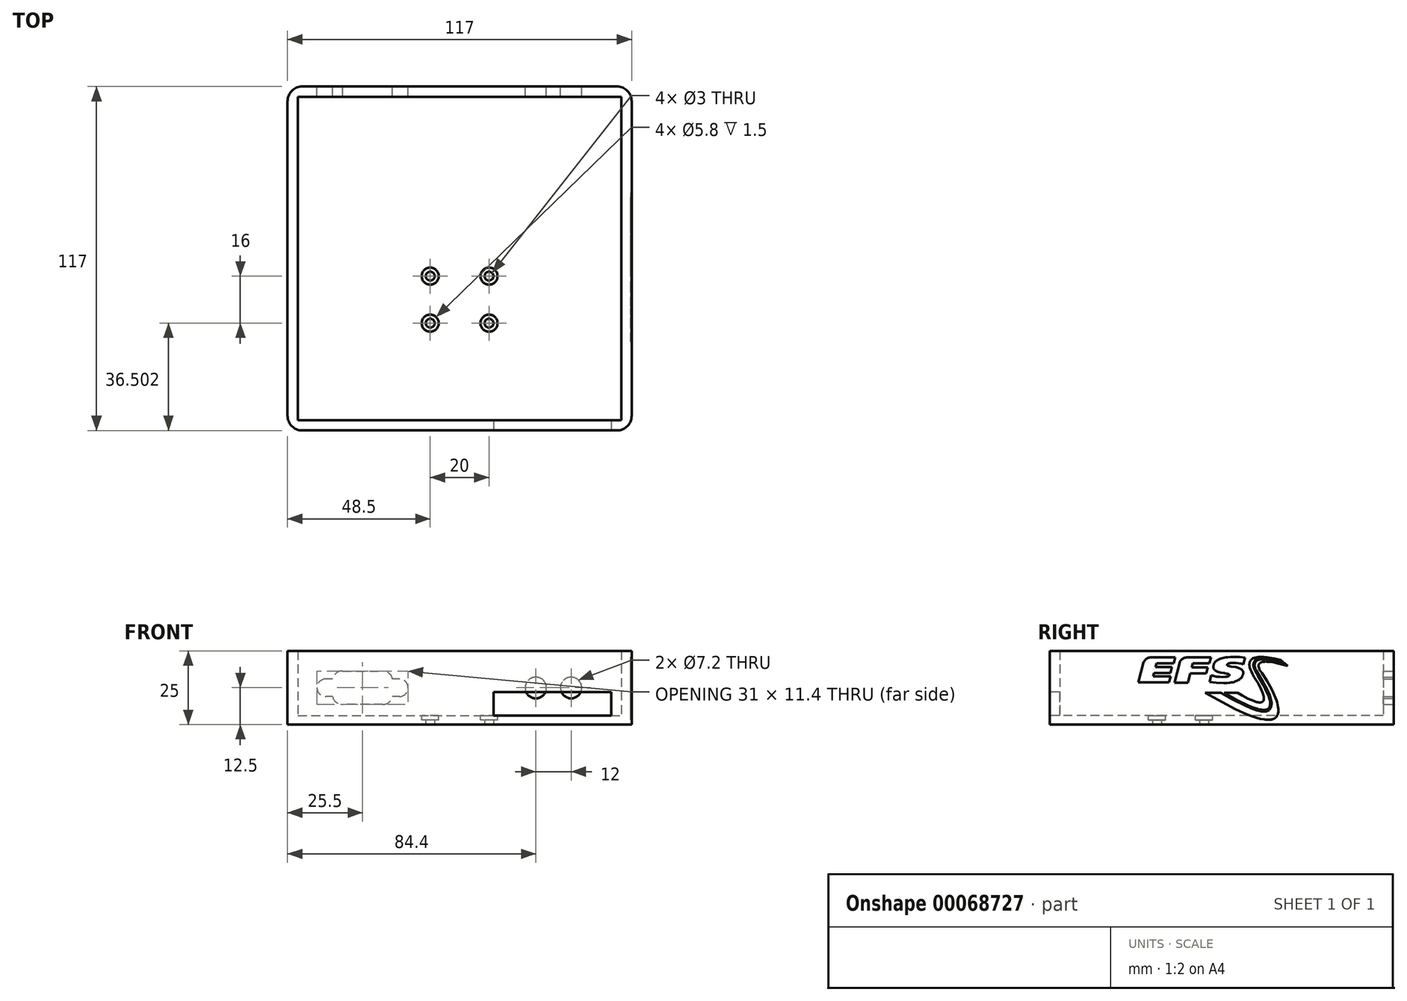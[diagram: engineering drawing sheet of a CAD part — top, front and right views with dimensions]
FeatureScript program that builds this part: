
annotation { "Feature Type Name" : "Feature", "Feature Type Description" : "" }
export const myFeature = defineFeature(function(context is Context, id is Id, definition is map)
    precondition{}
    {
        {
            var Q0;
            Q0=qCreatedBy(makeId("Top.planeOp"),FACE);
            var sketch = newSketch(context, id + "F0", { "sketchPlane" : qUnion([Q0])});
            skLineSegment(sketch, "E0.bottom", {"start": v(-55, 78.83) * mm, "end": v(55, 78.83) * mm});
            skLineSegment(sketch, "E0.top", {"start": v(-55, -31.17) * mm, "end": v(55, -31.17) * mm});
            skLineSegment(sketch, "E0.left", {"start": v(-55, 78.83) * mm, "end": v(-55, -31.17) * mm});
            skLineSegment(sketch, "E0.right", {"start": v(55, 78.83) * mm, "end": v(55, -31.17) * mm});
            skLineSegment(sketch, "E1.0", {"start": v(-58.5, 82.33) * mm, "end": v(-58.5, -34.67) * mm});
            skLineSegment(sketch, "E1.1", {"start": v(-58.5, 82.33) * mm, "end": v(58.5, 82.33) * mm});
            skLineSegment(sketch, "E1.2", {"start": v(58.5, 82.33) * mm, "end": v(58.5, -34.67) * mm});
            skLineSegment(sketch, "E1.3", {"start": v(-58.5, -34.67) * mm, "end": v(58.5, -34.67) * mm});
            skSolve(sketch);
        }
        {
            var Q0;
            Q0=makeQuery(id+"F0.imprint","IMPRINT",FACE,{"disambiguationData":[TD([[makeQuery(id+"F0.imprint","IMPRINT",EDGE,{"derivedFrom":sQuery(id+"F0.wireOp",EDGE,"E0.bottom")}),1.0]])]});
            extrude(context, id + "F1", {"entities" : qUnion([Q0]), "depth" : 25 * mm});
        }
        {
            var Q0;
            Q0=makeQuery(id+"F0.imprint","IMPRINT",FACE,{"disambiguationData":[TD([[makeQuery(id+"F0.imprint","IMPRINT",EDGE,{"derivedFrom":sQuery(id+"F0.wireOp",EDGE,"E0.bottom")}),-1.0]])]});
            var Q1;
            Q1=makeQuery(id+"F0.imprint","IMPRINT",FACE,{"disambiguationData":[TD([[makeQuery(id+"F0.imprint","IMPRINT",EDGE,{"derivedFrom":sQuery(id+"F0.wireOp",EDGE,"998007f4-a65a-47df-ae81-ff0484897dbd.bottom")}),1.0]])]});
            var Q2;
            Q2=makeQuery(id+"F0.imprint","IMPRINT",FACE,{"disambiguationData":[TD([[makeQuery(id+"F0.imprint","IMPRINT",EDGE,{"derivedFrom":sQuery(id+"F0.wireOp",EDGE,"998007f4-a65a-47df-ae81-ff0484897dbd.bottom")}),-1.0]])]});
            extrude(context, id + "F2", {"entities" : qUnion([Q0, Q1, Q2]), "operationType" : NewBodyOperationType.ADD, "depth" : 3 * mm});
        }
        {
            var Q0;
            Q0=makeQuery(id+"F1.opExtrude","SWEPT_EDGE",EDGE,{"disambiguationData":[OSD([sQuery(id+"F0.wireOp",EDGE,"E1.2"),sQuery(id+"F0.wireOp",EDGE,"E1.3")])]});
            fillet(context, id + "F3", {"entities" : qUnion([Q0]), "radius" : 5 * mm, "tangentPropagation" : true, "allowEdgeOverflow" : false});
        }
        {
            var Q0;
            Q0=makeQuery(id+"F1.opExtrude","SWEPT_EDGE",EDGE,{"disambiguationData":[OSD([sQuery(id+"F0.wireOp",EDGE,"E1.0"),sQuery(id+"F0.wireOp",EDGE,"E1.3")])]});
            fillet(context, id + "F4", {"entities" : qUnion([Q0]), "radius" : 5 * mm, "tangentPropagation" : true, "allowEdgeOverflow" : false});
        }
        {
            var Q0;
            Q0=makeQuery(id+"F1.opExtrude","SWEPT_EDGE",EDGE,{"disambiguationData":[OSD([sQuery(id+"F0.wireOp",EDGE,"E1.0"),sQuery(id+"F0.wireOp",EDGE,"E1.3")])]});
            var Q1;
            Q1=makeQuery(id+"F1.opExtrude","SWEPT_EDGE",EDGE,{"disambiguationData":[OSD([sQuery(id+"F0.wireOp",EDGE,"E1.1"),sQuery(id+"F0.wireOp",EDGE,"E1.2")])]});
            fillet(context, id + "F5", {"entities" : qUnion([Q0, Q1]), "radius" : 5 * mm, "tangentPropagation" : true, "allowEdgeOverflow" : false});
        }
        {
            var Q0;
            Q0=makeQuery(id+"F1.opExtrude","SWEPT_EDGE",EDGE,{"disambiguationData":[OSD([sQuery(id+"F0.wireOp",EDGE,"E1.0"),sQuery(id+"F0.wireOp",EDGE,"E1.1")])]});
            fillet(context, id + "F6", {"entities" : qUnion([Q0]), "radius" : 5 * mm, "tangentPropagation" : true, "allowEdgeOverflow" : false});
        }
        {
            var Q0;
            Q0=makeQuery(id+"F1.opExtrude","SWEPT_FACE",FACE,{"disambiguationData":[OSD([sQuery(id+"F0.wireOp",EDGE,"E1.1")])]});
            var sketch = newSketch(context, id + "F7", { "sketchPlane" : qUnion([Q0])});
            skArc(sketch, "E2", {"start": v(42.5, 12.68) * mm, "mid": v(42.5, 12.59) * mm, "end": v(42.5, 12.5) * mm});
            skArc(sketch, "E3", {"start": v(23.5, 12.32) * mm, "mid": v(23.5, 12.41) * mm, "end": v(23.5, 12.5) * mm});
            skArc(sketch, "E4", {"start": v(37.35, 12.5) * mm, "mid": v(37.35, 12.5) * mm, "end": v(37.35, 12.5) * mm});
            skArc(sketch, "E5", {"start": v(26.15, 18.2) * mm, "mid": v(24, 17.44) * mm, "end": v(22.82, 15.5) * mm});
            skArc(sketch, "E6", {"start": v(28.65, 12.5) * mm, "mid": v(26.03, 13.6) * mm, "end": v(23.5, 12.32) * mm});
            skLineSegment(sketch, "E7", {"start": v(20.5, 12.5) * mm, "end": v(45.5, 12.5) * mm, "construction": true});
            skPoint(sketch, "E8", {"position": v(33, 12.5) * mm});
            skLineSegment(sketch, "E9", {"start": v(33, 6.8) * mm, "end": v(33, 18.2) * mm, "construction": true});
            skLineSegment(sketch, "E10", {"start": v(20.5, 15.5) * mm, "end": v(22.82, 15.5) * mm});
            skLineSegment(sketch, "E11", {"start": v(20.5, 9.5) * mm, "end": v(22.82, 9.5) * mm});
            skLineSegment(sketch, "E12", {"start": v(43.18, 9.5) * mm, "end": v(45.5, 9.5) * mm});
            skLineSegment(sketch, "E13", {"start": v(43.18, 15.5) * mm, "end": v(45.5, 15.5) * mm});
            skLineSegment(sketch, "E14", {"start": v(26.15, 6.8) * mm, "end": v(39.85, 6.8) * mm});
            skLineSegment(sketch, "E15", {"start": v(39.85, 18.2) * mm, "end": v(26.15, 18.2) * mm});
            skArc(sketch, "E16.trimOffspring", {"start": v(42.35, 12.5) * mm, "mid": v(42.35, 12.5) * mm, "end": v(42.35, 12.5) * mm});
            skArc(sketch, "E17.trimOffspring", {"start": v(43.23, 14.47) * mm, "mid": v(42.37, 17.08) * mm, "end": v(39.85, 18.2) * mm});
            skArc(sketch, "E18.trimOffspring", {"start": v(45.5, 9.5) * mm, "mid": v(48.23, 13.75) * mm, "end": v(43.23, 14.47) * mm});
            skArc(sketch, "E19.trimOffspring", {"start": v(42.5, 12.32) * mm, "mid": v(42.43, 12.41) * mm, "end": v(42.35, 12.5) * mm});
            skArc(sketch, "E20.trimOffspring", {"start": v(39.72, 6.8) * mm, "mid": v(41.94, 7.52) * mm, "end": v(43.18, 9.5) * mm});
            skArc(sketch, "E21.trimOffspring", {"start": v(22.82, 9.5) * mm, "mid": v(24, 7.56) * mm, "end": v(26.15, 6.8) * mm});
            skArc(sketch, "E22.trimOffspring", {"start": v(20.5, 15.5) * mm, "mid": v(17.5, 12.5) * mm, "end": v(20.5, 9.5) * mm});
            skArc(sketch, "E23.trimOffspring", {"start": v(23.5, 12.68) * mm, "mid": v(23.57, 12.59) * mm, "end": v(23.65, 12.5) * mm});
            skCircle(sketch, "E24", {"center": v(-37.9, 12.5) * mm, "radius": 3.6 * mm});
            skCircle(sketch, "E25", {"center": v(-25.9, 12.5) * mm, "radius": 3.6 * mm});
            skLineSegment(sketch, "E26", {"start": v(-52.56, 12.5) * mm, "end": v(59.26, 12.5) * mm, "construction": true});
            skSolve(sketch);
        }
        {
            var Q0;
            Q0 = qSketchRegion(id + "F7", true);
            extrude(context, id + "F8", {"entities" : qUnion([Q0]), "operationType" : NewBodyOperationType.REMOVE, "oppositeDirection" : true, "depth" : 8.6 * mm});
        }
        {
            var Q0;
            Q0=makeQuery(id+"F1.opExtrude","SWEPT_FACE",FACE,{"disambiguationData":[OSD([sQuery(id+"F0.wireOp",EDGE,"E1.3")])]});
            var sketch = newSketch(context, id + "F9", { "sketchPlane" : qUnion([Q0])});
            skLineSegment(sketch, "E27.bottom", {"start": v(11.5, 11) * mm, "end": v(51.5, 11) * mm});
            skLineSegment(sketch, "E27.top", {"start": v(11.5, 3) * mm, "end": v(51.5, 3) * mm});
            skLineSegment(sketch, "E27.left", {"start": v(11.5, 11) * mm, "end": v(11.5, 3) * mm});
            skLineSegment(sketch, "E27.right", {"start": v(51.5, 11) * mm, "end": v(51.5, 3) * mm});
            skSolve(sketch);
        }
        {
            var Q0;
            Q0=makeQuery(id+"F9.imprint","IMPRINT",FACE,{"disambiguationData":[TD([[makeQuery(id+"F9.imprint","IMPRINT",EDGE,{"derivedFrom":sQuery(id+"F9.wireOp",EDGE,"E27.bottom")}),-1.0]])]});
            extrude(context, id + "F10", {"entities" : qUnion([Q0]), "operationType" : NewBodyOperationType.REMOVE, "oppositeDirection" : true, "depth" : 25 * mm});
        }
        {
            var Q0;
            {var subQ0=sQuery(id+"F0.wireOp",EDGE,"E0.right");var subQ1=sQuery(id+"F0.wireOp",EDGE,"E0.left");var subQ2=sQuery(id+"F0.wireOp",EDGE,"E0.top");var subQ3=sQuery(id+"F0.wireOp",EDGE,"E0.bottom");Q0=makeQuery(id+"F2.boolean.opBoolean","MERGE",FACE,{"derivedFrom":[makeQuery(id+"F1.opExtrude","CAP_FACE",FACE,{"disambiguationData":[OSD([subQ3,subQ2,subQ1,subQ0,sQuery(id+"F0.wireOp",EDGE,"E1.0"),sQuery(id+"F0.wireOp",EDGE,"E1.1"),sQuery(id+"F0.wireOp",EDGE,"E1.2"),sQuery(id+"F0.wireOp",EDGE,"E1.3")])],"isStart":true}),makeQuery(id+"F2.opExtrude","CAP_FACE",FACE,{"disambiguationData":[OSD([subQ3,subQ2,subQ1,subQ0])],"isStart":true})]});}
            var sketch = newSketch(context, id + "F11", { "sketchPlane" : qUnion([Q0])});
            skLineSegment(sketch, "E28.bottom", {"start": v(-27, 4.67) * mm, "end": v(27, 4.67) * mm, "construction": true});
            skLineSegment(sketch, "E28.top", {"start": v(-27, -24.33) * mm, "end": v(27, -24.33) * mm, "construction": true});
            skLineSegment(sketch, "E28.left", {"start": v(-27, 4.67) * mm, "end": v(-27, -24.33) * mm, "construction": true});
            skLineSegment(sketch, "E28.right", {"start": v(27, 4.67) * mm, "end": v(27, -24.33) * mm, "construction": true});
            skLineSegment(sketch, "E29", {"start": v(-32.07, -9.83) * mm, "end": v(32.08, -9.83) * mm, "construction": true});
            skPoint(sketch, "E29.endSnap0", {"position": v(27, -9.83) * mm});
            skLineSegment(sketch, "E30.bottom", {"start": v(-10, -1.83) * mm, "end": v(10, -1.83) * mm, "construction": true});
            skLineSegment(sketch, "E30.top", {"start": v(-10, -17.83) * mm, "end": v(10, -17.83) * mm, "construction": true});
            skLineSegment(sketch, "E30.left", {"start": v(-10, -1.83) * mm, "end": v(-10, -17.83) * mm, "construction": true});
            skLineSegment(sketch, "E30.right", {"start": v(10, -1.83) * mm, "end": v(10, -17.83) * mm, "construction": true});
            skCircle(sketch, "E31", {"center": v(-10, -1.83) * mm, "radius": 1.5 * mm});
            skCircle(sketch, "E32", {"center": v(10, -1.83) * mm, "radius": 1.5 * mm});
            skCircle(sketch, "E33", {"center": v(10, -17.83) * mm, "radius": 1.5 * mm});
            skCircle(sketch, "E34", {"center": v(-10, -17.83) * mm, "radius": 1.5 * mm});
            skSolve(sketch);
        }
        {
            var Q0;
            Q0 = qSketchRegion(id + "F11", true);
            var Q1;
            Q1 = qConstructionFilter(qBodyType(qCreatedBy(id + "F11" ,EDGE), BodyType.WIRE), ConstructionObject.NO);
            extrude(context, id + "F12", {"entities" : qUnion([Q0]), "operationType" : NewBodyOperationType.REMOVE, "surfaceEntities" : qUnion([Q1]), "endBound" : BoundingType.UP_TO_NEXT, "oppositeDirection" : true, "depth" : 25 * mm});
        }
        {
            var Q0;
            Q0=makeQuery(id+"F2.opExtrude","CAP_FACE",FACE,{"disambiguationData":[OSD([sQuery(id+"F0.wireOp",EDGE,"E0.bottom"),sQuery(id+"F0.wireOp",EDGE,"E0.top"),sQuery(id+"F0.wireOp",EDGE,"E0.left"),sQuery(id+"F0.wireOp",EDGE,"E0.right")])],"isStart":false});
            var sketch = newSketch(context, id + "F13", { "sketchPlane" : qUnion([Q0])});
            skCircle(sketch, "E35", {"center": v(-10, 17.83) * mm, "radius": 2.9 * mm});
            skCircle(sketch, "E36", {"center": v(10, 17.83) * mm, "radius": 2.9 * mm});
            skCircle(sketch, "E37", {"center": v(10, 1.83) * mm, "radius": 2.9 * mm});
            skCircle(sketch, "E38", {"center": v(-10, 1.83) * mm, "radius": 2.9 * mm});
            skSolve(sketch);
        }
        {
            var Q0;
            Q0 = qSketchRegion(id + "F13", true);
            extrude(context, id + "F14", {"entities" : qUnion([Q0]), "operationType" : NewBodyOperationType.REMOVE, "oppositeDirection" : true, "depth" : 1.5 * mm});
        }
        {
            var Q0;
            Q0=makeQuery(id+"F1.opExtrude","SWEPT_FACE",FACE,{"disambiguationData":[OSD([sQuery(id+"F0.wireOp",EDGE,"E1.2")])]});
            var sketch = newSketch(context, id + "F15", { "sketchPlane" : qUnion([Q0])});
            skLineSegment(sketch, "E39", {"start": v(101.82, 44.05) * mm, "end": v(111.92, 42) * mm});
            skLineSegment(sketch, "E40", {"start": v(24.91, 38.9) * mm, "end": v(25.1, 38.78) * mm});
            skLineSegment(sketch, "E41", {"start": v(45.69, 15.78) * mm, "end": v(44.77, 15.13) * mm});
            skLineSegment(sketch, "E42", {"start": v(22.06, 52.82) * mm, "end": v(24.8, 53.15) * mm});
            skLineSegment(sketch, "E43", {"start": v(96.55, -28.88) * mm, "end": v(96.67, -27.95) * mm});
            skLineSegment(sketch, "E44", {"start": v(5.07, 46.2) * mm, "end": v(5.92, 46.92) * mm});
            skLineSegment(sketch, "E45", {"start": v(24.5, 39.25) * mm, "end": v(19, 26.05) * mm});
            skLineSegment(sketch, "E46", {"start": v(72.1, 44.64) * mm, "end": v(71.84, 44.2) * mm});
            skLineSegment(sketch, "E47", {"start": v(109.68, -45.48) * mm, "end": v(109.95, -44.8) * mm});
            skLineSegment(sketch, "E48", {"start": v(93.48, -38.32) * mm, "end": v(93.03, -38.54) * mm});
            skLineSegment(sketch, "E49", {"start": v(24.93, 41.6) * mm, "end": v(24.83, 41.5) * mm});
            skLineSegment(sketch, "E50", {"start": v(8.12, 28.45) * mm, "end": v(5.92, 46.92) * mm});
            skLineSegment(sketch, "E51", {"start": v(79.46, 50.54) * mm, "end": v(77, 53.04) * mm});
            skLineSegment(sketch, "E52", {"start": v(83.6, -23.16) * mm, "end": v(83.29, -23.34) * mm});
            skLineSegment(sketch, "E53", {"start": v(84.03, -36.8) * mm, "end": v(85.54, -36.9) * mm});
            skLineSegment(sketch, "E54", {"start": v(63.64, 47.22) * mm, "end": v(63.33, 46.79) * mm});
            skLineSegment(sketch, "E55", {"start": v(80.93, 28.42) * mm, "end": v(79.45, 31.04) * mm});
            skLineSegment(sketch, "E56", {"start": v(71.38, 34.93) * mm, "end": v(71.84, 33.68) * mm});
            skLineSegment(sketch, "E57", {"start": v(70.75, 37.35) * mm, "end": v(77.35, 38.22) * mm});
            skLineSegment(sketch, "E58", {"start": v(38.75, 36.13) * mm, "end": v(27.74, 23.67) * mm});
            skLineSegment(sketch, "E59", {"start": v(51.4, 28.1) * mm, "end": v(51.47, 27.71) * mm});
            skLineSegment(sketch, "E60", {"start": v(90.59, -39.36) * mm, "end": v(92.14, -53.65) * mm});
            skLineSegment(sketch, "E61", {"start": v(69.43, 34.3) * mm, "end": v(69.06, 35.45) * mm});
            skLineSegment(sketch, "E62", {"start": v(78.07, 41.05) * mm, "end": v(78.24, 41.34) * mm});
            skLineSegment(sketch, "E63", {"start": v(-44.73, 52.76) * mm, "end": v(-46.39, 52.47) * mm});
            skLineSegment(sketch, "E64", {"start": v(28.02, 22.87) * mm, "end": v(28.02, 22.94) * mm});
            skLineSegment(sketch, "E65", {"start": v(72.75, 48.37) * mm, "end": v(71.76, 52.14) * mm});
            skLineSegment(sketch, "E66", {"start": v(41.62, -7.7) * mm, "end": v(42.43, -21.02) * mm});
            skLineSegment(sketch, "E67", {"start": v(33.75, 10.69) * mm, "end": v(27.55, 21.73) * mm});
            skLineSegment(sketch, "E68", {"start": v(-72.4, 26.11) * mm, "end": v(-69.69, 36.47) * mm});
            skLineSegment(sketch, "E69", {"start": v(93.9, -38.06) * mm, "end": v(100.52, -52.88) * mm});
            skLineSegment(sketch, "E70", {"start": v(10.75, 27.66) * mm, "end": v(8.12, 28.45) * mm});
            skLineSegment(sketch, "E71", {"start": v(70.54, 46.37) * mm, "end": v(71.03, 46.94) * mm});
            skLineSegment(sketch, "E72", {"start": v(70.66, 37.91) * mm, "end": v(70.75, 37.35) * mm});
            skLineSegment(sketch, "E73", {"start": v(27.85, 22.18) * mm, "end": v(27.9, 22.28) * mm});
            skLineSegment(sketch, "E74", {"start": v(100.4, 47.55) * mm, "end": v(95.22, 48.42) * mm});
            skLineSegment(sketch, "E75", {"start": v(-42.68, 9.9) * mm, "end": v(-38.65, 25.25) * mm});
            skLineSegment(sketch, "E76", {"start": v(-108.6, 52.25) * mm, "end": v(-110.07, 51.8) * mm});
            skLineSegment(sketch, "E77", {"start": v(74.9, 47.28) * mm, "end": v(78.87, 42.15) * mm});
            skLineSegment(sketch, "E78", {"start": v(13, -7.71) * mm, "end": v(-13.74, -7.7) * mm});
            skLineSegment(sketch, "E79", {"start": v(94.5, -53.67) * mm, "end": v(96.68, -53.54) * mm});
            skLineSegment(sketch, "E80", {"start": v(84.47, 50.78) * mm, "end": v(87.7, 50.66) * mm});
            skLineSegment(sketch, "E81", {"start": v(73.89, 25.15) * mm, "end": v(69.8, 19.07) * mm});
            skLineSegment(sketch, "E82", {"start": v(98.9, -30.58) * mm, "end": v(109.94, -28.46) * mm});
            skLineSegment(sketch, "E83", {"start": v(48.53, 32.43) * mm, "end": v(49.1, 31.93) * mm});
            skLineSegment(sketch, "E84", {"start": v(6.64, 20.22) * mm, "end": v(11.8, 19.7) * mm});
            skLineSegment(sketch, "E85", {"start": v(82.6, -23.65) * mm, "end": v(82.24, -23.78) * mm});
            skLineSegment(sketch, "E86", {"start": v(73.94, 29.26) * mm, "end": v(80.93, 28.42) * mm});
            skLineSegment(sketch, "E87", {"start": v(94.98, -33.24) * mm, "end": v(95.34, -32.65) * mm});
            skLineSegment(sketch, "E88", {"start": v(27.85, 23.51) * mm, "end": v(27.82, 23.57) * mm});
            skLineSegment(sketch, "E89", {"start": v(99.33, -27.45) * mm, "end": v(99.19, -29.03) * mm});
            skLineSegment(sketch, "E90", {"start": v(51.9, 41.15) * mm, "end": v(48.12, 42.04) * mm});
            skLineSegment(sketch, "E91", {"start": v(96.76, 44.76) * mm, "end": v(101.82, 44.05) * mm});
            skLineSegment(sketch, "E92", {"start": v(24.61, 39.12) * mm, "end": v(24.68, 39.06) * mm});
            skLineSegment(sketch, "E93", {"start": v(86.21, -16.87) * mm, "end": v(86.2, -17.95) * mm});
            skLineSegment(sketch, "E94", {"start": v(46.56, 16.46) * mm, "end": v(45.69, 15.78) * mm});
            skLineSegment(sketch, "E95", {"start": v(44.16, 34.74) * mm, "end": v(47.38, 17.19) * mm});
            skLineSegment(sketch, "E96", {"start": v(68.48, 38.65) * mm, "end": v(68.47, 39.76) * mm});
            skLineSegment(sketch, "E97", {"start": v(98.56, -19.54) * mm, "end": v(104.13, -11.65) * mm});
            skLineSegment(sketch, "E98", {"start": v(0.98, 34.99) * mm, "end": v(0.91, 35.28) * mm});
            skLineSegment(sketch, "E99", {"start": v(93.03, -38.54) * mm, "end": v(92.57, -38.74) * mm});
            skLineSegment(sketch, "E100", {"start": v(10.75, 27.66) * mm, "end": v(6.84, 47.59) * mm});
            skLineSegment(sketch, "E101", {"start": v(-103.12, 52.93) * mm, "end": v(-96.07, 42.57) * mm});
            skLineSegment(sketch, "E102", {"start": v(82.47, -36.62) * mm, "end": v(84.03, -36.8) * mm});
            skLineSegment(sketch, "E103", {"start": v(95.46, -36.78) * mm, "end": v(108.24, -47.97) * mm});
            skLineSegment(sketch, "E104", {"start": v(81.13, 50.7) * mm, "end": v(79.85, 53.23) * mm});
            skLineSegment(sketch, "E105", {"start": v(76.84, 7.3) * mm, "end": v(81.77, -2.3) * mm});
            skLineSegment(sketch, "E106", {"start": v(69.42, 51.38) * mm, "end": v(68.34, 50.9) * mm});
            skLineSegment(sketch, "E107", {"start": v(38.75, 36.13) * mm, "end": v(27.78, 23.62) * mm});
            skLineSegment(sketch, "E108", {"start": v(79.45, 31.04) * mm, "end": v(78.86, 32.26) * mm});
            skLineSegment(sketch, "E109", {"start": v(79.3, -36.1) * mm, "end": v(81.07, -24.05) * mm});
            skLineSegment(sketch, "E110", {"start": v(51.32, 28.5) * mm, "end": v(51.4, 28.1) * mm});
            skLineSegment(sketch, "E111", {"start": v(71, 36.17) * mm, "end": v(77.36, 37.8) * mm});
            skLineSegment(sketch, "E112", {"start": v(96.56, -22.22) * mm, "end": v(96.18, -19.96) * mm});
            skLineSegment(sketch, "E113", {"start": v(73.02, 45.8) * mm, "end": v(72.7, 45.43) * mm});
            skLineSegment(sketch, "E114", {"start": v(107.8, -48.53) * mm, "end": v(108.24, -47.97) * mm});
            skLineSegment(sketch, "E115", {"start": v(25.29, 38.68) * mm, "end": v(19, 26.05) * mm});
            skLineSegment(sketch, "E116", {"start": v(24.18, 40.05) * mm, "end": v(24.19, 39.97) * mm});
            skLineSegment(sketch, "E117", {"start": v(-54.62, 47.7) * mm, "end": v(-55.13, 47) * mm});
            skLineSegment(sketch, "E118", {"start": v(96.76, -24.55) * mm, "end": v(85.15, -21.66) * mm});
            skLineSegment(sketch, "E119", {"start": v(62.33, 44.85) * mm, "end": v(62.14, 44.32) * mm});
            skLineSegment(sketch, "E120", {"start": v(96.56, -22.22) * mm, "end": v(85.53, -21) * mm});
            skLineSegment(sketch, "E121", {"start": v(-113.6, 49.98) * mm, "end": v(-97.67, 36.47) * mm});
            skLineSegment(sketch, "E122", {"start": v(78.36, -24.16) * mm, "end": v(77.37, -24.08) * mm});
            skLineSegment(sketch, "E123", {"start": v(33.3, -19.22) * mm, "end": v(37.7, -35.67) * mm});
            skLineSegment(sketch, "E124", {"start": v(9.82, 49.35) * mm, "end": v(12.02, 50.32) * mm});
            skLineSegment(sketch, "E125", {"start": v(-69.69, 36.47) * mm, "end": v(-97.67, 36.47) * mm});
            skLineSegment(sketch, "E126", {"start": v(92.7, -35.45) * mm, "end": v(93.22, -35.1) * mm});
            skLineSegment(sketch, "E127", {"start": v(33.75, 10.69) * mm, "end": v(27.63, 21.82) * mm});
            skLineSegment(sketch, "E128", {"start": v(27.74, 23.67) * mm, "end": v(27.65, 23.77) * mm});
            skLineSegment(sketch, "E129", {"start": v(71.03, 46.94) * mm, "end": v(71.57, 47.47) * mm});
            skLineSegment(sketch, "E130", {"start": v(-5.95, 42.57) * mm, "end": v(-34.1, 42.57) * mm});
            skLineSegment(sketch, "E131", {"start": v(98.71, -31.34) * mm, "end": v(98.48, -32.1) * mm});
            skLineSegment(sketch, "E132", {"start": v(59.24, -29.13) * mm, "end": v(69.44, -22.1) * mm});
            skLineSegment(sketch, "E133", {"start": v(25.04, 41.68) * mm, "end": v(24.93, 41.6) * mm});
            skLineSegment(sketch, "E134", {"start": v(84.55, 44.78) * mm, "end": v(85.49, 44.93) * mm});
            skLineSegment(sketch, "E135", {"start": v(27.7, 21.9) * mm, "end": v(27.75, 22) * mm});
            skLineSegment(sketch, "E136", {"start": v(-66.8, 42.57) * mm, "end": v(-64.09, 52.93) * mm});
            skLineSegment(sketch, "E137", {"start": v(75.3, 47.52) * mm, "end": v(79.11, 42.4) * mm});
            skLineSegment(sketch, "E138", {"start": v(42.84, 13.96) * mm, "end": v(28.02, 22.87) * mm});
            skLineSegment(sketch, "E139", {"start": v(24.2, 40.3) * mm, "end": v(12.02, 50.32) * mm});
            skLineSegment(sketch, "E140", {"start": v(73.94, 29.26) * mm, "end": v(79.45, 31.04) * mm});
            skLineSegment(sketch, "E141", {"start": v(63.75, -33.69) * mm, "end": v(54.65, -29.66) * mm});
            skLineSegment(sketch, "E142", {"start": v(101, 48.88) * mm, "end": v(114.25, 45.83) * mm});
            skLineSegment(sketch, "E143", {"start": v(95.65, -17.76) * mm, "end": v(86.04, -19.4) * mm});
            skLineSegment(sketch, "E144", {"start": v(76.03, 21.47) * mm, "end": v(76.84, 7.3) * mm});
            skLineSegment(sketch, "E145", {"start": v(6.87, 28.92) * mm, "end": v(5.73, 29.47) * mm});
            skLineSegment(sketch, "E146", {"start": v(98.71, -31.34) * mm, "end": v(110.68, -32.35) * mm});
            skLineSegment(sketch, "E147", {"start": v(70.68, 40.46) * mm, "end": v(77.55, 39.74) * mm});
            skLineSegment(sketch, "E148", {"start": v(46.53, 33.73) * mm, "end": v(47.25, 33.33) * mm});
            skLineSegment(sketch, "E149", {"start": v(24.25, 20.2) * mm, "end": v(24.97, 20.39) * mm});
            skLineSegment(sketch, "E150", {"start": v(96.18, -19.96) * mm, "end": v(85.82, -20.24) * mm});
            skLineSegment(sketch, "E151", {"start": v(26.3, 42.34) * mm, "end": v(24.8, 53.15) * mm});
            skLineSegment(sketch, "E152", {"start": v(24.5, 41.08) * mm, "end": v(16.85, 51.82) * mm});
            skLineSegment(sketch, "E153", {"start": v(89.1, -36.72) * mm, "end": v(83.6, -23.16) * mm});
            skLineSegment(sketch, "E154", {"start": v(-127, 9.9) * mm, "end": v(-101.93, 20.25) * mm});
            skLineSegment(sketch, "E155", {"start": v(24.44, 39.32) * mm, "end": v(19, 26.05) * mm});
            skLineSegment(sketch, "E156", {"start": v(97, -35.12) * mm, "end": v(111.05, -39.48) * mm});
            skLineSegment(sketch, "E157", {"start": v(47.38, 17.19) * mm, "end": v(46.56, 16.46) * mm});
            skLineSegment(sketch, "E158", {"start": v(100.52, -52.88) * mm, "end": v(101.38, -52.64) * mm});
            skLineSegment(sketch, "E159", {"start": v(0.91, 35.28) * mm, "end": v(0.86, 35.58) * mm});
            skLineSegment(sketch, "E160", {"start": v(110.2, -44.1) * mm, "end": v(110.6, -42.64) * mm});
            skLineSegment(sketch, "E161", {"start": v(93.9, -38.06) * mm, "end": v(93.68, -38.2) * mm});
            skLineSegment(sketch, "E162", {"start": v(70.56, 51.78) * mm, "end": v(69.42, 51.38) * mm});
            skLineSegment(sketch, "E163", {"start": v(38.75, 36.13) * mm, "end": v(27.82, 23.57) * mm});
            skLineSegment(sketch, "E164", {"start": v(51.9, 41.15) * mm, "end": v(54.79, 52.2) * mm});
            skLineSegment(sketch, "E165", {"start": v(1.15, 34.43) * mm, "end": v(1.06, 34.7) * mm});
            skLineSegment(sketch, "E166", {"start": v(24.2, 39.9) * mm, "end": v(24.2, 39.82) * mm});
            skLineSegment(sketch, "E167", {"start": v(86.12, -18.94) * mm, "end": v(86.04, -19.4) * mm});
            skLineSegment(sketch, "E168", {"start": v(72.89, 31.28) * mm, "end": v(73.94, 29.26) * mm});
            skLineSegment(sketch, "E169", {"start": v(79.77, -38.98) * mm, "end": v(73.97, -50.27) * mm});
            skLineSegment(sketch, "E170", {"start": v(51.2, 28.86) * mm, "end": v(51.32, 28.5) * mm});
            skLineSegment(sketch, "E171", {"start": v(69.44, -22.1) * mm, "end": v(64.42, -20.1) * mm});
            skLineSegment(sketch, "E172", {"start": v(59.24, -29.13) * mm, "end": v(64.42, -20.1) * mm});
            skLineSegment(sketch, "E173", {"start": v(84.8, 6.3) * mm, "end": v(81.77, -2.3) * mm});
            skLineSegment(sketch, "E174", {"start": v(24.19, 40.13) * mm, "end": v(24.18, 40.05) * mm});
            skLineSegment(sketch, "E175", {"start": v(80.57, 43.46) * mm, "end": v(81.26, 43.8) * mm});
            skLineSegment(sketch, "E176", {"start": v(-55.13, 47) * mm, "end": v(-55.56, 46.34) * mm});
            skLineSegment(sketch, "E177", {"start": v(70.62, 39.82) * mm, "end": v(77.47, 39.38) * mm});
            skLineSegment(sketch, "E178", {"start": v(28, 22.61) * mm, "end": v(28.01, 22.74) * mm});
            skLineSegment(sketch, "E179", {"start": v(62.14, 44.32) * mm, "end": v(61.98, 43.76) * mm});
            skLineSegment(sketch, "E180", {"start": v(71.37, 43.27) * mm, "end": v(77.9, 40.74) * mm});
            skLineSegment(sketch, "E181", {"start": v(74.3, 52.69) * mm, "end": v(71.76, 52.14) * mm});
            skLineSegment(sketch, "E182", {"start": v(77.5, 36.47) * mm, "end": v(77.38, 37.38) * mm});
            skLineSegment(sketch, "E183", {"start": v(38.54, 12.05) * mm, "end": v(27.9, 22.28) * mm});
            skLineSegment(sketch, "E184", {"start": v(25.29, 38.68) * mm, "end": v(25.5, 38.58) * mm});
            skLineSegment(sketch, "E185", {"start": v(93.9, -38.06) * mm, "end": v(102.2, -52.36) * mm});
            skLineSegment(sketch, "E186", {"start": v(80.68, 49.04) * mm, "end": v(79.78, 48.94) * mm});
            skLineSegment(sketch, "E187", {"start": v(79.31, -24.19) * mm, "end": v(78.36, -24.16) * mm});
            skLineSegment(sketch, "E188", {"start": v(48.53, 32.43) * mm, "end": v(51.35, 24.6) * mm});
            skLineSegment(sketch, "E189", {"start": v(71.46, 29.62) * mm, "end": v(70.35, 31.97) * mm});
            skLineSegment(sketch, "E190", {"start": v(69.05, 43.54) * mm, "end": v(62.54, 45.36) * mm});
            skLineSegment(sketch, "E191", {"start": v(69.7, 45.07) * mm, "end": v(70.1, 45.75) * mm});
            skLineSegment(sketch, "E192", {"start": v(-51.51, 50.44) * mm, "end": v(-35.93, 35.6) * mm});
            skLineSegment(sketch, "E193", {"start": v(96.79, -25.74) * mm, "end": v(84.94, -21.96) * mm});
            skLineSegment(sketch, "E194", {"start": v(33.75, 10.69) * mm, "end": v(27.7, 21.9) * mm});
            skLineSegment(sketch, "E195", {"start": v(27.78, 23.62) * mm, "end": v(27.74, 23.67) * mm});
            skLineSegment(sketch, "E196", {"start": v(25.15, 41.77) * mm, "end": v(25.04, 41.68) * mm});
            skLineSegment(sketch, "E197", {"start": v(70.6, 39.15) * mm, "end": v(70.62, 38.45) * mm});
            skLineSegment(sketch, "E198", {"start": v(40.76, 12.93) * mm, "end": v(28.01, 22.74) * mm});
            skLineSegment(sketch, "E199", {"start": v(27.93, 22.37) * mm, "end": v(27.96, 22.47) * mm});
            skLineSegment(sketch, "E200", {"start": v(50.4, 21.52) * mm, "end": v(49.95, 20.56) * mm});
            skLineSegment(sketch, "E201", {"start": v(95.66, -32.01) * mm, "end": v(83.9, -22.96) * mm});
            skLineSegment(sketch, "E202", {"start": v(-116.5, 47.1) * mm, "end": v(-116.97, 46.4) * mm});
            skLineSegment(sketch, "E203", {"start": v(24.18, 40.05) * mm, "end": v(9.82, 49.35) * mm});
            skLineSegment(sketch, "E204", {"start": v(89.6, -53.49) * mm, "end": v(92.14, -53.65) * mm});
            skLineSegment(sketch, "E205", {"start": v(42.84, 13.96) * mm, "end": v(28.02, 22.94) * mm});
            skLineSegment(sketch, "E206", {"start": v(8.12, 28.45) * mm, "end": v(6.87, 28.92) * mm});
            skLineSegment(sketch, "E207", {"start": v(111.06, -36.03) * mm, "end": v(110.92, -34.22) * mm});
            skLineSegment(sketch, "E208", {"start": v(73.94, 29.26) * mm, "end": v(78.86, 32.26) * mm});
            skLineSegment(sketch, "E209", {"start": v(-0.6, 21.69) * mm, "end": v(1.69, 21.1) * mm});
            skLineSegment(sketch, "E210", {"start": v(97.13, -34.93) * mm, "end": v(111.1, -37.79) * mm});
            skLineSegment(sketch, "E211", {"start": v(25.68, 42.08) * mm, "end": v(22.06, 52.82) * mm});
            skLineSegment(sketch, "E212", {"start": v(99.28, -24.25) * mm, "end": v(99.36, -25.85) * mm});
            skLineSegment(sketch, "E213", {"start": v(24.4, 39.38) * mm, "end": v(13.5, 27) * mm});
            skLineSegment(sketch, "E214", {"start": v(85.94, -14.4) * mm, "end": v(86.12, -15.69) * mm});
            skLineSegment(sketch, "E215", {"start": v(59.24, -29.13) * mm, "end": v(68.88, -33.05) * mm});
            skLineSegment(sketch, "E216", {"start": v(-118, 44.15) * mm, "end": v(-100.4, 26.11) * mm});
            skLineSegment(sketch, "E217", {"start": v(95.65, -17.76) * mm, "end": v(86.12, -18.94) * mm});
            skLineSegment(sketch, "E218", {"start": v(89.52, -39.56) * mm, "end": v(89.6, -53.49) * mm});
            skLineSegment(sketch, "E219", {"start": v(4.28, 45.44) * mm, "end": v(5.07, 46.2) * mm});
            skLineSegment(sketch, "E220", {"start": v(71.84, 44.2) * mm, "end": v(71.6, 43.75) * mm});
            skLineSegment(sketch, "E221", {"start": v(109.95, -44.8) * mm, "end": v(110.2, -44.1) * mm});
            skLineSegment(sketch, "E222", {"start": v(24.83, 41.5) * mm, "end": v(24.74, 41.4) * mm});
            skLineSegment(sketch, "E223", {"start": v(-116.97, 46.4) * mm, "end": v(-117.34, 45.73) * mm});
            skLineSegment(sketch, "E224", {"start": v(38.75, 36.13) * mm, "end": v(27.85, 23.51) * mm});
            skLineSegment(sketch, "E225", {"start": v(89.75, -36.6) * mm, "end": v(90.4, -36.44) * mm});
            skLineSegment(sketch, "E226", {"start": v(67.32, 50.39) * mm, "end": v(66.37, 49.8) * mm});
            skLineSegment(sketch, "E227", {"start": v(48.12, 42.04) * mm, "end": v(45.3, 53.27) * mm});
            skLineSegment(sketch, "E228", {"start": v(69.05, 43.54) * mm, "end": v(62.78, 45.86) * mm});
            skLineSegment(sketch, "E229", {"start": v(24.2, 39.82) * mm, "end": v(24.23, 39.74) * mm});
            skLineSegment(sketch, "E230", {"start": v(71.84, 33.68) * mm, "end": v(72.89, 31.28) * mm});
            skLineSegment(sketch, "E231", {"start": v(95.46, -36.78) * mm, "end": v(109.03, -46.77) * mm});
            skLineSegment(sketch, "E232", {"start": v(76.16, 47.94) * mm, "end": v(75.3, 47.52) * mm});
            skLineSegment(sketch, "E233", {"start": v(96.39, -29.75) * mm, "end": v(96.55, -28.88) * mm});
            skLineSegment(sketch, "E234", {"start": v(80.68, 49.04) * mm, "end": v(82, 44.1) * mm});
            skLineSegment(sketch, "E235", {"start": v(73.73, 46.45) * mm, "end": v(73.37, 46.13) * mm});
            skLineSegment(sketch, "E236", {"start": v(76.16, 47.94) * mm, "end": v(79.37, 42.63) * mm});
            skLineSegment(sketch, "E237", {"start": v(92.57, -38.74) * mm, "end": v(94.5, -53.67) * mm});
            skLineSegment(sketch, "E238", {"start": v(25.1, 38.78) * mm, "end": v(19, 26.05) * mm});
            skLineSegment(sketch, "E239", {"start": v(36.19, 11.31) * mm, "end": v(27.85, 22.18) * mm});
            skLineSegment(sketch, "E240", {"start": v(73.73, 46.45) * mm, "end": v(78.43, 41.63) * mm});
            skLineSegment(sketch, "E241", {"start": v(-42.92, 52.93) * mm, "end": v(-44.73, 52.76) * mm});
            skLineSegment(sketch, "E242", {"start": v(61.98, 43.76) * mm, "end": v(61.84, 43.2) * mm});
            skLineSegment(sketch, "E243", {"start": v(40.76, 12.93) * mm, "end": v(28, 22.61) * mm});
            skLineSegment(sketch, "E244", {"start": v(57.68, -44.54) * mm, "end": v(66.26, -47.78) * mm});
            skLineSegment(sketch, "E245", {"start": v(46.53, 33.73) * mm, "end": v(51.12, 23.58) * mm});
            skLineSegment(sketch, "E246", {"start": v(77, 53.04) * mm, "end": v(74.3, 52.69) * mm});
            skLineSegment(sketch, "E247", {"start": v(25.5, 38.58) * mm, "end": v(25.74, 38.5) * mm});
            skLineSegment(sketch, "E248", {"start": v(48.53, 32.43) * mm, "end": v(51.49, 25.55) * mm});
            skLineSegment(sketch, "E249", {"start": v(85.15, -21.66) * mm, "end": v(84.94, -21.96) * mm});
            skLineSegment(sketch, "E250", {"start": v(54.65, -29.66) * mm, "end": v(37.7, -35.67) * mm});
            skLineSegment(sketch, "E251", {"start": v(50.12, 30.82) * mm, "end": v(50.55, 30.21) * mm});
            skLineSegment(sketch, "E252", {"start": v(38.54, 12.05) * mm, "end": v(27.93, 22.37) * mm});
            skLineSegment(sketch, "E253", {"start": v(18.48, -7.73) * mm, "end": v(24.63, -11.2) * mm});
            skLineSegment(sketch, "E254", {"start": v(5.92, 46.92) * mm, "end": v(6.84, 47.59) * mm});
            skLineSegment(sketch, "E255", {"start": v(70.35, 31.97) * mm, "end": v(69.43, 34.3) * mm});
            skLineSegment(sketch, "E256", {"start": v(2.9, 31.58) * mm, "end": v(0.79, 37.52) * mm});
            skLineSegment(sketch, "E257", {"start": v(27.82, 23.57) * mm, "end": v(27.78, 23.62) * mm});
            skLineSegment(sketch, "E258", {"start": v(79.77, -38.98) * mm, "end": v(74.4, -37.6) * mm});
            skLineSegment(sketch, "E259", {"start": v(27.55, 21.73) * mm, "end": v(27.63, 21.82) * mm});
            skLineSegment(sketch, "E260", {"start": v(78.64, 41.9) * mm, "end": v(78.87, 42.15) * mm});
            skLineSegment(sketch, "E261", {"start": v(24.2, 40.22) * mm, "end": v(12.02, 50.32) * mm});
            skLineSegment(sketch, "E262", {"start": v(-44.73, 52.76) * mm, "end": v(-34.1, 42.57) * mm});
            skLineSegment(sketch, "E263", {"start": v(-115.95, 47.82) * mm, "end": v(-116.5, 47.1) * mm});
            skLineSegment(sketch, "E264", {"start": v(24.19, 39.97) * mm, "end": v(6.84, 47.59) * mm});
            skLineSegment(sketch, "E265", {"start": v(5.2, 29.77) * mm, "end": v(4.68, 30.1) * mm});
            skLineSegment(sketch, "E266", {"start": v(77.41, 39) * mm, "end": v(77.47, 39.38) * mm});
            skLineSegment(sketch, "E267", {"start": v(96.39, -29.75) * mm, "end": v(84.19, -22.74) * mm});
            skLineSegment(sketch, "E268", {"start": v(98.48, -32.1) * mm, "end": v(110.68, -32.35) * mm});
            skLineSegment(sketch, "E269", {"start": v(1.69, 21.1) * mm, "end": v(6.64, 20.22) * mm});
            skLineSegment(sketch, "E270", {"start": v(82.24, -23.78) * mm, "end": v(81.86, -23.89) * mm});
            skLineSegment(sketch, "E271", {"start": v(24.57, 41.2) * mm, "end": v(16.85, 51.82) * mm});
            skLineSegment(sketch, "E272", {"start": v(79.46, 50.54) * mm, "end": v(81.13, 50.7) * mm});
            skLineSegment(sketch, "E273", {"start": v(96.45, -35.79) * mm, "end": v(95.46, -36.78) * mm});
            skLineSegment(sketch, "E274", {"start": v(48.12, 42.04) * mm, "end": v(43.98, 42.73) * mm});
            skLineSegment(sketch, "E275", {"start": v(87.5, 45.13) * mm, "end": v(89.65, 45.2) * mm});
            skLineSegment(sketch, "E276", {"start": v(69.7, 45.07) * mm, "end": v(65.49, 49.15) * mm});
            skLineSegment(sketch, "E277", {"start": v(38.54, 12.05) * mm, "end": v(36.19, 11.31) * mm});
            skLineSegment(sketch, "E278", {"start": v(95.65, -17.76) * mm, "end": v(86.17, -18.46) * mm});
            skLineSegment(sketch, "E279", {"start": v(-38.65, 25.25) * mm, "end": v(-11.35, 25.25) * mm});
            skLineSegment(sketch, "E280", {"start": v(71.03, 46.94) * mm, "end": v(67.32, 50.39) * mm});
            skLineSegment(sketch, "E281", {"start": v(45.3, 53.27) * mm, "end": v(54.79, 52.2) * mm});
            skLineSegment(sketch, "E282", {"start": v(102.2, -52.36) * mm, "end": v(102.97, -52.05) * mm});
            skLineSegment(sketch, "E283", {"start": v(0.78, 36.2) * mm, "end": v(0.76, 36.84) * mm});
            skLineSegment(sketch, "E284", {"start": v(107.53, -20.23) * mm, "end": v(104.13, -11.65) * mm});
            skLineSegment(sketch, "E285", {"start": v(44.16, 34.74) * mm, "end": v(49.41, 19.65) * mm});
            skLineSegment(sketch, "E286", {"start": v(38.75, 36.13) * mm, "end": v(27.88, 23.46) * mm});
            skLineSegment(sketch, "E287", {"start": v(89.1, -36.72) * mm, "end": v(89.75, -36.6) * mm});
            skLineSegment(sketch, "E288", {"start": v(69.8, 19.07) * mm, "end": v(76.84, 7.3) * mm});
            skLineSegment(sketch, "E289", {"start": v(-56.18, 45.13) * mm, "end": v(-56.54, 44.2) * mm});
            skLineSegment(sketch, "E290", {"start": v(1.61, 33.4) * mm, "end": v(1.37, 33.9) * mm});
            skLineSegment(sketch, "E291", {"start": v(24.23, 39.74) * mm, "end": v(24.25, 39.66) * mm});
            skLineSegment(sketch, "E292", {"start": v(82.47, -36.62) * mm, "end": v(82.24, -23.78) * mm});
            skLineSegment(sketch, "E293", {"start": v(51.55, 26.45) * mm, "end": v(51.49, 25.55) * mm});
            skLineSegment(sketch, "E294", {"start": v(96.18, -30.56) * mm, "end": v(96.39, -29.75) * mm});
            skLineSegment(sketch, "E295", {"start": v(73.37, 46.13) * mm, "end": v(73.02, 45.8) * mm});
            skLineSegment(sketch, "E296", {"start": v(24.2, 40.3) * mm, "end": v(24.2, 40.22) * mm});
            skLineSegment(sketch, "E297", {"start": v(108.24, -47.97) * mm, "end": v(108.65, -47.38) * mm});
            skLineSegment(sketch, "E298", {"start": v(77.04, 48.28) * mm, "end": v(79.65, 42.86) * mm});
            skLineSegment(sketch, "E299", {"start": v(24.35, 39.45) * mm, "end": v(13.5, 27) * mm});
            skLineSegment(sketch, "E300", {"start": v(-55.9, 45.7) * mm, "end": v(-56.18, 45.13) * mm});
            skLineSegment(sketch, "E301", {"start": v(38.54, 12.05) * mm, "end": v(27.96, 22.47) * mm});
            skLineSegment(sketch, "E302", {"start": v(62.54, 45.36) * mm, "end": v(62.33, 44.85) * mm});
            skLineSegment(sketch, "E303", {"start": v(79.85, 53.23) * mm, "end": v(77, 53.04) * mm});
            skLineSegment(sketch, "E304", {"start": v(25.74, 38.5) * mm, "end": v(26, 38.41) * mm});
            skLineSegment(sketch, "E305", {"start": v(85.35, -21.34) * mm, "end": v(85.15, -21.66) * mm});
            skLineSegment(sketch, "E306", {"start": v(77.99, 34.49) * mm, "end": v(77.7, 35.51) * mm});
            skLineSegment(sketch, "E307", {"start": v(63.75, -33.69) * mm, "end": v(57.68, -44.54) * mm});
            skLineSegment(sketch, "E308", {"start": v(75.3, 47.52) * mm, "end": v(74.9, 47.28) * mm});
            skLineSegment(sketch, "E309", {"start": v(-106.95, 52.6) * mm, "end": v(-96.07, 42.57) * mm});
            skLineSegment(sketch, "E310", {"start": v(76.03, 21.47) * mm, "end": v(73.89, 25.15) * mm});
            skLineSegment(sketch, "E311", {"start": v(69.06, 35.45) * mm, "end": v(63.22, 32) * mm});
            skLineSegment(sketch, "E312", {"start": v(6.84, 47.59) * mm, "end": v(7.8, 48.21) * mm});
            skLineSegment(sketch, "E313", {"start": v(-5.95, 42.57) * mm, "end": v(-3.23, 52.93) * mm});
            skLineSegment(sketch, "E314", {"start": v(27.65, 23.77) * mm, "end": v(27.56, 23.86) * mm});
            skLineSegment(sketch, "E315", {"start": v(98.48, -32.1) * mm, "end": v(98.2, -32.83) * mm});
            skLineSegment(sketch, "E316", {"start": v(28.44, 37.8) * mm, "end": v(25.63, 24.77) * mm});
            skLineSegment(sketch, "E317", {"start": v(25.4, 41.93) * mm, "end": v(25.28, 41.85) * mm});
            skLineSegment(sketch, "E318", {"start": v(74.4, -37.6) * mm, "end": v(66.26, -47.78) * mm});
            skLineSegment(sketch, "E319", {"start": v(27.63, 21.82) * mm, "end": v(27.7, 21.9) * mm});
            skLineSegment(sketch, "E320", {"start": v(78.87, 42.15) * mm, "end": v(79.11, 42.4) * mm});
            skLineSegment(sketch, "E321", {"start": v(92.17, -35.76) * mm, "end": v(95.34, -32.65) * mm});
            skLineSegment(sketch, "E322", {"start": v(24.19, 40.13) * mm, "end": v(9.82, 49.35) * mm});
            skLineSegment(sketch, "E323", {"start": v(49.41, 19.65) * mm, "end": v(48.8, 18.78) * mm});
            skLineSegment(sketch, "E324", {"start": v(-64.09, 52.93) * mm, "end": v(-103.12, 52.93) * mm});
            skLineSegment(sketch, "E325", {"start": v(22.65, 19.88) * mm, "end": v(24.25, 20.2) * mm});
            skLineSegment(sketch, "E326", {"start": v(24.63, -11.2) * mm, "end": v(42.43, -21.02) * mm});
            skLineSegment(sketch, "E327", {"start": v(97.54, -34.25) * mm, "end": v(111.1, -37.79) * mm});
            skLineSegment(sketch, "E328", {"start": v(77.84, 50.29) * mm, "end": v(79.46, 50.54) * mm});
            skLineSegment(sketch, "E329", {"start": v(90.59, -39.36) * mm, "end": v(89.52, -39.56) * mm});
            skLineSegment(sketch, "E330", {"start": v(96.16, -11.73) * mm, "end": v(97.81, -16.61) * mm});
            skLineSegment(sketch, "E331", {"start": v(85.49, 44.93) * mm, "end": v(87.5, 45.13) * mm});
            skLineSegment(sketch, "E332", {"start": v(25.4, 41.93) * mm, "end": v(22.06, 52.82) * mm});
            skLineSegment(sketch, "E333", {"start": v(95.65, -17.76) * mm, "end": v(86.2, -17.95) * mm});
            skLineSegment(sketch, "E334", {"start": v(24.4, 39.38) * mm, "end": v(24.44, 39.32) * mm});
            skLineSegment(sketch, "E335", {"start": v(85.54, -36.9) * mm, "end": v(83.29, -23.34) * mm});
            skLineSegment(sketch, "E336", {"start": v(101.38, -52.64) * mm, "end": v(102.2, -52.36) * mm});
            skLineSegment(sketch, "E337", {"start": v(95.46, -36.78) * mm, "end": v(106.27, -50.06) * mm});
            skLineSegment(sketch, "E338", {"start": v(2.95, 43.75) * mm, "end": v(3.58, 44.62) * mm});
            skLineSegment(sketch, "E339", {"start": v(24.65, 41.3) * mm, "end": v(24.57, 41.2) * mm});
            skLineSegment(sketch, "E340", {"start": v(76.27, 49.92) * mm, "end": v(74.3, 52.69) * mm});
            skLineSegment(sketch, "E341", {"start": v(38.75, 36.13) * mm, "end": v(27.9, 23.4) * mm});
            skLineSegment(sketch, "E342", {"start": v(81.07, -24.05) * mm, "end": v(80.21, -24.15) * mm});
            skLineSegment(sketch, "E343", {"start": v(88.42, -36.81) * mm, "end": v(89.1, -36.72) * mm});
            skLineSegment(sketch, "E344", {"start": v(44.77, 15.13) * mm, "end": v(28, 23.06) * mm});
            skLineSegment(sketch, "E345", {"start": v(68.52, 40.8) * mm, "end": v(61.55, 40.02) * mm});
            skLineSegment(sketch, "E346", {"start": v(1.37, 33.9) * mm, "end": v(1.15, 34.43) * mm});
            skLineSegment(sketch, "E347", {"start": v(82.47, -36.62) * mm, "end": v(81.86, -23.89) * mm});
            skLineSegment(sketch, "E348", {"start": v(86.04, -19.4) * mm, "end": v(85.94, -19.83) * mm});
            skLineSegment(sketch, "E349", {"start": v(96.67, -27.95) * mm, "end": v(96.75, -26.95) * mm});
            skLineSegment(sketch, "E350", {"start": v(36.19, 11.31) * mm, "end": v(27.75, 22) * mm});
            skLineSegment(sketch, "E351", {"start": v(42.45, 35.3) * mm, "end": v(45.69, 15.78) * mm});
            skLineSegment(sketch, "E352", {"start": v(27.33, 24.04) * mm, "end": v(27.2, 24.12) * mm});
            skLineSegment(sketch, "E353", {"start": v(-56.18, 45.13) * mm, "end": v(-56.39, 44.63) * mm});
            skLineSegment(sketch, "E354", {"start": v(28.01, 22.74) * mm, "end": v(28.02, 22.87) * mm});
            skLineSegment(sketch, "E355", {"start": v(-115.29, 48.55) * mm, "end": v(-97.67, 36.47) * mm});
            skLineSegment(sketch, "E356", {"start": v(61.73, 42.6) * mm, "end": v(61.64, 41.98) * mm});
            skLineSegment(sketch, "E357", {"start": v(77.7, 35.51) * mm, "end": v(77.5, 36.47) * mm});
            skLineSegment(sketch, "E358", {"start": v(74.9, 47.28) * mm, "end": v(74.5, 47.03) * mm});
            skLineSegment(sketch, "E359", {"start": v(50.75, 29.9) * mm, "end": v(50.92, 29.56) * mm});
            skLineSegment(sketch, "E360", {"start": v(28.6, 9.8) * mm, "end": v(26.22, 20.85) * mm});
            skLineSegment(sketch, "E361", {"start": v(-3.23, 52.93) * mm, "end": v(-42.92, 52.93) * mm});
            skLineSegment(sketch, "E362", {"start": v(69.06, 35.45) * mm, "end": v(68.78, 36.56) * mm});
            skLineSegment(sketch, "E363", {"start": v(68.88, -33.05) * mm, "end": v(74.16, -23.5) * mm});
            skLineSegment(sketch, "E364", {"start": v(70.62, 38.45) * mm, "end": v(70.66, 37.91) * mm});
            skLineSegment(sketch, "E365", {"start": v(98.2, -32.83) * mm, "end": v(97.9, -33.55) * mm});
            skLineSegment(sketch, "E366", {"start": v(105.68, -50.51) * mm, "end": v(106.27, -50.06) * mm});
            skLineSegment(sketch, "E367", {"start": v(76.65, -35.51) * mm, "end": v(79.31, -24.19) * mm});
            skLineSegment(sketch, "E368", {"start": v(78.24, 41.34) * mm, "end": v(78.43, 41.63) * mm});
            skLineSegment(sketch, "E369", {"start": v(27.9, 22.28) * mm, "end": v(27.93, 22.37) * mm});
            skLineSegment(sketch, "E370", {"start": v(-42.92, 52.93) * mm, "end": v(-34.1, 42.57) * mm});
            skLineSegment(sketch, "E371", {"start": v(49.95, 20.56) * mm, "end": v(49.41, 19.65) * mm});
            skLineSegment(sketch, "E372", {"start": v(70.87, 41.67) * mm, "end": v(77.55, 39.74) * mm});
            skLineSegment(sketch, "E373", {"start": v(99.12, -22.65) * mm, "end": v(107.53, -20.23) * mm});
            skLineSegment(sketch, "E374", {"start": v(-114.5, 49.28) * mm, "end": v(-115.29, 48.55) * mm});
            skLineSegment(sketch, "E375", {"start": v(92.14, -53.65) * mm, "end": v(94.5, -53.67) * mm});
            skLineSegment(sketch, "E376", {"start": v(111.6, 48.67) * mm, "end": v(103.17, 50.7) * mm});
            skLineSegment(sketch, "E377", {"start": v(92.7, -35.45) * mm, "end": v(94.98, -33.24) * mm});
            skLineSegment(sketch, "E378", {"start": v(44.77, 15.13) * mm, "end": v(28.01, 23) * mm});
            skLineSegment(sketch, "E379", {"start": v(40.65, 35.76) * mm, "end": v(42.45, 35.3) * mm});
            skLineSegment(sketch, "E380", {"start": v(97.9, -33.55) * mm, "end": v(111.06, -36.03) * mm});
            skLineSegment(sketch, "E381", {"start": v(76.27, 49.92) * mm, "end": v(77.84, 50.29) * mm});
            skLineSegment(sketch, "E382", {"start": v(89.1, -36.72) * mm, "end": v(83.9, -22.96) * mm});
            skLineSegment(sketch, "E383", {"start": v(24.91, 38.9) * mm, "end": v(19, 26.05) * mm});
            skLineSegment(sketch, "E384", {"start": v(99.36, -25.85) * mm, "end": v(99.33, -27.45) * mm});
            skLineSegment(sketch, "E385", {"start": v(89.52, -39.56) * mm, "end": v(88.42, -39.69) * mm});
            skLineSegment(sketch, "E386", {"start": v(-38.65, 25.25) * mm, "end": v(-35.93, 35.6) * mm});
            skLineSegment(sketch, "E387", {"start": v(39.52, 43.17) * mm, "end": v(34.8, 43.31) * mm});
            skLineSegment(sketch, "E388", {"start": v(95.65, -17.76) * mm, "end": v(86.21, -16.87) * mm});
            skLineSegment(sketch, "E389", {"start": v(91.92, 45.16) * mm, "end": v(96.76, 44.76) * mm});
            skLineSegment(sketch, "E390", {"start": v(24.68, 39.06) * mm, "end": v(24.75, 39) * mm});
            skLineSegment(sketch, "E391", {"start": v(70.54, 46.37) * mm, "end": v(67.32, 50.39) * mm});
            skLineSegment(sketch, "E392", {"start": v(85.54, -36.9) * mm, "end": v(82.95, -23.5) * mm});
            skLineSegment(sketch, "E393", {"start": v(87.01, -36.9) * mm, "end": v(83.6, -23.16) * mm});
            skLineSegment(sketch, "E394", {"start": v(96.16, -11.73) * mm, "end": v(100.05, -3.04) * mm});
            skLineSegment(sketch, "E395", {"start": v(30.24, 53.54) * mm, "end": v(35.47, 53.67) * mm});
            skLineSegment(sketch, "E396", {"start": v(3.58, 44.62) * mm, "end": v(4.28, 45.44) * mm});
            skLineSegment(sketch, "E397", {"start": v(38.75, 36.13) * mm, "end": v(27.93, 23.35) * mm});
            skLineSegment(sketch, "E398", {"start": v(24.74, 41.4) * mm, "end": v(24.65, 41.3) * mm});
            skLineSegment(sketch, "E399", {"start": v(77.84, 50.29) * mm, "end": v(77, 53.04) * mm});
            skLineSegment(sketch, "E400", {"start": v(81.47, -23.98) * mm, "end": v(81.07, -24.05) * mm});
            skLineSegment(sketch, "E401", {"start": v(69.7, 45.07) * mm, "end": v(64.69, 48.43) * mm});
            skLineSegment(sketch, "E402", {"start": v(-117.34, 45.73) * mm, "end": v(-117.63, 45.13) * mm});
            skLineSegment(sketch, "E403", {"start": v(90.4, -36.44) * mm, "end": v(91, -36.25) * mm});
            skLineSegment(sketch, "E404", {"start": v(28.01, 23) * mm, "end": v(28, 23.06) * mm});
            skLineSegment(sketch, "E405", {"start": v(64.82, 28.1) * mm, "end": v(67, 23.8) * mm});
            skLineSegment(sketch, "E406", {"start": v(31.7, 43.25) * mm, "end": v(35.47, 53.67) * mm});
            skLineSegment(sketch, "E407", {"start": v(-117.34, 45.73) * mm, "end": v(-118, 44.15) * mm});
            skLineSegment(sketch, "E408", {"start": v(68.47, 39.76) * mm, "end": v(61.64, 38.6) * mm});
            skLineSegment(sketch, "E409", {"start": v(93.84, -6.09) * mm, "end": v(96.16, -11.73) * mm});
            skLineSegment(sketch, "E410", {"start": v(82.47, -36.62) * mm, "end": v(81.47, -23.98) * mm});
            skLineSegment(sketch, "E411", {"start": v(95.66, -32.01) * mm, "end": v(95.94, -31.31) * mm});
            skLineSegment(sketch, "E412", {"start": v(96.75, -26.95) * mm, "end": v(96.79, -25.74) * mm});
            skLineSegment(sketch, "E413", {"start": v(91.6, -39.09) * mm, "end": v(92.14, -53.65) * mm});
            skLineSegment(sketch, "E414", {"start": v(70.87, 41.67) * mm, "end": v(70.76, 41.08) * mm});
            skLineSegment(sketch, "E415", {"start": v(111.1, -37.79) * mm, "end": v(111.06, -36.03) * mm});
            skLineSegment(sketch, "E416", {"start": v(24.31, 39.52) * mm, "end": v(13.5, 27) * mm});
            skLineSegment(sketch, "E417", {"start": v(73.73, 46.45) * mm, "end": v(78.64, 41.9) * mm});
            skLineSegment(sketch, "E418", {"start": v(23.37, 9.32) * mm, "end": v(18.32, 9.16) * mm});
            skLineSegment(sketch, "E419", {"start": v(-56.39, 44.63) * mm, "end": v(-56.54, 44.2) * mm});
            skLineSegment(sketch, "E420", {"start": v(36.19, 11.31) * mm, "end": v(27.8, 22.09) * mm});
            skLineSegment(sketch, "E421", {"start": v(63.04, 46.33) * mm, "end": v(62.78, 45.86) * mm});
            skLineSegment(sketch, "E422", {"start": v(47.25, 33.33) * mm, "end": v(51.35, 24.6) * mm});
            skLineSegment(sketch, "E423", {"start": v(85.68, -20.63) * mm, "end": v(85.53, -21) * mm});
            skLineSegment(sketch, "E424", {"start": v(78.86, 32.26) * mm, "end": v(78.37, 33.4) * mm});
            skLineSegment(sketch, "E425", {"start": v(50.55, 30.21) * mm, "end": v(50.75, 29.9) * mm});
            skLineSegment(sketch, "E426", {"start": v(69.43, 34.3) * mm, "end": v(63.22, 32) * mm});
            skLineSegment(sketch, "E427", {"start": v(77.04, 48.28) * mm, "end": v(76.16, 47.94) * mm});
            skLineSegment(sketch, "E428", {"start": v(-97.67, 36.47) * mm, "end": v(-96.07, 42.57) * mm});
            skLineSegment(sketch, "E429", {"start": v(68.78, 36.56) * mm, "end": v(68.58, 37.63) * mm});
            skLineSegment(sketch, "E430", {"start": v(19, 26.05) * mm, "end": v(13.5, 27) * mm});
            skLineSegment(sketch, "E431", {"start": v(72.75, 48.37) * mm, "end": v(73.4, 48.76) * mm});
            skLineSegment(sketch, "E432", {"start": v(76.65, -35.51) * mm, "end": v(78.36, -24.16) * mm});
            skLineSegment(sketch, "E433", {"start": v(74.02, -34.8) * mm, "end": v(76.34, -23.94) * mm});
            skLineSegment(sketch, "E434", {"start": v(82.37, -39.44) * mm, "end": v(79.77, -38.98) * mm});
            skLineSegment(sketch, "E435", {"start": v(79.3, -36.1) * mm, "end": v(80.21, -24.15) * mm});
            skLineSegment(sketch, "E436", {"start": v(68.52, 40.8) * mm, "end": v(61.64, 41.98) * mm});
            skLineSegment(sketch, "E437", {"start": v(28.6, 9.8) * mm, "end": v(25.63, 20.6) * mm});
            skLineSegment(sketch, "E438", {"start": v(26.75, 21.12) * mm, "end": v(26.99, 21.26) * mm});
            skLineSegment(sketch, "E439", {"start": v(68.88, -33.05) * mm, "end": v(71.85, -22.88) * mm});
            skLineSegment(sketch, "E440", {"start": v(-53.29, 49.1) * mm, "end": v(-35.93, 35.6) * mm});
            skLineSegment(sketch, "E441", {"start": v(48.13, 17.96) * mm, "end": v(47.38, 17.19) * mm});
            skLineSegment(sketch, "E442", {"start": v(93.22, -35.1) * mm, "end": v(94.59, -33.78) * mm});
            skLineSegment(sketch, "E443", {"start": v(24.65, 41.3) * mm, "end": v(19.4, 52.38) * mm});
            skLineSegment(sketch, "E444", {"start": v(-105.13, 52.83) * mm, "end": v(-106.95, 52.6) * mm});
            skLineSegment(sketch, "E445", {"start": v(5.73, 29.47) * mm, "end": v(5.2, 29.77) * mm});
            skLineSegment(sketch, "E446", {"start": v(70.87, 41.67) * mm, "end": v(77.65, 40.09) * mm});
            skLineSegment(sketch, "E447", {"start": v(94.05, 50.02) * mm, "end": v(101, 48.88) * mm});
            skLineSegment(sketch, "E448", {"start": v(96.39, -29.75) * mm, "end": v(84.46, -22.5) * mm});
            skLineSegment(sketch, "E449", {"start": v(47.25, 33.33) * mm, "end": v(47.91, 32.9) * mm});
            skLineSegment(sketch, "E450", {"start": v(41.62, -7.7) * mm, "end": v(18.48, -7.73) * mm});
            skLineSegment(sketch, "E451", {"start": v(111.06, 45.15) * mm, "end": v(101.82, 44.05) * mm});
            skLineSegment(sketch, "E452", {"start": v(42.45, 35.3) * mm, "end": v(47.38, 17.19) * mm});
            skLineSegment(sketch, "E453", {"start": v(27.9, 23.4) * mm, "end": v(27.88, 23.46) * mm});
            skLineSegment(sketch, "E454", {"start": v(24.24, 40.48) * mm, "end": v(14.37, 51.14) * mm});
            skLineSegment(sketch, "E455", {"start": v(96.85, -35.33) * mm, "end": v(96.45, -35.79) * mm});
            skLineSegment(sketch, "E456", {"start": v(44.16, 34.74) * mm, "end": v(48.8, 18.78) * mm});
            skLineSegment(sketch, "E457", {"start": v(43.98, 42.73) * mm, "end": v(39.52, 43.17) * mm});
            skLineSegment(sketch, "E458", {"start": v(25.28, 41.85) * mm, "end": v(22.06, 52.82) * mm});
            skLineSegment(sketch, "E459", {"start": v(83.65, 44.6) * mm, "end": v(84.55, 44.78) * mm});
            skLineSegment(sketch, "E460", {"start": v(70.1, 45.75) * mm, "end": v(66.37, 49.8) * mm});
            skLineSegment(sketch, "E461", {"start": v(-11.35, 25.25) * mm, "end": v(-8.63, 35.6) * mm});
            skLineSegment(sketch, "E462", {"start": v(97.81, -16.61) * mm, "end": v(104.13, -11.65) * mm});
            skLineSegment(sketch, "E463", {"start": v(38.75, 36.13) * mm, "end": v(27.95, 23.3) * mm});
            skLineSegment(sketch, "E464", {"start": v(66.26, -47.78) * mm, "end": v(73.97, -50.27) * mm});
            skLineSegment(sketch, "E465", {"start": v(0.86, 35.58) * mm, "end": v(0.78, 36.2) * mm});
            skLineSegment(sketch, "E466", {"start": v(95.46, -36.78) * mm, "end": v(107.33, -49.06) * mm});
            skLineSegment(sketch, "E467", {"start": v(75.52, 49.68) * mm, "end": v(74.3, 52.69) * mm});
            skLineSegment(sketch, "E468", {"start": v(18.32, 9.16) * mm, "end": v(6.08, 9.65) * mm});
            skLineSegment(sketch, "E469", {"start": v(81.86, -23.89) * mm, "end": v(81.47, -23.98) * mm});
            skLineSegment(sketch, "E470", {"start": v(85.54, -36.9) * mm, "end": v(87.01, -36.9) * mm});
            skLineSegment(sketch, "E471", {"start": v(71.57, 47.47) * mm, "end": v(68.34, 50.9) * mm});
            skLineSegment(sketch, "E472", {"start": v(67, 23.8) * mm, "end": v(69.8, 19.07) * mm});
            skLineSegment(sketch, "E473", {"start": v(68.48, 38.65) * mm, "end": v(61.84, 37.09) * mm});
            skLineSegment(sketch, "E474", {"start": v(91.3, -0.72) * mm, "end": v(93.84, -6.09) * mm});
            skLineSegment(sketch, "E475", {"start": v(81.77, -2.3) * mm, "end": v(83.5, -6.34) * mm});
            skLineSegment(sketch, "E476", {"start": v(24.31, 39.52) * mm, "end": v(24.35, 39.45) * mm});
            skLineSegment(sketch, "E477", {"start": v(96.79, -25.74) * mm, "end": v(96.76, -24.55) * mm});
            skLineSegment(sketch, "E478", {"start": v(111.05, -39.48) * mm, "end": v(111.1, -37.79) * mm});
            skLineSegment(sketch, "E479", {"start": v(24.2, 40.22) * mm, "end": v(24.19, 40.13) * mm});
            skLineSegment(sketch, "E480", {"start": v(24.2, 39.9) * mm, "end": v(10.75, 27.66) * mm});
            skLineSegment(sketch, "E481", {"start": v(26.99, 21.26) * mm, "end": v(27.2, 21.4) * mm});
            skLineSegment(sketch, "E482", {"start": v(-55.56, 46.34) * mm, "end": v(-55.9, 45.7) * mm});
            skLineSegment(sketch, "E483", {"start": v(27.96, 22.47) * mm, "end": v(28, 22.61) * mm});
            skLineSegment(sketch, "E484", {"start": v(62.78, 45.86) * mm, "end": v(62.54, 45.36) * mm});
            skLineSegment(sketch, "E485", {"start": v(3.3, 31.18) * mm, "end": v(2.9, 31.58) * mm});
            skLineSegment(sketch, "E486", {"start": v(91.84, 52.6) * mm, "end": v(85.79, 53.15) * mm});
            skLineSegment(sketch, "E487", {"start": v(85.82, -20.24) * mm, "end": v(85.68, -20.63) * mm});
            skLineSegment(sketch, "E488", {"start": v(68.78, 36.56) * mm, "end": v(62.63, 33.79) * mm});
            skLineSegment(sketch, "E489", {"start": v(31.5, 37.27) * mm, "end": v(38.75, 36.13) * mm});
            skLineSegment(sketch, "E490", {"start": v(74.1, 46.75) * mm, "end": v(73.73, 46.45) * mm});
            skLineSegment(sketch, "E491", {"start": v(-47.89, 52.08) * mm, "end": v(-34.1, 42.57) * mm});
            skLineSegment(sketch, "E492", {"start": v(51.08, 29.22) * mm, "end": v(51.2, 28.86) * mm});
            skLineSegment(sketch, "E493", {"start": v(7.8, 48.21) * mm, "end": v(8.79, 48.8) * mm});
            skLineSegment(sketch, "E494", {"start": v(68.58, 37.63) * mm, "end": v(68.52, 38.14) * mm});
            skLineSegment(sketch, "E495", {"start": v(73.02, 45.8) * mm, "end": v(78.43, 41.63) * mm});
            skLineSegment(sketch, "E496", {"start": v(23.78, 25.25) * mm, "end": v(19, 26.05) * mm});
            skLineSegment(sketch, "E497", {"start": v(70.1, 45.75) * mm, "end": v(70.54, 46.37) * mm});
            skLineSegment(sketch, "E498", {"start": v(25.28, 41.85) * mm, "end": v(25.15, 41.77) * mm});
            skLineSegment(sketch, "E499", {"start": v(71.01, 42.23) * mm, "end": v(70.87, 41.67) * mm});
            skLineSegment(sketch, "E500", {"start": v(68.81, 42.7) * mm, "end": v(62.33, 44.85) * mm});
            skLineSegment(sketch, "E501", {"start": v(24.19, 39.97) * mm, "end": v(8.79, 48.8) * mm});
            skLineSegment(sketch, "E502", {"start": v(68.99, -35.76) * mm, "end": v(57.68, -44.54) * mm});
            skLineSegment(sketch, "E503", {"start": v(-103.12, 52.93) * mm, "end": v(-105.13, 52.83) * mm});
            skLineSegment(sketch, "E504", {"start": v(1, 38.97) * mm, "end": v(1.18, 39.74) * mm});
            skLineSegment(sketch, "E505", {"start": v(82.97, 49.18) * mm, "end": v(83.65, 44.6) * mm});
            skLineSegment(sketch, "E506", {"start": v(121.82, 42.22) * mm, "end": v(111.06, 45.15) * mm});
            skLineSegment(sketch, "E507", {"start": v(27.93, 23.35) * mm, "end": v(27.9, 23.4) * mm});
            skLineSegment(sketch, "E508", {"start": v(24.22, 40.39) * mm, "end": v(12.02, 50.32) * mm});
            skLineSegment(sketch, "E509", {"start": v(87.27, -39.75) * mm, "end": v(86.1, -39.76) * mm});
            skLineSegment(sketch, "E510", {"start": v(24.75, 39) * mm, "end": v(19, 26.05) * mm});
            skLineSegment(sketch, "E511", {"start": v(82.8, 44.37) * mm, "end": v(83.65, 44.6) * mm});
            skLineSegment(sketch, "E512", {"start": v(90.18, 49) * mm, "end": v(89.65, 45.2) * mm});
            skLineSegment(sketch, "E513", {"start": v(50.8, 22.53) * mm, "end": v(50.4, 21.52) * mm});
            skLineSegment(sketch, "E514", {"start": v(-65.54, 9.9) * mm, "end": v(-42.68, 9.9) * mm});
            skLineSegment(sketch, "E515", {"start": v(77.38, 37.38) * mm, "end": v(77.36, 37.8) * mm});
            skLineSegment(sketch, "E516", {"start": v(6.08, 9.65) * mm, "end": v(-5.71, 11.2) * mm});
            skLineSegment(sketch, "E517", {"start": v(80.21, -24.15) * mm, "end": v(79.31, -24.19) * mm});
            skLineSegment(sketch, "E518", {"start": v(96.45, -35.79) * mm, "end": v(110.6, -42.64) * mm});
            skLineSegment(sketch, "E519", {"start": v(-54, 48.4) * mm, "end": v(-54.62, 47.7) * mm});
            skLineSegment(sketch, "E520", {"start": v(91.6, -36.02) * mm, "end": v(92.17, -35.76) * mm});
            skLineSegment(sketch, "E521", {"start": v(34.8, 43.31) * mm, "end": v(35.47, 53.67) * mm});
            skLineSegment(sketch, "E522", {"start": v(68.34, 50.9) * mm, "end": v(67.32, 50.39) * mm});
            skLineSegment(sketch, "E523", {"start": v(69.34, 44.34) * mm, "end": v(63.64, 47.22) * mm});
            skLineSegment(sketch, "E524", {"start": v(97.54, -34.25) * mm, "end": v(97.13, -34.93) * mm});
            skLineSegment(sketch, "E525", {"start": v(97.81, -16.61) * mm, "end": v(98.56, -19.54) * mm});
            skLineSegment(sketch, "E526", {"start": v(24.35, 39.45) * mm, "end": v(24.4, 39.38) * mm});
            skLineSegment(sketch, "E527", {"start": v(83.5, -6.34) * mm, "end": v(84.8, -9.9) * mm});
            skLineSegment(sketch, "E528", {"start": v(99.36, -25.85) * mm, "end": v(108.88, -24.4) * mm});
            skLineSegment(sketch, "E529", {"start": v(-55.56, 46.34) * mm, "end": v(-56.54, 44.2) * mm});
            skLineSegment(sketch, "E530", {"start": v(68.63, 41.78) * mm, "end": v(68.81, 42.7) * mm});
            skLineSegment(sketch, "E531", {"start": v(26, 38.41) * mm, "end": v(23.78, 25.25) * mm});
            skLineSegment(sketch, "E532", {"start": v(27.2, 24.12) * mm, "end": v(27.05, 24.2) * mm});
            skLineSegment(sketch, "E533", {"start": v(105.06, -50.94) * mm, "end": v(105.68, -50.51) * mm});
            skLineSegment(sketch, "E534", {"start": v(24.28, 39.6) * mm, "end": v(13.5, 27) * mm});
            skLineSegment(sketch, "E535", {"start": v(80.68, 49.04) * mm, "end": v(81.26, 43.8) * mm});
            skLineSegment(sketch, "E536", {"start": v(110.92, -34.22) * mm, "end": v(110.68, -32.35) * mm});
            skLineSegment(sketch, "E537", {"start": v(50.55, 30.21) * mm, "end": v(51.08, 29.22) * mm});
            skLineSegment(sketch, "E538", {"start": v(24.32, 40.73) * mm, "end": v(24.28, 40.6) * mm});
            skLineSegment(sketch, "E539", {"start": v(73.02, 45.8) * mm, "end": v(78.24, 41.34) * mm});
            skLineSegment(sketch, "E540", {"start": v(27.2, 21.4) * mm, "end": v(27.39, 21.57) * mm});
            skLineSegment(sketch, "E541", {"start": v(-100.4, 26.11) * mm, "end": v(-72.4, 26.11) * mm});
            skLineSegment(sketch, "E542", {"start": v(94.4, -37.7) * mm, "end": v(105.06, -50.94) * mm});
            skLineSegment(sketch, "E543", {"start": v(61.84, 43.2) * mm, "end": v(61.73, 42.6) * mm});
            skLineSegment(sketch, "E544", {"start": v(2.9, 31.58) * mm, "end": v(2.54, 32) * mm});
            skLineSegment(sketch, "E545", {"start": v(103.17, 50.7) * mm, "end": v(91.84, 52.6) * mm});
            skLineSegment(sketch, "E546", {"start": v(-110.07, 51.8) * mm, "end": v(-96.07, 42.57) * mm});
            skLineSegment(sketch, "E547", {"start": v(38.75, 36.13) * mm, "end": v(27.97, 23.24) * mm});
            skLineSegment(sketch, "E548", {"start": v(38.75, 36.13) * mm, "end": v(40.65, 35.76) * mm});
            skLineSegment(sketch, "E549", {"start": v(85.94, -19.83) * mm, "end": v(85.82, -20.24) * mm});
            skLineSegment(sketch, "E550", {"start": v(77.37, -24.08) * mm, "end": v(76.34, -23.94) * mm});
            skLineSegment(sketch, "E551", {"start": v(78.86, 48.78) * mm, "end": v(77.95, 48.56) * mm});
            skLineSegment(sketch, "E552", {"start": v(94.26, -13.54) * mm, "end": v(92.64, -9.52) * mm});
            skLineSegment(sketch, "E553", {"start": v(93.03, -38.54) * mm, "end": v(96.68, -53.54) * mm});
            skLineSegment(sketch, "E554", {"start": v(31.5, 37.27) * mm, "end": v(27.05, 24.2) * mm});
            skLineSegment(sketch, "E555", {"start": v(71.18, 42.76) * mm, "end": v(71.01, 42.23) * mm});
            skLineSegment(sketch, "E556", {"start": v(106.27, -50.06) * mm, "end": v(106.82, -49.57) * mm});
            skLineSegment(sketch, "E557", {"start": v(27.66, 42.76) * mm, "end": v(26.95, 42.57) * mm});
            skLineSegment(sketch, "E558", {"start": v(24.74, 41.4) * mm, "end": v(19.4, 52.38) * mm});
            skLineSegment(sketch, "E559", {"start": v(87.27, -39.75) * mm, "end": v(86.87, -53.17) * mm});
            skLineSegment(sketch, "E560", {"start": v(-115.29, 48.55) * mm, "end": v(-115.95, 47.82) * mm});
            skLineSegment(sketch, "E561", {"start": v(45.77, 34.1) * mm, "end": v(50.8, 22.53) * mm});
            skLineSegment(sketch, "E562", {"start": v(82.97, 49.18) * mm, "end": v(82.8, 44.37) * mm});
            skLineSegment(sketch, "E563", {"start": v(84.47, 50.78) * mm, "end": v(85.79, 53.15) * mm});
            skLineSegment(sketch, "E564", {"start": v(85.32, 49.22) * mm, "end": v(84.55, 44.78) * mm});
            skLineSegment(sketch, "E565", {"start": v(90.18, 49) * mm, "end": v(87.5, 45.13) * mm});
            skLineSegment(sketch, "E566", {"start": v(49.64, 31.4) * mm, "end": v(50.12, 30.82) * mm});
            skLineSegment(sketch, "E567", {"start": v(59.28, -17.71) * mm, "end": v(49.48, -12.44) * mm});
            skLineSegment(sketch, "E568", {"start": v(74.08, 49.1) * mm, "end": v(74.78, 49.41) * mm});
            skLineSegment(sketch, "E569", {"start": v(86.1, -39.76) * mm, "end": v(84.88, -39.7) * mm});
            skLineSegment(sketch, "E570", {"start": v(82, 44.1) * mm, "end": v(82.8, 44.37) * mm});
            skLineSegment(sketch, "E571", {"start": v(90.4, -36.44) * mm, "end": v(83.9, -22.96) * mm});
            skLineSegment(sketch, "E572", {"start": v(95.22, 48.42) * mm, "end": v(91.92, 45.16) * mm});
            skLineSegment(sketch, "E573", {"start": v(51.12, 23.58) * mm, "end": v(50.8, 22.53) * mm});
            skLineSegment(sketch, "E574", {"start": v(-35.93, 35.6) * mm, "end": v(-34.1, 42.57) * mm});
            skLineSegment(sketch, "E575", {"start": v(35.47, 53.67) * mm, "end": v(45.3, 53.27) * mm});
            skLineSegment(sketch, "E576", {"start": v(25.15, 41.77) * mm, "end": v(22.06, 52.82) * mm});
            skLineSegment(sketch, "E577", {"start": v(77.36, 37.8) * mm, "end": v(77.35, 38.22) * mm});
            skLineSegment(sketch, "E578", {"start": v(3.3, 31.18) * mm, "end": v(0.87, 38.23) * mm});
            skLineSegment(sketch, "E579", {"start": v(24.37, 40.85) * mm, "end": v(24.32, 40.73) * mm});
            skLineSegment(sketch, "E580", {"start": v(50.12, 30.82) * mm, "end": v(51.55, 26.45) * mm});
            skLineSegment(sketch, "E581", {"start": v(74.78, 49.41) * mm, "end": v(74.3, 52.69) * mm});
            skLineSegment(sketch, "E582", {"start": v(-117.63, 45.13) * mm, "end": v(-117.85, 44.6) * mm});
            skLineSegment(sketch, "E583", {"start": v(91, -36.25) * mm, "end": v(91.6, -36.02) * mm});
            skLineSegment(sketch, "E584", {"start": v(96.45, -35.79) * mm, "end": v(110.2, -44.1) * mm});
            skLineSegment(sketch, "E585", {"start": v(28, 23.06) * mm, "end": v(28, 23.12) * mm});
            skLineSegment(sketch, "E586", {"start": v(64.69, 48.43) * mm, "end": v(64.31, 48.05) * mm});
            skLineSegment(sketch, "E587", {"start": v(69.05, 43.54) * mm, "end": v(63.33, 46.79) * mm});
            skLineSegment(sketch, "E588", {"start": v(97.13, -34.93) * mm, "end": v(97, -35.12) * mm});
            skLineSegment(sketch, "E589", {"start": v(73.94, 29.26) * mm, "end": v(85.72, 9.45) * mm});
            skLineSegment(sketch, "E590", {"start": v(68.52, 38.14) * mm, "end": v(61.84, 37.09) * mm});
            skLineSegment(sketch, "E591", {"start": v(24.25, 39.66) * mm, "end": v(24.28, 39.6) * mm});
            skLineSegment(sketch, "E592", {"start": v(74.02, -34.8) * mm, "end": v(77.37, -24.08) * mm});
            skLineSegment(sketch, "E593", {"start": v(95.94, -31.31) * mm, "end": v(96.18, -30.56) * mm});
            skLineSegment(sketch, "E594", {"start": v(104.4, -51.34) * mm, "end": v(105.06, -50.94) * mm});
            skLineSegment(sketch, "E595", {"start": v(98.2, -32.83) * mm, "end": v(110.92, -34.22) * mm});
            skLineSegment(sketch, "E596", {"start": v(1.18, 39.74) * mm, "end": v(1.5, 40.82) * mm});
            skLineSegment(sketch, "E597", {"start": v(24.2, 39.82) * mm, "end": v(10.75, 27.66) * mm});
            skLineSegment(sketch, "E598", {"start": v(110.6, -42.64) * mm, "end": v(110.88, -41.1) * mm});
            skLineSegment(sketch, "E599", {"start": v(110.68, -32.35) * mm, "end": v(109.94, -28.46) * mm});
            skLineSegment(sketch, "E600", {"start": v(-116.5, 47.1) * mm, "end": v(-97.67, 36.47) * mm});
            skLineSegment(sketch, "E601", {"start": v(28.6, 9.8) * mm, "end": v(23.37, 9.32) * mm});
            skLineSegment(sketch, "E602", {"start": v(84.94, -21.96) * mm, "end": v(84.7, -22.24) * mm});
            skLineSegment(sketch, "E603", {"start": v(-111.4, 51.26) * mm, "end": v(-97.67, 36.47) * mm});
            skLineSegment(sketch, "E604", {"start": v(84.03, -36.8) * mm, "end": v(82.6, -23.65) * mm});
            skLineSegment(sketch, "E605", {"start": v(-46.39, 52.47) * mm, "end": v(-47.89, 52.08) * mm});
            skLineSegment(sketch, "E606", {"start": v(-112, 50.96) * mm, "end": v(-112.57, 50.65) * mm});
            skLineSegment(sketch, "E607", {"start": v(61.64, 38.6) * mm, "end": v(61.84, 37.09) * mm});
            skLineSegment(sketch, "E608", {"start": v(82.79, 53.26) * mm, "end": v(79.85, 53.23) * mm});
            skLineSegment(sketch, "E609", {"start": v(2.54, 32) * mm, "end": v(2.2, 32.45) * mm});
            skLineSegment(sketch, "E610", {"start": v(26, 38.41) * mm, "end": v(28.44, 37.8) * mm});
            skLineSegment(sketch, "E611", {"start": v(85.53, -21) * mm, "end": v(85.35, -21.34) * mm});
            skLineSegment(sketch, "E612", {"start": v(77.95, 48.56) * mm, "end": v(77.04, 48.28) * mm});
            skLineSegment(sketch, "E613", {"start": v(31.22, 10.19) * mm, "end": v(26.99, 21.26) * mm});
            skLineSegment(sketch, "E614", {"start": v(93.48, -38.32) * mm, "end": v(98.69, -53.28) * mm});
            skLineSegment(sketch, "E615", {"start": v(73.89, 25.15) * mm, "end": v(71.46, 29.62) * mm});
            skLineSegment(sketch, "E616", {"start": v(70.76, 41.08) * mm, "end": v(70.68, 40.46) * mm});
            skLineSegment(sketch, "E617", {"start": v(31.5, 37.27) * mm, "end": v(27.2, 24.12) * mm});
            skLineSegment(sketch, "E618", {"start": v(79.65, 42.86) * mm, "end": v(79.94, 43.07) * mm});
            skLineSegment(sketch, "E619", {"start": v(70.62, 38.45) * mm, "end": v(77.37, 38.62) * mm});
            skLineSegment(sketch, "E620", {"start": v(26.22, 20.85) * mm, "end": v(26.75, 21.12) * mm});
            skLineSegment(sketch, "E621", {"start": v(77.65, 40.09) * mm, "end": v(77.77, 40.42) * mm});
            skLineSegment(sketch, "E622", {"start": v(71.01, 42.23) * mm, "end": v(77.77, 40.42) * mm});
            skLineSegment(sketch, "E623", {"start": v(44.16, 34.74) * mm, "end": v(50.4, 21.52) * mm});
            skLineSegment(sketch, "E624", {"start": v(72.4, 45.05) * mm, "end": v(78.07, 41.05) * mm});
            skLineSegment(sketch, "E625", {"start": v(87.7, 50.66) * mm, "end": v(91.84, 52.6) * mm});
            skLineSegment(sketch, "E626", {"start": v(84.47, 50.78) * mm, "end": v(82.79, 53.26) * mm});
            skLineSegment(sketch, "E627", {"start": v(24.68, 39.06) * mm, "end": v(19, 26.05) * mm});
            skLineSegment(sketch, "E628", {"start": v(49.1, 31.93) * mm, "end": v(49.64, 31.4) * mm});
            skLineSegment(sketch, "E629", {"start": v(49.48, -12.44) * mm, "end": v(41.62, -7.7) * mm});
            skLineSegment(sketch, "E630", {"start": v(100.4, 47.55) * mm, "end": v(96.76, 44.76) * mm});
            skLineSegment(sketch, "E631", {"start": v(25.63, 24.77) * mm, "end": v(24.76, 25.02) * mm});
            skLineSegment(sketch, "E632", {"start": v(73.4, 48.76) * mm, "end": v(74.08, 49.1) * mm});
            skLineSegment(sketch, "E633", {"start": v(28.42, 42.91) * mm, "end": v(27.66, 42.76) * mm});
            skLineSegment(sketch, "E634", {"start": v(84.88, -39.7) * mm, "end": v(82.37, -39.44) * mm});
            skLineSegment(sketch, "E635", {"start": v(96.67, -27.95) * mm, "end": v(84.46, -22.5) * mm});
            skLineSegment(sketch, "E636", {"start": v(24.44, 39.32) * mm, "end": v(24.5, 39.25) * mm});
            skLineSegment(sketch, "E637", {"start": v(51.35, 24.6) * mm, "end": v(51.12, 23.58) * mm});
            skLineSegment(sketch, "E638", {"start": v(-8.63, 35.6) * mm, "end": v(-35.93, 35.6) * mm});
            skLineSegment(sketch, "E639", {"start": v(73.97, -50.27) * mm, "end": v(80.82, -52.06) * mm});
            skLineSegment(sketch, "E640", {"start": v(77.35, 38.22) * mm, "end": v(77.37, 38.62) * mm});
            skLineSegment(sketch, "E641", {"start": v(24.43, 40.97) * mm, "end": v(24.37, 40.85) * mm});
            skLineSegment(sketch, "E642", {"start": v(-2.79, 22.35) * mm, "end": v(-0.6, 21.69) * mm});
            skLineSegment(sketch, "E643", {"start": v(82.95, -23.5) * mm, "end": v(82.6, -23.65) * mm});
            skLineSegment(sketch, "E644", {"start": v(-117.85, 44.6) * mm, "end": v(-118, 44.15) * mm});
            skLineSegment(sketch, "E645", {"start": v(87.01, -36.9) * mm, "end": v(88.42, -36.81) * mm});
            skLineSegment(sketch, "E646", {"start": v(27.97, 23.24) * mm, "end": v(27.95, 23.3) * mm});
            skLineSegment(sketch, "E647", {"start": v(61.84, 37.09) * mm, "end": v(62.17, 35.48) * mm});
            skLineSegment(sketch, "E648", {"start": v(97, -35.12) * mm, "end": v(96.85, -35.33) * mm});
            skLineSegment(sketch, "E649", {"start": v(71.57, 47.47) * mm, "end": v(69.42, 51.38) * mm});
            skLineSegment(sketch, "E650", {"start": v(8.12, 28.45) * mm, "end": v(1.91, 41.85) * mm});
            skLineSegment(sketch, "E651", {"start": v(99.12, -22.65) * mm, "end": v(99.28, -24.25) * mm});
            skLineSegment(sketch, "E652", {"start": v(85.66, -13.01) * mm, "end": v(85.94, -14.4) * mm});
            skLineSegment(sketch, "E653", {"start": v(68.47, 39.76) * mm, "end": v(68.52, 40.8) * mm});
            skLineSegment(sketch, "E654", {"start": v(24.25, 39.66) * mm, "end": v(13.5, 27) * mm});
            skLineSegment(sketch, "E655", {"start": v(1.5, 40.82) * mm, "end": v(1.91, 41.85) * mm});
            skLineSegment(sketch, "E656", {"start": v(109.94, -28.46) * mm, "end": v(108.88, -24.4) * mm});
            skLineSegment(sketch, "E657", {"start": v(69.34, 44.34) * mm, "end": v(64.31, 48.05) * mm});
            skLineSegment(sketch, "E658", {"start": v(95.46, -36.78) * mm, "end": v(105.06, -50.94) * mm});
            skLineSegment(sketch, "E659", {"start": v(27.47, 21.65) * mm, "end": v(27.55, 21.73) * mm});
            skLineSegment(sketch, "E660", {"start": v(-47.89, 52.08) * mm, "end": v(-49.23, 51.6) * mm});
            skLineSegment(sketch, "E661", {"start": v(92.64, -9.52) * mm, "end": v(85.94, -14.4) * mm});
            skLineSegment(sketch, "E662", {"start": v(50.55, 30.21) * mm, "end": v(51.32, 28.5) * mm});
            skLineSegment(sketch, "E663", {"start": v(64.31, 48.05) * mm, "end": v(63.96, 47.64) * mm});
            skLineSegment(sketch, "E664", {"start": v(91.03, 13.04) * mm, "end": v(82.86, 25.51) * mm});
            skLineSegment(sketch, "E665", {"start": v(94.4, -37.7) * mm, "end": v(103.7, -51.7) * mm});
            skLineSegment(sketch, "E666", {"start": v(74.5, 47.03) * mm, "end": v(74.1, 46.75) * mm});
            skLineSegment(sketch, "E667", {"start": v(96.18, -19.96) * mm, "end": v(95.65, -17.76) * mm});
            skLineSegment(sketch, "E668", {"start": v(31.22, 10.19) * mm, "end": v(26.75, 21.12) * mm});
            skLineSegment(sketch, "E669", {"start": v(71.84, 33.68) * mm, "end": v(77.7, 35.51) * mm});
            skLineSegment(sketch, "E670", {"start": v(88.42, -39.69) * mm, "end": v(86.87, -53.17) * mm});
            skLineSegment(sketch, "E671", {"start": v(71.6, 43.75) * mm, "end": v(71.37, 43.27) * mm});
            skLineSegment(sketch, "E672", {"start": v(107.33, -49.06) * mm, "end": v(107.8, -48.53) * mm});
            skLineSegment(sketch, "E673", {"start": v(78.43, 41.63) * mm, "end": v(78.64, 41.9) * mm});
            skLineSegment(sketch, "E674", {"start": v(68.58, 37.63) * mm, "end": v(62.17, 35.48) * mm});
            skLineSegment(sketch, "E675", {"start": v(72.89, 31.28) * mm, "end": v(77.99, 34.49) * mm});
            skLineSegment(sketch, "E676", {"start": v(-54.62, 47.7) * mm, "end": v(-35.93, 35.6) * mm});
            skLineSegment(sketch, "E677", {"start": v(24.83, 41.5) * mm, "end": v(19.4, 52.38) * mm});
            skLineSegment(sketch, "E678", {"start": v(114.9, 47.73) * mm, "end": v(111.6, 48.67) * mm});
            skLineSegment(sketch, "E679", {"start": v(68.63, 41.78) * mm, "end": v(61.84, 43.2) * mm});
            skLineSegment(sketch, "E680", {"start": v(42.45, 35.3) * mm, "end": v(44.16, 34.74) * mm});
            skLineSegment(sketch, "E681", {"start": v(94.05, 50.02) * mm, "end": v(103.17, 50.7) * mm});
            skLineSegment(sketch, "E682", {"start": v(127, 38.07) * mm, "end": v(121.82, 42.22) * mm});
            skLineSegment(sketch, "E683", {"start": v(24.32, 40.73) * mm, "end": v(14.37, 51.14) * mm});
            skLineSegment(sketch, "E684", {"start": v(16.85, 51.82) * mm, "end": v(19.4, 52.38) * mm});
            skLineSegment(sketch, "E685", {"start": v(75.52, 49.68) * mm, "end": v(76.27, 49.92) * mm});
            skLineSegment(sketch, "E686", {"start": v(26.4, 24.5) * mm, "end": v(25.63, 24.77) * mm});
            skLineSegment(sketch, "E687", {"start": v(88.42, -39.69) * mm, "end": v(87.27, -39.75) * mm});
            skLineSegment(sketch, "E688", {"start": v(30.02, 43.14) * mm, "end": v(28.42, 42.91) * mm});
            skLineSegment(sketch, "E689", {"start": v(89.65, 45.2) * mm, "end": v(91.92, 45.16) * mm});
            skLineSegment(sketch, "E690", {"start": v(24.5, 39.25) * mm, "end": v(24.55, 39.19) * mm});
            skLineSegment(sketch, "E691", {"start": v(44.77, 15.13) * mm, "end": v(42.84, 13.96) * mm});
            skLineSegment(sketch, "E692", {"start": v(-56.54, 44.2) * mm, "end": v(-65.54, 9.9) * mm});
            skLineSegment(sketch, "E693", {"start": v(-111.4, 51.26) * mm, "end": v(-112, 50.96) * mm});
            skLineSegment(sketch, "E694", {"start": v(37.7, -35.67) * mm, "end": v(57.68, -44.54) * mm});
            skLineSegment(sketch, "E695", {"start": v(3.74, 30.8) * mm, "end": v(3.3, 31.18) * mm});
            skLineSegment(sketch, "E696", {"start": v(96.56, -22.22) * mm, "end": v(85.68, -20.63) * mm});
            skLineSegment(sketch, "E697", {"start": v(96.45, -35.79) * mm, "end": v(109.68, -45.48) * mm});
            skLineSegment(sketch, "E698", {"start": v(30.02, 43.14) * mm, "end": v(30.24, 53.54) * mm});
            skLineSegment(sketch, "E699", {"start": v(83.29, -23.34) * mm, "end": v(82.95, -23.5) * mm});
            skLineSegment(sketch, "E700", {"start": v(99.28, -24.25) * mm, "end": v(107.53, -20.23) * mm});
            skLineSegment(sketch, "E701", {"start": v(-53.29, 49.1) * mm, "end": v(-54, 48.4) * mm});
            skLineSegment(sketch, "E702", {"start": v(94.16, -34.26) * mm, "end": v(94.59, -33.78) * mm});
            skLineSegment(sketch, "E703", {"start": v(62.17, 35.48) * mm, "end": v(62.63, 33.79) * mm});
            skLineSegment(sketch, "E704", {"start": v(27.98, 23.18) * mm, "end": v(27.97, 23.24) * mm});
            skLineSegment(sketch, "E705", {"start": v(74.08, 49.1) * mm, "end": v(74.3, 52.69) * mm});
            skLineSegment(sketch, "E706", {"start": v(97.9, -33.55) * mm, "end": v(97.54, -34.25) * mm});
            skLineSegment(sketch, "E707", {"start": v(6.87, 28.92) * mm, "end": v(1.5, 40.82) * mm});
            skLineSegment(sketch, "E708", {"start": v(72.14, 47.94) * mm, "end": v(70.56, 51.78) * mm});
            skLineSegment(sketch, "E709", {"start": v(121.82, 42.22) * mm, "end": v(111.92, 42) * mm});
            skLineSegment(sketch, "E710", {"start": v(98.56, -19.54) * mm, "end": v(99.12, -22.65) * mm});
            skLineSegment(sketch, "E711", {"start": v(91.3, -0.72) * mm, "end": v(91.03, 13.04) * mm});
            skLineSegment(sketch, "E712", {"start": v(51.47, 27.71) * mm, "end": v(51.52, 27.3) * mm});
            skLineSegment(sketch, "E713", {"start": v(68.52, 40.8) * mm, "end": v(68.63, 41.78) * mm});
            skLineSegment(sketch, "E714", {"start": v(28.44, 37.8) * mm, "end": v(24.76, 25.02) * mm});
            skLineSegment(sketch, "E715", {"start": v(50.12, 30.82) * mm, "end": v(51.52, 27.3) * mm});
            skLineSegment(sketch, "E716", {"start": v(102.97, -52.05) * mm, "end": v(103.7, -51.7) * mm});
            skLineSegment(sketch, "E717", {"start": v(0.87, 38.23) * mm, "end": v(1, 38.97) * mm});
            skLineSegment(sketch, "E718", {"start": v(91.6, -39.09) * mm, "end": v(90.59, -39.36) * mm});
            skLineSegment(sketch, "E719", {"start": v(24.28, 40.6) * mm, "end": v(24.24, 40.48) * mm});
            skLineSegment(sketch, "E720", {"start": v(33.75, 10.69) * mm, "end": v(31.22, 10.19) * mm});
            skLineSegment(sketch, "E721", {"start": v(-101.93, 20.25) * mm, "end": v(-100.4, 26.11) * mm});
            skLineSegment(sketch, "E722", {"start": v(76.65, -35.51) * mm, "end": v(79.3, -36.1) * mm});
            skLineSegment(sketch, "E723", {"start": v(63.96, 47.64) * mm, "end": v(63.64, 47.22) * mm});
            skLineSegment(sketch, "E724", {"start": v(1.9, 32.91) * mm, "end": v(1.61, 33.4) * mm});
            skLineSegment(sketch, "E725", {"start": v(78.37, 33.4) * mm, "end": v(77.99, 34.49) * mm});
            skLineSegment(sketch, "E726", {"start": v(93.68, -38.2) * mm, "end": v(98.69, -53.28) * mm});
            skLineSegment(sketch, "E727", {"start": v(92.64, -9.52) * mm, "end": v(85.66, -13.01) * mm});
            skLineSegment(sketch, "E728", {"start": v(86.17, -18.46) * mm, "end": v(86.12, -18.94) * mm});
            skLineSegment(sketch, "E729", {"start": v(76.34, -23.94) * mm, "end": v(74.16, -23.5) * mm});
            skLineSegment(sketch, "E730", {"start": v(95.65, -17.76) * mm, "end": v(94.26, -13.54) * mm});
            skLineSegment(sketch, "E731", {"start": v(71.84, 33.68) * mm, "end": v(77.5, 36.47) * mm});
            skLineSegment(sketch, "E732", {"start": v(72.14, 47.94) * mm, "end": v(72.75, 48.37) * mm});
            skLineSegment(sketch, "E733", {"start": v(28.6, 9.8) * mm, "end": v(24.97, 20.39) * mm});
            skLineSegment(sketch, "E734", {"start": v(26.95, 42.57) * mm, "end": v(26.3, 42.34) * mm});
            skLineSegment(sketch, "E735", {"start": v(70.62, 39.82) * mm, "end": v(70.6, 39.15) * mm});
            skLineSegment(sketch, "E736", {"start": v(106.82, -49.57) * mm, "end": v(107.33, -49.06) * mm});
            skLineSegment(sketch, "E737", {"start": v(80.25, 43.27) * mm, "end": v(80.57, 43.46) * mm});
            skLineSegment(sketch, "E738", {"start": v(23.37, 9.32) * mm, "end": v(22.65, 19.88) * mm});
            skLineSegment(sketch, "E739", {"start": v(24.97, 20.39) * mm, "end": v(25.63, 20.6) * mm});
            skLineSegment(sketch, "E740", {"start": v(31.5, 37.27) * mm, "end": v(26.4, 24.5) * mm});
            skLineSegment(sketch, "E741", {"start": v(48.8, 18.78) * mm, "end": v(48.13, 17.96) * mm});
            skLineSegment(sketch, "E742", {"start": v(6.08, 9.65) * mm, "end": v(6.64, 20.22) * mm});
            skLineSegment(sketch, "E743", {"start": v(1.61, 33.4) * mm, "end": v(0.79, 37.52) * mm});
            skLineSegment(sketch, "E744", {"start": v(118.87, 44.55) * mm, "end": v(114.9, 47.73) * mm});
            skLineSegment(sketch, "E745", {"start": v(44.16, 34.74) * mm, "end": v(45.77, 34.1) * mm});
            skLineSegment(sketch, "E746", {"start": v(90.18, 49) * mm, "end": v(85.32, 49.22) * mm});
            skLineSegment(sketch, "E747", {"start": v(18.32, 9.16) * mm, "end": v(16.95, 19.51) * mm});
            skLineSegment(sketch, "E748", {"start": v(14.37, 51.14) * mm, "end": v(16.85, 51.82) * mm});
            skLineSegment(sketch, "E749", {"start": v(93.7, -34.7) * mm, "end": v(94.16, -34.26) * mm});
            skLineSegment(sketch, "E750", {"start": v(24.61, 39.12) * mm, "end": v(19, 26.05) * mm});
            skLineSegment(sketch, "E751", {"start": v(77.95, 48.56) * mm, "end": v(80.57, 43.46) * mm});
            skLineSegment(sketch, "E752", {"start": v(27.05, 24.2) * mm, "end": v(26.4, 24.5) * mm});
            skLineSegment(sketch, "E753", {"start": v(71.46, 29.62) * mm, "end": v(67, 23.8) * mm});
            skLineSegment(sketch, "E754", {"start": v(24.55, 39.19) * mm, "end": v(24.61, 39.12) * mm});
            skLineSegment(sketch, "E755", {"start": v(-5.71, 11.2) * mm, "end": v(-0.6, 21.69) * mm});
            skLineSegment(sketch, "E756", {"start": v(-110.07, 51.8) * mm, "end": v(-111.4, 51.26) * mm});
            skLineSegment(sketch, "E757", {"start": v(86.87, -53.17) * mm, "end": v(89.6, -53.49) * mm});
            skLineSegment(sketch, "E758", {"start": v(4.2, 30.44) * mm, "end": v(1, 38.97) * mm});
            skLineSegment(sketch, "E759", {"start": v(24.57, 41.2) * mm, "end": v(24.5, 41.08) * mm});
            skLineSegment(sketch, "E760", {"start": v(74.5, 47.03) * mm, "end": v(78.64, 41.9) * mm});
            skLineSegment(sketch, "E761", {"start": v(85.32, 49.22) * mm, "end": v(85.49, 44.93) * mm});
            skLineSegment(sketch, "E762", {"start": v(49.64, 31.4) * mm, "end": v(51.49, 25.55) * mm});
            skLineSegment(sketch, "E763", {"start": v(28, 23.12) * mm, "end": v(27.98, 23.18) * mm});
            skLineSegment(sketch, "E764", {"start": v(65.08, 48.8) * mm, "end": v(64.69, 48.43) * mm});
            skLineSegment(sketch, "E765", {"start": v(85.72, 9.45) * mm, "end": v(91.3, -0.72) * mm});
            skLineSegment(sketch, "E766", {"start": v(50.55, 30.21) * mm, "end": v(51.47, 27.71) * mm});
            skLineSegment(sketch, "E767", {"start": v(8.12, 28.45) * mm, "end": v(2.95, 43.75) * mm});
            skLineSegment(sketch, "E768", {"start": v(68.52, 38.14) * mm, "end": v(68.48, 38.65) * mm});
            skLineSegment(sketch, "E769", {"start": v(93.84, -6.09) * mm, "end": v(100.05, -3.04) * mm});
            skLineSegment(sketch, "E770", {"start": v(2.4, 42.83) * mm, "end": v(2.95, 43.75) * mm});
            skLineSegment(sketch, "E771", {"start": v(110.88, -41.1) * mm, "end": v(111.05, -39.48) * mm});
            skLineSegment(sketch, "E772", {"start": v(59.24, -29.13) * mm, "end": v(42.43, -21.02) * mm});
            skLineSegment(sketch, "E773", {"start": v(31.22, 10.19) * mm, "end": v(28.6, 9.8) * mm});
            skLineSegment(sketch, "E774", {"start": v(84.7, -22.24) * mm, "end": v(84.46, -22.5) * mm});
            skLineSegment(sketch, "E775", {"start": v(-127, 9.9) * mm, "end": v(-74.79, 9.9) * mm});
            skLineSegment(sketch, "E776", {"start": v(61.55, 40.02) * mm, "end": v(61.64, 38.6) * mm});
            skLineSegment(sketch, "E777", {"start": v(92.64, -9.52) * mm, "end": v(84.8, -9.9) * mm});
            skLineSegment(sketch, "E778", {"start": v(86.2, -17.95) * mm, "end": v(86.17, -18.46) * mm});
            skLineSegment(sketch, "E779", {"start": v(84.88, -39.7) * mm, "end": v(86.87, -53.17) * mm});
            skLineSegment(sketch, "E780", {"start": v(28.42, 42.91) * mm, "end": v(24.8, 53.15) * mm});
            skLineSegment(sketch, "E781", {"start": v(50.92, 29.56) * mm, "end": v(51.08, 29.22) * mm});
            skLineSegment(sketch, "E782", {"start": v(70.6, 39.15) * mm, "end": v(77.41, 39) * mm});
            skLineSegment(sketch, "E783", {"start": v(94.4, -37.7) * mm, "end": v(102.2, -52.36) * mm});
            skLineSegment(sketch, "E784", {"start": v(96.76, -24.55) * mm, "end": v(96.56, -22.22) * mm});
            skLineSegment(sketch, "E785", {"start": v(71.57, 47.47) * mm, "end": v(72.14, 47.94) * mm});
            skLineSegment(sketch, "E786", {"start": v(25.5, 38.58) * mm, "end": v(23.78, 25.25) * mm});
            skLineSegment(sketch, "E787", {"start": v(70.68, 40.46) * mm, "end": v(70.62, 39.82) * mm});
            skLineSegment(sketch, "E788", {"start": v(79.94, 43.07) * mm, "end": v(80.25, 43.27) * mm});
            skLineSegment(sketch, "E789", {"start": v(25.63, 20.6) * mm, "end": v(26.22, 20.85) * mm});
            skLineSegment(sketch, "E790", {"start": v(70.62, 38.45) * mm, "end": v(77.35, 38.22) * mm});
            skLineSegment(sketch, "E791", {"start": v(-50.44, 51.05) * mm, "end": v(-51.51, 50.44) * mm});
            skLineSegment(sketch, "E792", {"start": v(59.28, -17.71) * mm, "end": v(42.43, -21.02) * mm});
            skLineSegment(sketch, "E793", {"start": v(72.4, 45.05) * mm, "end": v(78.24, 41.34) * mm});
            skLineSegment(sketch, "E794", {"start": v(68.63, 41.78) * mm, "end": v(61.64, 41.98) * mm});
            skLineSegment(sketch, "E795", {"start": v(28.6, 9.8) * mm, "end": v(24.25, 20.2) * mm});
            skLineSegment(sketch, "E796", {"start": v(24.93, 41.6) * mm, "end": v(19.4, 52.38) * mm});
            skLineSegment(sketch, "E797", {"start": v(92.64, -9.52) * mm, "end": v(88.9, -1.4) * mm});
            skLineSegment(sketch, "E798", {"start": v(114.25, 45.83) * mm, "end": v(118.87, 44.55) * mm});
            skLineSegment(sketch, "E799", {"start": v(24.23, 39.74) * mm, "end": v(13.5, 27) * mm});
            skLineSegment(sketch, "E800", {"start": v(18.32, 9.16) * mm, "end": v(11.8, 19.7) * mm});
            skLineSegment(sketch, "E801", {"start": v(45.77, 34.1) * mm, "end": v(46.53, 33.73) * mm});
            skLineSegment(sketch, "E802", {"start": v(85.32, 49.22) * mm, "end": v(82.97, 49.18) * mm});
            skLineSegment(sketch, "E803", {"start": v(5.73, 29.47) * mm, "end": v(1.18, 39.74) * mm});
            skLineSegment(sketch, "E804", {"start": v(93.22, -35.1) * mm, "end": v(93.7, -34.7) * mm});
            skLineSegment(sketch, "E805", {"start": v(24.28, 40.6) * mm, "end": v(14.37, 51.14) * mm});
            skLineSegment(sketch, "E806", {"start": v(78.86, 48.78) * mm, "end": v(81.26, 43.8) * mm});
            skLineSegment(sketch, "E807", {"start": v(12.02, 50.32) * mm, "end": v(14.37, 51.14) * mm});
            skLineSegment(sketch, "E808", {"start": v(24.76, 25.02) * mm, "end": v(23.78, 25.25) * mm});
            skLineSegment(sketch, "E809", {"start": v(96.75, -26.95) * mm, "end": v(84.7, -22.24) * mm});
            skLineSegment(sketch, "E810", {"start": v(74.4, -37.6) * mm, "end": v(68.99, -35.76) * mm});
            skLineSegment(sketch, "E811", {"start": v(-56.54, 44.2) * mm, "end": v(-38.65, 25.25) * mm});
            skLineSegment(sketch, "E812", {"start": v(34.8, 43.31) * mm, "end": v(31.7, 43.25) * mm});
            skLineSegment(sketch, "E813", {"start": v(6.08, 9.65) * mm, "end": v(1.69, 21.1) * mm});
            skLineSegment(sketch, "E814", {"start": v(-112.57, 50.65) * mm, "end": v(-113.1, 50.32) * mm});
            skLineSegment(sketch, "E815", {"start": v(91.6, -36.02) * mm, "end": v(83.9, -22.96) * mm});
            skLineSegment(sketch, "E816", {"start": v(31.5, 37.27) * mm, "end": v(27.56, 23.86) * mm});
            skLineSegment(sketch, "E817", {"start": v(4.68, 30.1) * mm, "end": v(4.2, 30.44) * mm});
            skLineSegment(sketch, "E818", {"start": v(80.82, -52.06) * mm, "end": v(86.87, -53.17) * mm});
            skLineSegment(sketch, "E819", {"start": v(77.95, 48.56) * mm, "end": v(80.25, 43.27) * mm});
            skLineSegment(sketch, "E820", {"start": v(95.46, -36.78) * mm, "end": v(109.68, -45.48) * mm});
            skLineSegment(sketch, "E821", {"start": v(77.47, 39.38) * mm, "end": v(77.55, 39.74) * mm});
            skLineSegment(sketch, "E822", {"start": v(-5.71, 11.2) * mm, "end": v(-2.79, 22.35) * mm});
            skLineSegment(sketch, "E823", {"start": v(27.95, 23.3) * mm, "end": v(27.93, 23.35) * mm});
            skLineSegment(sketch, "E824", {"start": v(63.22, 32) * mm, "end": v(64.82, 28.1) * mm});
            skLineSegment(sketch, "E825", {"start": v(95.46, -36.78) * mm, "end": v(94.4, -37.7) * mm});
            skLineSegment(sketch, "E826", {"start": v(84.8, -9.9) * mm, "end": v(85.66, -13.01) * mm});
            skLineSegment(sketch, "E827", {"start": v(127, 38.07) * mm, "end": v(111.92, 42) * mm});
            skLineSegment(sketch, "E828", {"start": v(96.85, -35.33) * mm, "end": v(110.88, -41.1) * mm});
            skLineSegment(sketch, "E829", {"start": v(74.02, -34.8) * mm, "end": v(76.65, -35.51) * mm});
            skLineSegment(sketch, "E830", {"start": v(4.2, 30.44) * mm, "end": v(0.87, 38.23) * mm});
            skLineSegment(sketch, "E831", {"start": v(40.76, 12.93) * mm, "end": v(38.54, 12.05) * mm});
            skLineSegment(sketch, "E832", {"start": v(19.4, 52.38) * mm, "end": v(22.06, 52.82) * mm});
            skLineSegment(sketch, "E833", {"start": v(0.76, 36.84) * mm, "end": v(0.79, 37.52) * mm});
            skLineSegment(sketch, "E834", {"start": v(104.13, -11.65) * mm, "end": v(100.05, -3.04) * mm});
            skLineSegment(sketch, "E835", {"start": v(24.22, 40.39) * mm, "end": v(24.2, 40.3) * mm});
            skLineSegment(sketch, "E836", {"start": v(109.37, -46.14) * mm, "end": v(109.68, -45.48) * mm});
            skLineSegment(sketch, "E837", {"start": v(-112.57, 50.65) * mm, "end": v(-97.67, 36.47) * mm});
            skLineSegment(sketch, "E838", {"start": v(27.39, 21.57) * mm, "end": v(27.47, 21.65) * mm});
            skLineSegment(sketch, "E839", {"start": v(83.9, -22.96) * mm, "end": v(83.6, -23.16) * mm});
            skLineSegment(sketch, "E840", {"start": v(-100.4, 26.11) * mm, "end": v(-97.67, 36.47) * mm});
            skLineSegment(sketch, "E841", {"start": v(-74.79, 9.9) * mm, "end": v(-72.07, 20.25) * mm});
            skLineSegment(sketch, "E842", {"start": v(1.15, 34.43) * mm, "end": v(0.98, 34.99) * mm});
            skLineSegment(sketch, "E843", {"start": v(-66.8, 42.57) * mm, "end": v(-96.07, 42.57) * mm});
            skLineSegment(sketch, "E844", {"start": v(63.33, 46.79) * mm, "end": v(63.04, 46.33) * mm});
            skLineSegment(sketch, "E845", {"start": v(24.19, 39.97) * mm, "end": v(24.2, 39.9) * mm});
            skLineSegment(sketch, "E846", {"start": v(71.85, -22.88) * mm, "end": v(69.44, -22.1) * mm});
            skLineSegment(sketch, "E847", {"start": v(51.54, 26.89) * mm, "end": v(51.55, 26.45) * mm});
            skLineSegment(sketch, "E848", {"start": v(43.98, 42.73) * mm, "end": v(45.3, 53.27) * mm});
            skLineSegment(sketch, "E849", {"start": v(68.81, 42.7) * mm, "end": v(69.05, 43.54) * mm});
            skLineSegment(sketch, "E850", {"start": v(1.15, 34.43) * mm, "end": v(0.78, 36.2) * mm});
            skLineSegment(sketch, "E851", {"start": v(71.37, 43.27) * mm, "end": v(71.18, 42.76) * mm});
            skLineSegment(sketch, "E852", {"start": v(25.68, 42.08) * mm, "end": v(25.4, 41.93) * mm});
            skLineSegment(sketch, "E853", {"start": v(81.26, 43.8) * mm, "end": v(82, 44.1) * mm});
            skLineSegment(sketch, "E854", {"start": v(-51.51, 50.44) * mm, "end": v(-52.46, 49.79) * mm});
            skLineSegment(sketch, "E855", {"start": v(33.75, 10.69) * mm, "end": v(27.2, 21.4) * mm});
            skLineSegment(sketch, "E856", {"start": v(72.89, 31.28) * mm, "end": v(78.37, 33.4) * mm});
            skLineSegment(sketch, "E857", {"start": v(88.9, -1.4) * mm, "end": v(84.8, 6.3) * mm});
            skLineSegment(sketch, "E858", {"start": v(71.76, 52.14) * mm, "end": v(70.56, 51.78) * mm});
            skLineSegment(sketch, "E859", {"start": v(71.37, 43.27) * mm, "end": v(77.77, 40.42) * mm});
            skLineSegment(sketch, "E860", {"start": v(25.1, 38.78) * mm, "end": v(25.29, 38.68) * mm});
            skLineSegment(sketch, "E861", {"start": v(82.97, 49.18) * mm, "end": v(80.68, 49.04) * mm});
            skLineSegment(sketch, "E862", {"start": v(114.25, 45.83) * mm, "end": v(111.6, 48.67) * mm});
            skLineSegment(sketch, "E863", {"start": v(68.81, 42.7) * mm, "end": v(61.98, 43.76) * mm});
            skLineSegment(sketch, "E864", {"start": v(13.5, 27) * mm, "end": v(10.75, 27.66) * mm});
            skLineSegment(sketch, "E865", {"start": v(68.99, -35.76) * mm, "end": v(63.75, -33.69) * mm});
            skLineSegment(sketch, "E866", {"start": v(95.22, 48.42) * mm, "end": v(90.18, 49) * mm});
            skLineSegment(sketch, "E867", {"start": v(-106.95, 52.6) * mm, "end": v(-108.6, 52.25) * mm});
            skLineSegment(sketch, "E868", {"start": v(-13.74, -7.7) * mm, "end": v(37.7, -35.67) * mm});
            skLineSegment(sketch, "E869", {"start": v(77.95, 48.56) * mm, "end": v(79.94, 43.07) * mm});
            skLineSegment(sketch, "E870", {"start": v(4.2, 30.44) * mm, "end": v(3.74, 30.8) * mm});
            skLineSegment(sketch, "E871", {"start": v(81.13, 50.7) * mm, "end": v(84.47, 50.78) * mm});
            skLineSegment(sketch, "E872", {"start": v(77.55, 39.74) * mm, "end": v(77.65, 40.09) * mm});
            skLineSegment(sketch, "E873", {"start": v(85.72, 9.45) * mm, "end": v(82.86, 25.51) * mm});
            skLineSegment(sketch, "E874", {"start": v(24.37, 40.85) * mm, "end": v(16.85, 51.82) * mm});
            skLineSegment(sketch, "E875", {"start": v(27.66, 42.76) * mm, "end": v(24.8, 53.15) * mm});
            skLineSegment(sketch, "E876", {"start": v(42.45, 35.3) * mm, "end": v(28, 23.12) * mm});
            skLineSegment(sketch, "E877", {"start": v(11.8, 19.7) * mm, "end": v(16.95, 19.51) * mm});
            skLineSegment(sketch, "E878", {"start": v(94.59, -33.78) * mm, "end": v(94.98, -33.24) * mm});
            skLineSegment(sketch, "E879", {"start": v(27.88, 23.46) * mm, "end": v(27.85, 23.51) * mm});
            skLineSegment(sketch, "E880", {"start": v(66.37, 49.8) * mm, "end": v(65.49, 49.15) * mm});
            skLineSegment(sketch, "E881", {"start": v(94.4, -37.7) * mm, "end": v(93.9, -38.06) * mm});
            skLineSegment(sketch, "E882", {"start": v(24.28, 39.6) * mm, "end": v(24.31, 39.52) * mm});
            skLineSegment(sketch, "E883", {"start": v(86.12, -15.69) * mm, "end": v(86.21, -16.87) * mm});
            skLineSegment(sketch, "E884", {"start": v(73.4, 48.76) * mm, "end": v(71.76, 52.14) * mm});
            skLineSegment(sketch, "E885", {"start": v(42.84, 13.96) * mm, "end": v(40.76, 12.93) * mm});
            skLineSegment(sketch, "E886", {"start": v(68.88, -33.05) * mm, "end": v(74.02, -34.8) * mm});
            skLineSegment(sketch, "E887", {"start": v(99.33, -27.45) * mm, "end": v(108.88, -24.4) * mm});
            skLineSegment(sketch, "E888", {"start": v(24.55, 39.19) * mm, "end": v(19, 26.05) * mm});
            skLineSegment(sketch, "E889", {"start": v(103.7, -51.7) * mm, "end": v(104.4, -51.34) * mm});
            skLineSegment(sketch, "E890", {"start": v(8.12, 28.45) * mm, "end": v(4.28, 45.44) * mm});
            skLineSegment(sketch, "E891", {"start": v(0.79, 37.52) * mm, "end": v(0.87, 38.23) * mm});
            skLineSegment(sketch, "E892", {"start": v(72.7, 45.43) * mm, "end": v(72.4, 45.05) * mm});
            skLineSegment(sketch, "E893", {"start": v(100.05, -3.04) * mm, "end": v(91.03, 13.04) * mm});
            skLineSegment(sketch, "E894", {"start": v(92.57, -38.74) * mm, "end": v(91.6, -39.09) * mm});
            skLineSegment(sketch, "E895", {"start": v(24.24, 40.48) * mm, "end": v(24.22, 40.39) * mm});
            skLineSegment(sketch, "E896", {"start": v(84.19, -22.74) * mm, "end": v(83.9, -22.96) * mm});
            skLineSegment(sketch, "E897", {"start": v(79.37, 42.63) * mm, "end": v(79.65, 42.86) * mm});
            skLineSegment(sketch, "E898", {"start": v(-72.07, 20.25) * mm, "end": v(-101.93, 20.25) * mm});
            skLineSegment(sketch, "E899", {"start": v(79.3, -36.1) * mm, "end": v(82.47, -36.62) * mm});
            skLineSegment(sketch, "E900", {"start": v(61.64, 41.98) * mm, "end": v(61.58, 41.35) * mm});
            skLineSegment(sketch, "E901", {"start": v(-117.34, 45.73) * mm, "end": v(-97.67, 36.47) * mm});
            skLineSegment(sketch, "E902", {"start": v(2.2, 32.45) * mm, "end": v(1.9, 32.91) * mm});
            skLineSegment(sketch, "E903", {"start": v(85.79, 53.15) * mm, "end": v(82.79, 53.26) * mm});
            skLineSegment(sketch, "E904", {"start": v(28.44, 37.8) * mm, "end": v(31.5, 37.27) * mm});
            skLineSegment(sketch, "E905", {"start": v(51.52, 27.3) * mm, "end": v(51.54, 26.89) * mm});
            skLineSegment(sketch, "E906", {"start": v(74.16, -23.5) * mm, "end": v(71.85, -22.88) * mm});
            skLineSegment(sketch, "E907", {"start": v(69.05, 43.54) * mm, "end": v(69.34, 44.34) * mm});
            skLineSegment(sketch, "E908", {"start": v(91.6, -36.02) * mm, "end": v(95.34, -32.65) * mm});
            skLineSegment(sketch, "E909", {"start": v(26.3, 42.34) * mm, "end": v(25.68, 42.08) * mm});
            skLineSegment(sketch, "E910", {"start": v(109.03, -46.77) * mm, "end": v(109.37, -46.14) * mm});
            skLineSegment(sketch, "E911", {"start": v(77.77, 40.42) * mm, "end": v(77.9, 40.74) * mm});
            skLineSegment(sketch, "E912", {"start": v(86.1, -39.76) * mm, "end": v(86.87, -53.17) * mm});
            skLineSegment(sketch, "E913", {"start": v(1.37, 33.9) * mm, "end": v(0.76, 36.84) * mm});
            skLineSegment(sketch, "E914", {"start": v(25.74, 38.5) * mm, "end": v(23.78, 25.25) * mm});
            skLineSegment(sketch, "E915", {"start": v(49.48, -12.44) * mm, "end": v(42.43, -21.02) * mm});
            skLineSegment(sketch, "E916", {"start": v(-52.46, 49.79) * mm, "end": v(-53.29, 49.1) * mm});
            skLineSegment(sketch, "E917", {"start": v(84.8, 6.3) * mm, "end": v(76.03, 21.47) * mm});
            skLineSegment(sketch, "E918", {"start": v(96.76, -24.55) * mm, "end": v(85.35, -21.34) * mm});
            skLineSegment(sketch, "E919", {"start": v(33.75, 10.69) * mm, "end": v(27.39, 21.57) * mm});
            skLineSegment(sketch, "E920", {"start": v(-49.23, 51.6) * mm, "end": v(-35.93, 35.6) * mm});
            skLineSegment(sketch, "E921", {"start": v(8.79, 48.8) * mm, "end": v(9.82, 49.35) * mm});
            skLineSegment(sketch, "E922", {"start": v(-55.56, 46.34) * mm, "end": v(-35.93, 35.6) * mm});
            skLineSegment(sketch, "E923", {"start": v(92.17, -35.76) * mm, "end": v(92.7, -35.45) * mm});
            skLineSegment(sketch, "E924", {"start": v(27.45, 23.95) * mm, "end": v(27.33, 24.04) * mm});
            skLineSegment(sketch, "E925", {"start": v(71, 36.17) * mm, "end": v(71.38, 34.93) * mm});
            skLineSegment(sketch, "E926", {"start": v(70.35, 31.97) * mm, "end": v(64.82, 28.1) * mm});
            skLineSegment(sketch, "E927", {"start": v(27.75, 22) * mm, "end": v(27.8, 22.09) * mm});
            skLineSegment(sketch, "E928", {"start": v(-113.6, 49.98) * mm, "end": v(-114.5, 49.28) * mm});
            skLineSegment(sketch, "E929", {"start": v(54.65, -29.66) * mm, "end": v(33.3, -19.22) * mm});
            skLineSegment(sketch, "E930", {"start": v(40.65, 35.76) * mm, "end": v(27.98, 23.18) * mm});
            skLineSegment(sketch, "E931", {"start": v(96.18, -19.96) * mm, "end": v(85.94, -19.83) * mm});
            skLineSegment(sketch, "E932", {"start": v(24.5, 41.08) * mm, "end": v(24.43, 40.97) * mm});
            skLineSegment(sketch, "E933", {"start": v(77.37, 38.62) * mm, "end": v(77.41, 39) * mm});
            skLineSegment(sketch, "E934", {"start": v(42.45, 35.3) * mm, "end": v(28, 23.06) * mm});
            skLineSegment(sketch, "E935", {"start": v(25.04, 41.68) * mm, "end": v(19.4, 52.38) * mm});
            skLineSegment(sketch, "E936", {"start": v(71.84, 44.2) * mm, "end": v(77.9, 40.74) * mm});
            skLineSegment(sketch, "E937", {"start": v(99.19, -29.03) * mm, "end": v(109.94, -28.46) * mm});
            skLineSegment(sketch, "E938", {"start": v(31.5, 37.27) * mm, "end": v(27.33, 24.04) * mm});
            skLineSegment(sketch, "E939", {"start": v(16.95, 19.51) * mm, "end": v(20.87, 19.67) * mm});
            skLineSegment(sketch, "E940", {"start": v(18.32, 9.16) * mm, "end": v(20.87, 19.67) * mm});
            skLineSegment(sketch, "E941", {"start": v(65.49, 49.15) * mm, "end": v(65.08, 48.8) * mm});
            skLineSegment(sketch, "E942", {"start": v(98.9, -30.58) * mm, "end": v(98.71, -31.34) * mm});
            skLineSegment(sketch, "E943", {"start": v(24.75, 39) * mm, "end": v(24.91, 38.9) * mm});
            skLineSegment(sketch, "E944", {"start": v(36.19, 11.31) * mm, "end": v(33.75, 10.69) * mm});
            skLineSegment(sketch, "E945", {"start": v(24.8, 53.15) * mm, "end": v(30.24, 53.54) * mm});
            skLineSegment(sketch, "E946", {"start": v(98.69, -53.28) * mm, "end": v(100.52, -52.88) * mm});
            skLineSegment(sketch, "E947", {"start": v(1.91, 41.85) * mm, "end": v(2.4, 42.83) * mm});
            skLineSegment(sketch, "E948", {"start": v(93.68, -38.2) * mm, "end": v(93.48, -38.32) * mm});
            skLineSegment(sketch, "E949", {"start": v(72.4, 45.05) * mm, "end": v(72.1, 44.64) * mm});
            skLineSegment(sketch, "E950", {"start": v(108.88, -24.4) * mm, "end": v(107.53, -20.23) * mm});
            skLineSegment(sketch, "E951", {"start": v(79.11, 42.4) * mm, "end": v(79.37, 42.63) * mm});
            skLineSegment(sketch, "E952", {"start": v(1.15, 34.43) * mm, "end": v(0.86, 35.58) * mm});
            skLineSegment(sketch, "E953", {"start": v(84.46, -22.5) * mm, "end": v(84.19, -22.74) * mm});
            skLineSegment(sketch, "E954", {"start": v(-118, 44.15) * mm, "end": v(-127, 9.9) * mm});
            skLineSegment(sketch, "E955", {"start": v(94.26, -13.54) * mm, "end": v(86.12, -15.69) * mm});
            skLineSegment(sketch, "E956", {"start": v(61.58, 41.35) * mm, "end": v(61.55, 40.02) * mm});
            skLineSegment(sketch, "E957", {"start": v(1.06, 34.7) * mm, "end": v(0.98, 34.99) * mm});
            skLineSegment(sketch, "E958", {"start": v(82.86, 25.51) * mm, "end": v(80.93, 28.42) * mm});
            skLineSegment(sketch, "E959", {"start": v(71, 36.17) * mm, "end": v(77.5, 36.47) * mm});
            skLineSegment(sketch, "E960", {"start": v(51.49, 25.55) * mm, "end": v(51.35, 24.6) * mm});
            skLineSegment(sketch, "E961", {"start": v(39.52, 43.17) * mm, "end": v(45.3, 53.27) * mm});
            skLineSegment(sketch, "E962", {"start": v(64.42, -20.1) * mm, "end": v(59.28, -17.71) * mm});
            skLineSegment(sketch, "E963", {"start": v(82.37, -39.44) * mm, "end": v(80.82, -52.06) * mm});
            skLineSegment(sketch, "E964", {"start": v(69.34, 44.34) * mm, "end": v(69.7, 45.07) * mm});
            skLineSegment(sketch, "E965", {"start": v(88.9, -1.4) * mm, "end": v(83.5, -6.34) * mm});
            skLineSegment(sketch, "E966", {"start": v(108.65, -47.38) * mm, "end": v(109.03, -46.77) * mm});
            skLineSegment(sketch, "E967", {"start": v(77.9, 40.74) * mm, "end": v(78.07, 41.05) * mm});
            skLineSegment(sketch, "E968", {"start": v(2.2, 32.45) * mm, "end": v(0.79, 37.52) * mm});
            skLineSegment(sketch, "E969", {"start": v(71, 36.17) * mm, "end": v(77.38, 37.38) * mm});
            skLineSegment(sketch, "E970", {"start": v(-49.23, 51.6) * mm, "end": v(-50.44, 51.05) * mm});
            skLineSegment(sketch, "E971", {"start": v(28.02, 22.94) * mm, "end": v(28.01, 23) * mm});
            skLineSegment(sketch, "E972", {"start": v(33.75, 10.69) * mm, "end": v(27.47, 21.65) * mm});
            skLineSegment(sketch, "E973", {"start": v(79.78, 48.94) * mm, "end": v(78.86, 48.78) * mm});
            skLineSegment(sketch, "E974", {"start": v(27.56, 23.86) * mm, "end": v(27.45, 23.95) * mm});
            skLineSegment(sketch, "E975", {"start": v(74.78, 49.41) * mm, "end": v(75.52, 49.68) * mm});
            skLineSegment(sketch, "E976", {"start": v(70.75, 37.35) * mm, "end": v(71, 36.17) * mm});
            skLineSegment(sketch, "E977", {"start": v(31.7, 43.25) * mm, "end": v(30.02, 43.14) * mm});
            skLineSegment(sketch, "E978", {"start": v(27.8, 22.09) * mm, "end": v(27.85, 22.18) * mm});
            skLineSegment(sketch, "E979", {"start": v(111.06, 45.15) * mm, "end": v(100.4, 47.55) * mm});
            skLineSegment(sketch, "E980", {"start": v(95.94, -31.31) * mm, "end": v(84.19, -22.74) * mm});
            skLineSegment(sketch, "E981", {"start": v(-113.1, 50.32) * mm, "end": v(-113.6, 49.98) * mm});
            skLineSegment(sketch, "E982", {"start": v(33.3, -19.22) * mm, "end": v(13, -7.71) * mm});
            skLineSegment(sketch, "E983", {"start": v(87.7, 50.66) * mm, "end": v(94.05, 50.02) * mm});
            skLineSegment(sketch, "E984", {"start": v(96.68, -53.54) * mm, "end": v(98.69, -53.28) * mm});
            skLineSegment(sketch, "E985", {"start": v(38.75, 36.13) * mm, "end": v(27.65, 23.77) * mm});
            skLineSegment(sketch, "E986", {"start": v(71.84, 44.2) * mm, "end": v(78.07, 41.05) * mm});
            skLineSegment(sketch, "E987", {"start": v(101, 48.88) * mm, "end": v(111.6, 48.67) * mm});
            skLineSegment(sketch, "E988", {"start": v(47.91, 32.9) * mm, "end": v(48.53, 32.43) * mm});
            skLineSegment(sketch, "E989", {"start": v(5.2, 29.77) * mm, "end": v(1, 38.97) * mm});
            skLineSegment(sketch, "E990", {"start": v(26.95, 42.57) * mm, "end": v(24.8, 53.15) * mm});
            skLineSegment(sketch, "E991", {"start": v(20.87, 19.67) * mm, "end": v(22.65, 19.88) * mm});
            skLineSegment(sketch, "E992", {"start": v(24.43, 40.97) * mm, "end": v(16.85, 51.82) * mm});
            skLineSegment(sketch, "E993", {"start": v(31.5, 37.27) * mm, "end": v(27.45, 23.95) * mm});
            skLineSegment(sketch, "E994", {"start": v(95.34, -32.65) * mm, "end": v(95.66, -32.01) * mm});
            skLineSegment(sketch, "E995", {"start": v(62.63, 33.79) * mm, "end": v(63.22, 32) * mm});
            skLineSegment(sketch, "E996", {"start": v(99.19, -29.03) * mm, "end": v(98.9, -30.58) * mm});
            skLineSegment(sketch, "E997", {"start": v(-74.74, 32.9) * mm, "end": v(-76.4, 32.61) * mm});
            skLineSegment(sketch, "E998", {"start": v(-72.68, -9.96) * mm, "end": v(-68.65, 5.4) * mm});
            skLineSegment(sketch, "E999", {"start": v(-84.62, 27.84) * mm, "end": v(-85.14, 27.15) * mm});
            skLineSegment(sketch, "E1000", {"start": v(-35.95, 22.72) * mm, "end": v(-64.1, 22.72) * mm});
            skLineSegment(sketch, "E1001", {"start": v(-85.14, 27.15) * mm, "end": v(-85.56, 26.48) * mm});
            skLineSegment(sketch, "E1002", {"start": v(-72.92, 33.08) * mm, "end": v(-74.74, 32.9) * mm});
            skLineSegment(sketch, "E1003", {"start": v(-68.65, 5.4) * mm, "end": v(-41.35, 5.4) * mm});
            skLineSegment(sketch, "E1004", {"start": v(-85.91, 25.86) * mm, "end": v(-86.19, 25.28) * mm});
            skLineSegment(sketch, "E1005", {"start": v(-35.95, 22.72) * mm, "end": v(-33.23, 33.08) * mm});
            skLineSegment(sketch, "E1006", {"start": v(-86.19, 25.28) * mm, "end": v(-86.4, 24.77) * mm});
            skLineSegment(sketch, "E1007", {"start": v(-33.23, 33.08) * mm, "end": v(-72.92, 33.08) * mm});
            skLineSegment(sketch, "E1008", {"start": v(-86.4, 24.77) * mm, "end": v(-86.54, 24.34) * mm});
            skLineSegment(sketch, "E1009", {"start": v(-41.35, 5.4) * mm, "end": v(-38.63, 15.75) * mm});
            skLineSegment(sketch, "E1010", {"start": v(-85.56, 26.48) * mm, "end": v(-85.91, 25.86) * mm});
            skLineSegment(sketch, "E1011", {"start": v(-95.55, -9.96) * mm, "end": v(-72.68, -9.96) * mm});
            skLineSegment(sketch, "E1012", {"start": v(-84, 28.55) * mm, "end": v(-84.62, 27.84) * mm});
            skLineSegment(sketch, "E1013", {"start": v(-65.93, 15.75) * mm, "end": v(-64.1, 22.72) * mm});
            skLineSegment(sketch, "E1014", {"start": v(-76.4, 32.61) * mm, "end": v(-77.9, 32.22) * mm});
            skLineSegment(sketch, "E1015", {"start": v(-38.63, 15.75) * mm, "end": v(-65.93, 15.75) * mm});
            skLineSegment(sketch, "E1016", {"start": v(-77.9, 32.22) * mm, "end": v(-79.24, 31.75) * mm});
            skLineSegment(sketch, "E1017", {"start": v(-86.54, 24.34) * mm, "end": v(-95.55, -9.96) * mm});
            skLineSegment(sketch, "E1018", {"start": v(-83.3, 29.25) * mm, "end": v(-84, 28.55) * mm});
            skLineSegment(sketch, "E1019", {"start": v(-80.45, 31.2) * mm, "end": v(-81.52, 30.59) * mm});
            skLineSegment(sketch, "E1020", {"start": v(-81.52, 30.59) * mm, "end": v(-82.46, 29.94) * mm});
            skLineSegment(sketch, "E1021", {"start": v(-82.46, 29.94) * mm, "end": v(-83.3, 29.25) * mm});
            skLineSegment(sketch, "E1022", {"start": v(-79.24, 31.75) * mm, "end": v(-80.45, 31.2) * mm});
            skSolve(sketch);
        }
        {
            var Q0;
            Q0=makeQuery(id+"F15.imprint","IMPRINT",FACE,{"disambiguationData":[TD([[makeQuery(id+"F15.imprint","IMPRINT",EDGE,{"derivedFrom":sQuery(id+"F15.wireOp",EDGE,"E64")}),1.0]])]});
            var sketch = newSketch(context, id + "F16", { "sketchPlane" : qUnion([Q0])});
            skLineSegment(sketch, "E1023.0", {"start": v(-64.09, 52.93) * mm, "end": v(-103.12, 52.93) * mm});
            skLineSegment(sketch, "E1024.0", {"start": v(-66.8, 42.57) * mm, "end": v(-64.09, 52.93) * mm});
            skLineSegment(sketch, "E1025.0", {"start": v(-97.67, 36.47) * mm, "end": v(-96.07, 42.57) * mm});
            skLineSegment(sketch, "E1026.0", {"start": v(-69.69, 36.47) * mm, "end": v(-97.67, 36.47) * mm});
            skLineSegment(sketch, "E1027.0", {"start": v(-72.4, 26.11) * mm, "end": v(-69.69, 36.47) * mm});
            skLineSegment(sketch, "E1028.0", {"start": v(-100.4, 26.11) * mm, "end": v(-72.4, 26.11) * mm});
            skLineSegment(sketch, "E1029.0", {"start": v(-72.07, 20.25) * mm, "end": v(-101.93, 20.25) * mm});
            skLineSegment(sketch, "E1030.0", {"start": v(-101.93, 20.25) * mm, "end": v(-100.4, 26.11) * mm});
            skLineSegment(sketch, "E1031.0", {"start": v(-74.79, 9.9) * mm, "end": v(-72.07, 20.25) * mm});
            skLineSegment(sketch, "E1032.0", {"start": v(-127, 9.9) * mm, "end": v(-74.79, 9.9) * mm});
            skLineSegment(sketch, "E1033.0", {"start": v(-118, 44.15) * mm, "end": v(-127, 9.9) * mm});
            skLineSegment(sketch, "E1034.0", {"start": v(-117.85, 44.6) * mm, "end": v(-118, 44.15) * mm});
            skLineSegment(sketch, "E1035.0", {"start": v(-117.63, 45.13) * mm, "end": v(-117.85, 44.6) * mm});
            skLineSegment(sketch, "E1036.0", {"start": v(-117.34, 45.73) * mm, "end": v(-117.63, 45.13) * mm});
            skLineSegment(sketch, "E1037.0", {"start": v(-116.97, 46.4) * mm, "end": v(-117.34, 45.73) * mm});
            skLineSegment(sketch, "E1038.0", {"start": v(-116.5, 47.1) * mm, "end": v(-116.97, 46.4) * mm});
            skLineSegment(sketch, "E1039.0", {"start": v(-115.95, 47.82) * mm, "end": v(-116.5, 47.1) * mm});
            skLineSegment(sketch, "E1040.0", {"start": v(-115.29, 48.55) * mm, "end": v(-115.95, 47.82) * mm});
            skLineSegment(sketch, "E1041.0", {"start": v(-114.5, 49.28) * mm, "end": v(-115.29, 48.55) * mm});
            skLineSegment(sketch, "E1042.0", {"start": v(-113.6, 49.98) * mm, "end": v(-114.5, 49.28) * mm});
            skLineSegment(sketch, "E1043.0", {"start": v(-113.1, 50.32) * mm, "end": v(-113.6, 49.98) * mm});
            skLineSegment(sketch, "E1044.0", {"start": v(-112.57, 50.65) * mm, "end": v(-113.1, 50.32) * mm});
            skLineSegment(sketch, "E1045.0", {"start": v(-112, 50.96) * mm, "end": v(-112.57, 50.65) * mm});
            skLineSegment(sketch, "E1046.0", {"start": v(-111.4, 51.26) * mm, "end": v(-112, 50.96) * mm});
            skLineSegment(sketch, "E1047.0", {"start": v(-110.07, 51.8) * mm, "end": v(-111.4, 51.26) * mm});
            skLineSegment(sketch, "E1048.0", {"start": v(-108.6, 52.25) * mm, "end": v(-110.07, 51.8) * mm});
            skLineSegment(sketch, "E1049.0", {"start": v(-106.95, 52.6) * mm, "end": v(-108.6, 52.25) * mm});
            skLineSegment(sketch, "E1050.0", {"start": v(-105.13, 52.83) * mm, "end": v(-106.95, 52.6) * mm});
            skLineSegment(sketch, "E1051.0", {"start": v(-103.12, 52.93) * mm, "end": v(-105.13, 52.83) * mm});
            skLineSegment(sketch, "E1052.0", {"start": v(-66.8, 42.57) * mm, "end": v(-96.07, 42.57) * mm});
            skLineSegment(sketch, "E1053", {"start": v(-44.91, 52.69) * mm, "end": v(-46.57, 52.4) * mm});
            skLineSegment(sketch, "E1054", {"start": v(-42.86, 9.83) * mm, "end": v(-38.83, 25.18) * mm});
            skLineSegment(sketch, "E1055", {"start": v(-54.8, 47.63) * mm, "end": v(-55.31, 46.93) * mm});
            skLineSegment(sketch, "E1056", {"start": v(-6.13, 42.5) * mm, "end": v(-34.28, 42.5) * mm});
            skLineSegment(sketch, "E1057", {"start": v(-55.31, 46.93) * mm, "end": v(-55.74, 46.27) * mm});
            skLineSegment(sketch, "E1058", {"start": v(-43.1, 52.86) * mm, "end": v(-44.91, 52.69) * mm});
            skLineSegment(sketch, "E1059", {"start": v(-38.83, 25.18) * mm, "end": v(-11.53, 25.18) * mm});
            skLineSegment(sketch, "E1060", {"start": v(-56.09, 45.64) * mm, "end": v(-56.36, 45.06) * mm});
            skLineSegment(sketch, "E1061", {"start": v(-6.13, 42.5) * mm, "end": v(-3.4, 52.86) * mm});
            skLineSegment(sketch, "E1062", {"start": v(-56.36, 45.06) * mm, "end": v(-56.57, 44.55) * mm});
            skLineSegment(sketch, "E1063", {"start": v(-3.4, 52.86) * mm, "end": v(-43.1, 52.86) * mm});
            skLineSegment(sketch, "E1064", {"start": v(-56.57, 44.55) * mm, "end": v(-56.72, 44.13) * mm});
            skLineSegment(sketch, "E1065", {"start": v(-11.53, 25.18) * mm, "end": v(-8.8, 35.53) * mm});
            skLineSegment(sketch, "E1066", {"start": v(-55.74, 46.27) * mm, "end": v(-56.09, 45.64) * mm});
            skLineSegment(sketch, "E1067", {"start": v(-65.72, 9.83) * mm, "end": v(-42.86, 9.83) * mm});
            skLineSegment(sketch, "E1068", {"start": v(-54.18, 48.33) * mm, "end": v(-54.8, 47.63) * mm});
            skLineSegment(sketch, "E1069", {"start": v(-36.1, 35.53) * mm, "end": v(-34.28, 42.5) * mm});
            skLineSegment(sketch, "E1070", {"start": v(-46.57, 52.4) * mm, "end": v(-48.07, 52) * mm});
            skLineSegment(sketch, "E1071", {"start": v(-8.8, 35.53) * mm, "end": v(-36.1, 35.53) * mm});
            skLineSegment(sketch, "E1072", {"start": v(-48.07, 52) * mm, "end": v(-49.41, 51.53) * mm});
            skLineSegment(sketch, "E1073", {"start": v(-56.72, 44.13) * mm, "end": v(-65.72, 9.83) * mm});
            skLineSegment(sketch, "E1074", {"start": v(-53.47, 49.03) * mm, "end": v(-54.18, 48.33) * mm});
            skLineSegment(sketch, "E1075", {"start": v(-50.62, 50.98) * mm, "end": v(-51.7, 50.37) * mm});
            skLineSegment(sketch, "E1076", {"start": v(-51.7, 50.37) * mm, "end": v(-52.64, 49.72) * mm});
            skLineSegment(sketch, "E1077", {"start": v(-52.64, 49.72) * mm, "end": v(-53.47, 49.03) * mm});
            skLineSegment(sketch, "E1078", {"start": v(-49.41, 51.53) * mm, "end": v(-50.62, 50.98) * mm});
            skLineSegment(sketch, "E1079", {"start": v(24.63, 38.67) * mm, "end": v(24.8, 38.57) * mm});
            skLineSegment(sketch, "E1080", {"start": v(45.4, 15.56) * mm, "end": v(44.5, 14.92) * mm});
            skLineSegment(sketch, "E1081", {"start": v(21.77, 52.6) * mm, "end": v(24.5, 52.93) * mm});
            skLineSegment(sketch, "E1082", {"start": v(4.78, 46) * mm, "end": v(5.64, 46.7) * mm});
            skLineSegment(sketch, "E1083", {"start": v(24.65, 41.38) * mm, "end": v(24.55, 41.28) * mm});
            skLineSegment(sketch, "E1084", {"start": v(51.12, 27.9) * mm, "end": v(51.19, 27.5) * mm});
            skLineSegment(sketch, "E1085", {"start": v(27.73, 22.66) * mm, "end": v(27.73, 22.72) * mm});
            skLineSegment(sketch, "E1086", {"start": v(10.47, 27.44) * mm, "end": v(7.83, 28.24) * mm});
            skLineSegment(sketch, "E1087", {"start": v(27.57, 21.97) * mm, "end": v(27.61, 22.06) * mm});
            skLineSegment(sketch, "E1088", {"start": v(48.25, 32.22) * mm, "end": v(48.82, 31.71) * mm});
            skLineSegment(sketch, "E1089", {"start": v(6.35, 20) * mm, "end": v(11.53, 19.48) * mm});
            skLineSegment(sketch, "E1090", {"start": v(27.56, 23.3) * mm, "end": v(27.53, 23.35) * mm});
            skLineSegment(sketch, "E1091", {"start": v(51.6, 40.94) * mm, "end": v(47.84, 41.82) * mm});
            skLineSegment(sketch, "E1092", {"start": v(24.33, 38.9) * mm, "end": v(24.4, 38.85) * mm});
            skLineSegment(sketch, "E1093", {"start": v(46.28, 16.25) * mm, "end": v(45.4, 15.56) * mm});
            skLineSegment(sketch, "E1094", {"start": v(0.7, 34.77) * mm, "end": v(0.63, 35.06) * mm});
            skLineSegment(sketch, "E1095", {"start": v(51.03, 28.28) * mm, "end": v(51.12, 27.9) * mm});
            skLineSegment(sketch, "E1096", {"start": v(23.9, 39.84) * mm, "end": v(23.9, 39.76) * mm});
            skLineSegment(sketch, "E1097", {"start": v(9.54, 49.13) * mm, "end": v(11.73, 50.1) * mm});
            skLineSegment(sketch, "E1098", {"start": v(27.46, 23.45) * mm, "end": v(27.37, 23.55) * mm});
            skLineSegment(sketch, "E1099", {"start": v(24.76, 41.47) * mm, "end": v(24.65, 41.38) * mm});
            skLineSegment(sketch, "E1100", {"start": v(27.4, 21.7) * mm, "end": v(27.47, 21.78) * mm});
            skLineSegment(sketch, "E1101", {"start": v(6.59, 28.7) * mm, "end": v(5.44, 29.26) * mm});
            skLineSegment(sketch, "E1102", {"start": v(46.25, 33.52) * mm, "end": v(46.96, 33.12) * mm});
            skLineSegment(sketch, "E1103", {"start": v(23.96, 19.98) * mm, "end": v(24.68, 20.17) * mm});
            skLineSegment(sketch, "E1104", {"start": v(47.1, 16.97) * mm, "end": v(46.28, 16.25) * mm});
            skLineSegment(sketch, "E1105", {"start": v(0.63, 35.06) * mm, "end": v(0.57, 35.36) * mm});
            skLineSegment(sketch, "E1106", {"start": v(51.6, 40.94) * mm, "end": v(54.5, 51.97) * mm});
            skLineSegment(sketch, "E1107", {"start": v(0.87, 34.22) * mm, "end": v(0.78, 34.5) * mm});
            skLineSegment(sketch, "E1108", {"start": v(23.91, 39.68) * mm, "end": v(23.93, 39.6) * mm});
            skLineSegment(sketch, "E1109", {"start": v(50.92, 28.65) * mm, "end": v(51.03, 28.28) * mm});
            skLineSegment(sketch, "E1110", {"start": v(23.9, 39.92) * mm, "end": v(23.9, 39.84) * mm});
            skLineSegment(sketch, "E1111", {"start": v(27.7, 22.4) * mm, "end": v(27.73, 22.53) * mm});
            skLineSegment(sketch, "E1112", {"start": v(25, 38.47) * mm, "end": v(25.22, 38.37) * mm});
            skLineSegment(sketch, "E1113", {"start": v(27.5, 23.4) * mm, "end": v(27.46, 23.45) * mm});
            skLineSegment(sketch, "E1114", {"start": v(24.87, 41.56) * mm, "end": v(24.76, 41.47) * mm});
            skLineSegment(sketch, "E1115", {"start": v(27.65, 22.16) * mm, "end": v(27.68, 22.26) * mm});
            skLineSegment(sketch, "E1116", {"start": v(50.12, 21.3) * mm, "end": v(49.66, 20.34) * mm});
            skLineSegment(sketch, "E1117", {"start": v(7.83, 28.24) * mm, "end": v(6.59, 28.7) * mm});
            skLineSegment(sketch, "E1118", {"start": v(-0.9, 21.47) * mm, "end": v(1.4, 20.9) * mm});
            skLineSegment(sketch, "E1119", {"start": v(4, 45.23) * mm, "end": v(4.78, 46) * mm});
            skLineSegment(sketch, "E1120", {"start": v(24.55, 41.28) * mm, "end": v(24.45, 41.19) * mm});
            skLineSegment(sketch, "E1121", {"start": v(23.93, 39.6) * mm, "end": v(23.94, 39.52) * mm});
            skLineSegment(sketch, "E1122", {"start": v(25.22, 38.37) * mm, "end": v(25.46, 38.28) * mm});
            skLineSegment(sketch, "E1123", {"start": v(49.83, 30.6) * mm, "end": v(50.27, 30) * mm});
            skLineSegment(sketch, "E1124", {"start": v(5.64, 46.7) * mm, "end": v(6.55, 47.37) * mm});
            skLineSegment(sketch, "E1125", {"start": v(27.53, 23.35) * mm, "end": v(27.5, 23.4) * mm});
            skLineSegment(sketch, "E1126", {"start": v(27.27, 21.52) * mm, "end": v(27.34, 21.6) * mm});
            skLineSegment(sketch, "E1127", {"start": v(4.9, 29.56) * mm, "end": v(4.4, 29.88) * mm});
            skLineSegment(sketch, "E1128", {"start": v(1.4, 20.9) * mm, "end": v(6.35, 20) * mm});
            skLineSegment(sketch, "E1129", {"start": v(47.84, 41.82) * mm, "end": v(43.7, 42.51) * mm});
            skLineSegment(sketch, "E1130", {"start": v(38.25, 11.84) * mm, "end": v(35.9, 11.1) * mm});
            skLineSegment(sketch, "E1131", {"start": v(45.02, 53.05) * mm, "end": v(54.5, 51.97) * mm});
            skLineSegment(sketch, "E1132", {"start": v(0.5, 35.98) * mm, "end": v(0.48, 36.62) * mm});
            skLineSegment(sketch, "E1133", {"start": v(1.33, 33.18) * mm, "end": v(1.08, 33.7) * mm});
            skLineSegment(sketch, "E1134", {"start": v(23.94, 39.52) * mm, "end": v(23.97, 39.45) * mm});
            skLineSegment(sketch, "E1135", {"start": v(51.26, 26.24) * mm, "end": v(51.2, 25.33) * mm});
            skLineSegment(sketch, "E1136", {"start": v(23.92, 40.09) * mm, "end": v(23.9, 40) * mm});
            skLineSegment(sketch, "E1137", {"start": v(25.46, 38.28) * mm, "end": v(25.72, 38.2) * mm});
            skLineSegment(sketch, "E1138", {"start": v(6.55, 47.37) * mm, "end": v(7.5, 48) * mm});
            skLineSegment(sketch, "E1139", {"start": v(27.37, 23.55) * mm, "end": v(27.27, 23.65) * mm});
            skLineSegment(sketch, "E1140", {"start": v(25.12, 41.72) * mm, "end": v(25, 41.64) * mm});
            skLineSegment(sketch, "E1141", {"start": v(27.34, 21.6) * mm, "end": v(27.4, 21.7) * mm});
            skLineSegment(sketch, "E1142", {"start": v(49.13, 19.43) * mm, "end": v(48.52, 18.56) * mm});
            skLineSegment(sketch, "E1143", {"start": v(22.37, 19.66) * mm, "end": v(23.96, 19.98) * mm});
            skLineSegment(sketch, "E1144", {"start": v(24.1, 39.17) * mm, "end": v(24.16, 39.1) * mm});
            skLineSegment(sketch, "E1145", {"start": v(2.66, 43.54) * mm, "end": v(3.3, 44.4) * mm});
            skLineSegment(sketch, "E1146", {"start": v(24.37, 41.08) * mm, "end": v(24.29, 40.98) * mm});
            skLineSegment(sketch, "E1147", {"start": v(1.08, 33.7) * mm, "end": v(0.87, 34.22) * mm});
            skLineSegment(sketch, "E1148", {"start": v(27.04, 23.82) * mm, "end": v(26.9, 23.9) * mm});
            skLineSegment(sketch, "E1149", {"start": v(27.73, 22.53) * mm, "end": v(27.73, 22.66) * mm});
            skLineSegment(sketch, "E1150", {"start": v(50.46, 29.68) * mm, "end": v(50.64, 29.35) * mm});
            skLineSegment(sketch, "E1151", {"start": v(27.61, 22.06) * mm, "end": v(27.65, 22.16) * mm});
            skLineSegment(sketch, "E1152", {"start": v(49.66, 20.34) * mm, "end": v(49.13, 19.43) * mm});
            skLineSegment(sketch, "E1153", {"start": v(40.36, 35.54) * mm, "end": v(42.17, 35.08) * mm});
            skLineSegment(sketch, "E1154", {"start": v(39.24, 42.95) * mm, "end": v(34.51, 43.1) * mm});
            skLineSegment(sketch, "E1155", {"start": v(24.4, 38.85) * mm, "end": v(24.47, 38.79) * mm});
            skLineSegment(sketch, "E1156", {"start": v(29.95, 53.32) * mm, "end": v(35.18, 53.46) * mm});
            skLineSegment(sketch, "E1157", {"start": v(3.3, 44.4) * mm, "end": v(4, 45.23) * mm});
            skLineSegment(sketch, "E1158", {"start": v(24.45, 41.19) * mm, "end": v(24.37, 41.08) * mm});
            skLineSegment(sketch, "E1159", {"start": v(27.73, 22.78) * mm, "end": v(27.72, 22.84) * mm});
            skLineSegment(sketch, "E1160", {"start": v(23.08, 9.1) * mm, "end": v(18.04, 8.94) * mm});
            skLineSegment(sketch, "E1161", {"start": v(50.27, 30) * mm, "end": v(50.46, 29.68) * mm});
            skLineSegment(sketch, "E1162", {"start": v(18.72, 25.83) * mm, "end": v(13.21, 26.79) * mm});
            skLineSegment(sketch, "E1163", {"start": v(26.47, 20.9) * mm, "end": v(26.7, 21.04) * mm});
            skLineSegment(sketch, "E1164", {"start": v(47.85, 17.74) * mm, "end": v(47.1, 16.97) * mm});
            skLineSegment(sketch, "E1165", {"start": v(5.44, 29.26) * mm, "end": v(4.9, 29.56) * mm});
            skLineSegment(sketch, "E1166", {"start": v(46.96, 33.12) * mm, "end": v(47.63, 32.68) * mm});
            skLineSegment(sketch, "E1167", {"start": v(27.62, 23.2) * mm, "end": v(27.6, 23.24) * mm});
            skLineSegment(sketch, "E1168", {"start": v(43.7, 42.51) * mm, "end": v(39.24, 42.95) * mm});
            skLineSegment(sketch, "E1169", {"start": v(0.57, 35.36) * mm, "end": v(0.5, 35.98) * mm});
            skLineSegment(sketch, "E1170", {"start": v(18.04, 8.94) * mm, "end": v(5.8, 9.43) * mm});
            skLineSegment(sketch, "E1171", {"start": v(24.03, 39.3) * mm, "end": v(24.07, 39.24) * mm});
            skLineSegment(sketch, "E1172", {"start": v(23.9, 40) * mm, "end": v(23.9, 39.92) * mm});
            skLineSegment(sketch, "E1173", {"start": v(26.7, 21.04) * mm, "end": v(26.92, 21.2) * mm});
            skLineSegment(sketch, "E1174", {"start": v(27.68, 22.26) * mm, "end": v(27.7, 22.4) * mm});
            skLineSegment(sketch, "E1175", {"start": v(3.02, 30.96) * mm, "end": v(2.62, 31.36) * mm});
            skLineSegment(sketch, "E1176", {"start": v(31.22, 37.05) * mm, "end": v(38.47, 35.91) * mm});
            skLineSegment(sketch, "E1177", {"start": v(50.8, 29) * mm, "end": v(50.92, 28.65) * mm});
            skLineSegment(sketch, "E1178", {"start": v(7.5, 48) * mm, "end": v(8.5, 48.58) * mm});
            skLineSegment(sketch, "E1179", {"start": v(23.5, 25.03) * mm, "end": v(18.72, 25.83) * mm});
            skLineSegment(sketch, "E1180", {"start": v(25, 41.64) * mm, "end": v(24.87, 41.56) * mm});
            skLineSegment(sketch, "E1181", {"start": v(0.72, 38.75) * mm, "end": v(0.9, 39.52) * mm});
            skLineSegment(sketch, "E1182", {"start": v(27.65, 23.13) * mm, "end": v(27.62, 23.2) * mm});
            skLineSegment(sketch, "E1183", {"start": v(50.51, 22.31) * mm, "end": v(50.12, 21.3) * mm});
            skLineSegment(sketch, "E1184", {"start": v(5.8, 9.43) * mm, "end": v(-6, 10.98) * mm});
            skLineSegment(sketch, "E1185", {"start": v(24.07, 39.24) * mm, "end": v(24.1, 39.17) * mm});
            skLineSegment(sketch, "E1186", {"start": v(26.9, 23.9) * mm, "end": v(26.76, 23.98) * mm});
            skLineSegment(sketch, "E1187", {"start": v(24.04, 40.51) * mm, "end": v(24, 40.39) * mm});
            skLineSegment(sketch, "E1188", {"start": v(26.92, 21.2) * mm, "end": v(27.1, 21.35) * mm});
            skLineSegment(sketch, "E1189", {"start": v(2.62, 31.36) * mm, "end": v(2.25, 31.79) * mm});
            skLineSegment(sketch, "E1190", {"start": v(38.47, 35.91) * mm, "end": v(40.36, 35.54) * mm});
            skLineSegment(sketch, "E1191", {"start": v(27.38, 42.54) * mm, "end": v(26.67, 42.35) * mm});
            skLineSegment(sketch, "E1192", {"start": v(49.35, 31.17) * mm, "end": v(49.83, 30.6) * mm});
            skLineSegment(sketch, "E1193", {"start": v(50.83, 23.37) * mm, "end": v(50.51, 22.31) * mm});
            skLineSegment(sketch, "E1194", {"start": v(35.18, 53.46) * mm, "end": v(45.02, 53.05) * mm});
            skLineSegment(sketch, "E1195", {"start": v(24.09, 40.64) * mm, "end": v(24.04, 40.51) * mm});
            skLineSegment(sketch, "E1196", {"start": v(27.72, 22.84) * mm, "end": v(27.71, 22.9) * mm});
            skLineSegment(sketch, "E1197", {"start": v(23.97, 39.45) * mm, "end": v(24, 39.38) * mm});
            skLineSegment(sketch, "E1198", {"start": v(0.9, 39.52) * mm, "end": v(1.23, 40.6) * mm});
            skLineSegment(sketch, "E1199", {"start": v(28.32, 9.59) * mm, "end": v(23.08, 9.1) * mm});
            skLineSegment(sketch, "E1200", {"start": v(2.25, 31.79) * mm, "end": v(1.91, 32.23) * mm});
            skLineSegment(sketch, "E1201", {"start": v(25.72, 38.2) * mm, "end": v(28.16, 37.59) * mm});
            skLineSegment(sketch, "E1202", {"start": v(25.94, 20.64) * mm, "end": v(26.47, 20.9) * mm});
            skLineSegment(sketch, "E1203", {"start": v(48.82, 31.71) * mm, "end": v(49.35, 31.17) * mm});
            skLineSegment(sketch, "E1204", {"start": v(25.35, 24.55) * mm, "end": v(24.48, 24.8) * mm});
            skLineSegment(sketch, "E1205", {"start": v(28.13, 42.7) * mm, "end": v(27.38, 42.54) * mm});
            skLineSegment(sketch, "E1206", {"start": v(24.16, 39.1) * mm, "end": v(24.2, 39.04) * mm});
            skLineSegment(sketch, "E1207", {"start": v(51.06, 24.38) * mm, "end": v(50.83, 23.37) * mm});
            skLineSegment(sketch, "E1208", {"start": v(24.15, 40.75) * mm, "end": v(24.09, 40.64) * mm});
            skLineSegment(sketch, "E1209", {"start": v(-3.07, 22.14) * mm, "end": v(-0.9, 21.47) * mm});
            skLineSegment(sketch, "E1210", {"start": v(27.68, 23.02) * mm, "end": v(27.67, 23.08) * mm});
            skLineSegment(sketch, "E1211", {"start": v(1.23, 40.6) * mm, "end": v(1.63, 41.63) * mm});
            skLineSegment(sketch, "E1212", {"start": v(27.2, 21.43) * mm, "end": v(27.27, 21.52) * mm});
            skLineSegment(sketch, "E1213", {"start": v(42.17, 35.08) * mm, "end": v(43.87, 34.53) * mm});
            skLineSegment(sketch, "E1214", {"start": v(16.56, 51.6) * mm, "end": v(19.12, 52.17) * mm});
            skLineSegment(sketch, "E1215", {"start": v(26.1, 24.28) * mm, "end": v(25.35, 24.55) * mm});
            skLineSegment(sketch, "E1216", {"start": v(29.74, 42.92) * mm, "end": v(28.13, 42.7) * mm});
            skLineSegment(sketch, "E1217", {"start": v(24.2, 39.04) * mm, "end": v(24.27, 38.97) * mm});
            skLineSegment(sketch, "E1218", {"start": v(44.5, 14.92) * mm, "end": v(42.56, 13.74) * mm});
            skLineSegment(sketch, "E1219", {"start": v(3.45, 30.58) * mm, "end": v(3.02, 30.96) * mm});
            skLineSegment(sketch, "E1220", {"start": v(27.7, 22.96) * mm, "end": v(27.68, 23.02) * mm});
            skLineSegment(sketch, "E1221", {"start": v(51.19, 27.5) * mm, "end": v(51.23, 27.1) * mm});
            skLineSegment(sketch, "E1222", {"start": v(0.59, 38.01) * mm, "end": v(0.72, 38.75) * mm});
            skLineSegment(sketch, "E1223", {"start": v(24, 40.39) * mm, "end": v(23.96, 40.26) * mm});
            skLineSegment(sketch, "E1224", {"start": v(33.47, 10.47) * mm, "end": v(30.94, 9.97) * mm});
            skLineSegment(sketch, "E1225", {"start": v(1.6, 32.7) * mm, "end": v(1.33, 33.18) * mm});
            skLineSegment(sketch, "E1226", {"start": v(26.67, 42.35) * mm, "end": v(26, 42.12) * mm});
            skLineSegment(sketch, "E1227", {"start": v(24.68, 20.17) * mm, "end": v(25.34, 20.4) * mm});
            skLineSegment(sketch, "E1228", {"start": v(48.52, 18.56) * mm, "end": v(47.85, 17.74) * mm});
            skLineSegment(sketch, "E1229", {"start": v(43.87, 34.53) * mm, "end": v(45.49, 33.88) * mm});
            skLineSegment(sketch, "E1230", {"start": v(14.09, 50.93) * mm, "end": v(16.56, 51.6) * mm});
            skLineSegment(sketch, "E1231", {"start": v(26.76, 23.98) * mm, "end": v(26.1, 24.28) * mm});
            skLineSegment(sketch, "E1232", {"start": v(24.27, 38.97) * mm, "end": v(24.33, 38.9) * mm});
            skLineSegment(sketch, "E1233", {"start": v(24.29, 40.98) * mm, "end": v(24.21, 40.87) * mm});
            skLineSegment(sketch, "E1234", {"start": v(27.71, 22.9) * mm, "end": v(27.7, 22.96) * mm});
            skLineSegment(sketch, "E1235", {"start": v(2.1, 42.61) * mm, "end": v(2.66, 43.54) * mm});
            skLineSegment(sketch, "E1236", {"start": v(30.94, 9.97) * mm, "end": v(28.32, 9.59) * mm});
            skLineSegment(sketch, "E1237", {"start": v(50.64, 29.35) * mm, "end": v(50.8, 29) * mm});
            skLineSegment(sketch, "E1238", {"start": v(25.34, 20.4) * mm, "end": v(25.94, 20.64) * mm});
            skLineSegment(sketch, "E1239", {"start": v(45.49, 33.88) * mm, "end": v(46.25, 33.52) * mm});
            skLineSegment(sketch, "E1240", {"start": v(11.73, 50.1) * mm, "end": v(14.09, 50.93) * mm});
            skLineSegment(sketch, "E1241", {"start": v(24.48, 24.8) * mm, "end": v(23.5, 25.03) * mm});
            skLineSegment(sketch, "E1242", {"start": v(34.51, 43.1) * mm, "end": v(31.42, 43.04) * mm});
            skLineSegment(sketch, "E1243", {"start": v(4.4, 29.88) * mm, "end": v(3.91, 30.22) * mm});
            skLineSegment(sketch, "E1244", {"start": v(-6, 10.98) * mm, "end": v(-3.07, 22.14) * mm});
            skLineSegment(sketch, "E1245", {"start": v(27.67, 23.08) * mm, "end": v(27.65, 23.13) * mm});
            skLineSegment(sketch, "E1246", {"start": v(40.48, 12.72) * mm, "end": v(38.25, 11.84) * mm});
            skLineSegment(sketch, "E1247", {"start": v(19.12, 52.17) * mm, "end": v(21.77, 52.6) * mm});
            skLineSegment(sketch, "E1248", {"start": v(0.48, 36.62) * mm, "end": v(0.5, 37.3) * mm});
            skLineSegment(sketch, "E1249", {"start": v(23.93, 40.17) * mm, "end": v(23.92, 40.09) * mm});
            skLineSegment(sketch, "E1250", {"start": v(27.1, 21.35) * mm, "end": v(27.2, 21.43) * mm});
            skLineSegment(sketch, "E1251", {"start": v(23.9, 39.76) * mm, "end": v(23.91, 39.68) * mm});
            skLineSegment(sketch, "E1252", {"start": v(51.26, 26.67) * mm, "end": v(51.26, 26.24) * mm});
            skLineSegment(sketch, "E1253", {"start": v(25.4, 41.86) * mm, "end": v(25.12, 41.72) * mm});
            skLineSegment(sketch, "E1254", {"start": v(24.8, 38.57) * mm, "end": v(25, 38.47) * mm});
            skLineSegment(sketch, "E1255", {"start": v(13.21, 26.79) * mm, "end": v(10.47, 27.44) * mm});
            skLineSegment(sketch, "E1256", {"start": v(3.91, 30.22) * mm, "end": v(3.45, 30.58) * mm});
            skLineSegment(sketch, "E1257", {"start": v(11.53, 19.48) * mm, "end": v(16.66, 19.3) * mm});
            skLineSegment(sketch, "E1258", {"start": v(27.6, 23.24) * mm, "end": v(27.56, 23.3) * mm});
            skLineSegment(sketch, "E1259", {"start": v(24, 39.38) * mm, "end": v(24.03, 39.3) * mm});
            skLineSegment(sketch, "E1260", {"start": v(42.56, 13.74) * mm, "end": v(40.48, 12.72) * mm});
            skLineSegment(sketch, "E1261", {"start": v(0.5, 37.3) * mm, "end": v(0.59, 38.01) * mm});
            skLineSegment(sketch, "E1262", {"start": v(23.96, 40.26) * mm, "end": v(23.93, 40.17) * mm});
            skLineSegment(sketch, "E1263", {"start": v(1.91, 32.23) * mm, "end": v(1.6, 32.7) * mm});
            skLineSegment(sketch, "E1264", {"start": v(28.16, 37.59) * mm, "end": v(31.22, 37.05) * mm});
            skLineSegment(sketch, "E1265", {"start": v(51.23, 27.1) * mm, "end": v(51.26, 26.67) * mm});
            skLineSegment(sketch, "E1266", {"start": v(26, 42.12) * mm, "end": v(25.4, 41.86) * mm});
            skLineSegment(sketch, "E1267", {"start": v(8.5, 48.58) * mm, "end": v(9.54, 49.13) * mm});
            skLineSegment(sketch, "E1268", {"start": v(27.16, 23.74) * mm, "end": v(27.04, 23.82) * mm});
            skLineSegment(sketch, "E1269", {"start": v(27.47, 21.78) * mm, "end": v(27.52, 21.87) * mm});
            skLineSegment(sketch, "E1270", {"start": v(24.21, 40.87) * mm, "end": v(24.15, 40.75) * mm});
            skLineSegment(sketch, "E1271", {"start": v(16.66, 19.3) * mm, "end": v(20.58, 19.45) * mm});
            skLineSegment(sketch, "E1272", {"start": v(24.47, 38.79) * mm, "end": v(24.63, 38.67) * mm});
            skLineSegment(sketch, "E1273", {"start": v(35.9, 11.1) * mm, "end": v(33.47, 10.47) * mm});
            skLineSegment(sketch, "E1274", {"start": v(24.5, 52.93) * mm, "end": v(29.95, 53.32) * mm});
            skLineSegment(sketch, "E1275", {"start": v(1.63, 41.63) * mm, "end": v(2.1, 42.61) * mm});
            skLineSegment(sketch, "E1276", {"start": v(0.78, 34.5) * mm, "end": v(0.7, 34.77) * mm});
            skLineSegment(sketch, "E1277", {"start": v(51.2, 25.33) * mm, "end": v(51.06, 24.38) * mm});
            skLineSegment(sketch, "E1278", {"start": v(27.73, 22.72) * mm, "end": v(27.73, 22.78) * mm});
            skLineSegment(sketch, "E1279", {"start": v(27.27, 23.65) * mm, "end": v(27.16, 23.74) * mm});
            skLineSegment(sketch, "E1280", {"start": v(31.42, 43.04) * mm, "end": v(29.74, 42.92) * mm});
            skLineSegment(sketch, "E1281", {"start": v(27.52, 21.87) * mm, "end": v(27.57, 21.97) * mm});
            skLineSegment(sketch, "E1282", {"start": v(47.63, 32.68) * mm, "end": v(48.25, 32.22) * mm});
            skLineSegment(sketch, "E1283", {"start": v(20.58, 19.45) * mm, "end": v(22.37, 19.66) * mm});
            skLineSegment(sketch, "E1284", {"start": v(96.78, -28.65) * mm, "end": v(96.9, -27.72) * mm});
            skLineSegment(sketch, "E1285", {"start": v(83.83, -22.93) * mm, "end": v(83.51, -23.11) * mm});
            skLineSegment(sketch, "E1286", {"start": v(84.25, -36.57) * mm, "end": v(85.77, -36.67) * mm});
            skLineSegment(sketch, "E1287", {"start": v(63.86, 47.45) * mm, "end": v(63.55, 47.02) * mm});
            skLineSegment(sketch, "E1288", {"start": v(69.65, 34.53) * mm, "end": v(69.29, 35.67) * mm});
            skLineSegment(sketch, "E1289", {"start": v(70.77, 46.6) * mm, "end": v(71.26, 47.17) * mm});
            skLineSegment(sketch, "E1290", {"start": v(84.7, 51.01) * mm, "end": v(87.92, 50.9) * mm});
            skLineSegment(sketch, "E1291", {"start": v(82.83, -23.42) * mm, "end": v(82.47, -23.55) * mm});
            skLineSegment(sketch, "E1292", {"start": v(95.2, -33.01) * mm, "end": v(95.56, -32.42) * mm});
            skLineSegment(sketch, "E1293", {"start": v(86.44, -16.64) * mm, "end": v(86.43, -17.72) * mm});
            skLineSegment(sketch, "E1294", {"start": v(68.7, 38.88) * mm, "end": v(68.7, 39.99) * mm});
            skLineSegment(sketch, "E1295", {"start": v(82.7, -36.4) * mm, "end": v(84.25, -36.57) * mm});
            skLineSegment(sketch, "E1296", {"start": v(77.07, 7.53) * mm, "end": v(82, -2.07) * mm});
            skLineSegment(sketch, "E1297", {"start": v(69.65, 51.6) * mm, "end": v(68.56, 51.14) * mm});
            skLineSegment(sketch, "E1298", {"start": v(96.79, -22) * mm, "end": v(96.4, -19.73) * mm});
            skLineSegment(sketch, "E1299", {"start": v(62.56, 45.08) * mm, "end": v(62.37, 44.55) * mm});
            skLineSegment(sketch, "E1300", {"start": v(78.6, -23.93) * mm, "end": v(77.6, -23.85) * mm});
            skLineSegment(sketch, "E1301", {"start": v(92.94, -35.22) * mm, "end": v(93.45, -34.87) * mm});
            skLineSegment(sketch, "E1302", {"start": v(71.26, 47.17) * mm, "end": v(71.8, 47.7) * mm});
            skLineSegment(sketch, "E1303", {"start": v(101.23, 49.1) * mm, "end": v(114.48, 46.06) * mm});
            skLineSegment(sketch, "E1304", {"start": v(70.79, 52.01) * mm, "end": v(69.65, 51.6) * mm});
            skLineSegment(sketch, "E1305", {"start": v(86.34, -18.7) * mm, "end": v(86.27, -19.16) * mm});
            skLineSegment(sketch, "E1306", {"start": v(69.67, -21.86) * mm, "end": v(64.64, -19.87) * mm});
            skLineSegment(sketch, "E1307", {"start": v(62.37, 44.55) * mm, "end": v(62.2, 44) * mm});
            skLineSegment(sketch, "E1308", {"start": v(74.53, 52.92) * mm, "end": v(71.98, 52.37) * mm});
            skLineSegment(sketch, "E1309", {"start": v(79.54, -23.96) * mm, "end": v(78.6, -23.93) * mm});
            skLineSegment(sketch, "E1310", {"start": v(71.68, 29.85) * mm, "end": v(70.58, 32.2) * mm});
            skLineSegment(sketch, "E1311", {"start": v(69.92, 45.3) * mm, "end": v(70.32, 45.98) * mm});
            skLineSegment(sketch, "E1312", {"start": v(86.17, -14.17) * mm, "end": v(86.35, -15.46) * mm});
            skLineSegment(sketch, "E1313", {"start": v(59.47, -28.9) * mm, "end": v(69.1, -32.82) * mm});
            skLineSegment(sketch, "E1314", {"start": v(89.98, -36.37) * mm, "end": v(90.62, -36.21) * mm});
            skLineSegment(sketch, "E1315", {"start": v(67.54, 50.61) * mm, "end": v(66.6, 50.03) * mm});
            skLineSegment(sketch, "E1316", {"start": v(96.62, -29.52) * mm, "end": v(96.78, -28.65) * mm});
            skLineSegment(sketch, "E1317", {"start": v(62.2, 44) * mm, "end": v(62.07, 43.42) * mm});
            skLineSegment(sketch, "E1318", {"start": v(77.23, 53.27) * mm, "end": v(74.53, 52.92) * mm});
            skLineSegment(sketch, "E1319", {"start": v(85.38, -21.43) * mm, "end": v(85.16, -21.73) * mm});
            skLineSegment(sketch, "E1320", {"start": v(18.71, -7.5) * mm, "end": v(24.86, -10.97) * mm});
            skLineSegment(sketch, "E1321", {"start": v(70.58, 32.2) * mm, "end": v(69.65, 34.53) * mm});
            skLineSegment(sketch, "E1322", {"start": v(82.47, -23.55) * mm, "end": v(82.09, -23.66) * mm});
            skLineSegment(sketch, "E1323", {"start": v(79.7, 50.77) * mm, "end": v(81.35, 50.93) * mm});
            skLineSegment(sketch, "E1324", {"start": v(89.32, -36.5) * mm, "end": v(89.98, -36.37) * mm});
            skLineSegment(sketch, "E1325", {"start": v(70.03, 19.3) * mm, "end": v(77.07, 7.53) * mm});
            skLineSegment(sketch, "E1326", {"start": v(96.41, -30.33) * mm, "end": v(96.62, -29.52) * mm});
            skLineSegment(sketch, "E1327", {"start": v(62.77, 45.6) * mm, "end": v(62.56, 45.08) * mm});
            skLineSegment(sketch, "E1328", {"start": v(80.07, 53.46) * mm, "end": v(77.23, 53.27) * mm});
            skLineSegment(sketch, "E1329", {"start": v(85.58, -21.1) * mm, "end": v(85.38, -21.43) * mm});
            skLineSegment(sketch, "E1330", {"start": v(76.26, 21.7) * mm, "end": v(74.11, 25.38) * mm});
            skLineSegment(sketch, "E1331", {"start": v(24.86, -10.97) * mm, "end": v(42.66, -20.8) * mm});
            skLineSegment(sketch, "E1332", {"start": v(78.06, 50.52) * mm, "end": v(79.7, 50.77) * mm});
            skLineSegment(sketch, "E1333", {"start": v(81.3, -23.82) * mm, "end": v(80.44, -23.92) * mm});
            skLineSegment(sketch, "E1334", {"start": v(88.64, -36.58) * mm, "end": v(89.32, -36.5) * mm});
            skLineSegment(sketch, "E1335", {"start": v(86.27, -19.16) * mm, "end": v(86.17, -19.6) * mm});
            skLineSegment(sketch, "E1336", {"start": v(96.9, -27.72) * mm, "end": v(96.98, -26.72) * mm});
            skLineSegment(sketch, "E1337", {"start": v(61.95, 42.83) * mm, "end": v(61.87, 42.21) * mm});
            skLineSegment(sketch, "E1338", {"start": v(69.29, 35.67) * mm, "end": v(69, 36.78) * mm});
            skLineSegment(sketch, "E1339", {"start": v(111.83, 48.9) * mm, "end": v(103.4, 50.92) * mm});
            skLineSegment(sketch, "E1340", {"start": v(76.5, 50.15) * mm, "end": v(78.06, 50.52) * mm});
            skLineSegment(sketch, "E1341", {"start": v(81.7, -23.75) * mm, "end": v(81.3, -23.82) * mm});
            skLineSegment(sketch, "E1342", {"start": v(90.62, -36.21) * mm, "end": v(91.23, -36.02) * mm});
            skLineSegment(sketch, "E1343", {"start": v(65.04, 28.34) * mm, "end": v(67.23, 24.04) * mm});
            skLineSegment(sketch, "E1344", {"start": v(95.88, -31.78) * mm, "end": v(96.17, -31.08) * mm});
            skLineSegment(sketch, "E1345", {"start": v(96.98, -26.72) * mm, "end": v(97.01, -25.51) * mm});
            skLineSegment(sketch, "E1346", {"start": v(63.27, 46.56) * mm, "end": v(63, 46.08) * mm});
            skLineSegment(sketch, "E1347", {"start": v(85.91, -20.4) * mm, "end": v(85.75, -20.76) * mm});
            skLineSegment(sketch, "E1348", {"start": v(69, 36.78) * mm, "end": v(68.8, 37.86) * mm});
            skLineSegment(sketch, "E1349", {"start": v(72.98, 48.6) * mm, "end": v(73.63, 49) * mm});
            skLineSegment(sketch, "E1350", {"start": v(94.28, 50.25) * mm, "end": v(101.23, 49.1) * mm});
            skLineSegment(sketch, "E1351", {"start": v(41.85, -7.47) * mm, "end": v(18.71, -7.5) * mm});
            skLineSegment(sketch, "E1352", {"start": v(82.09, -23.66) * mm, "end": v(81.7, -23.75) * mm});
            skLineSegment(sketch, "E1353", {"start": v(85.77, -36.67) * mm, "end": v(87.24, -36.68) * mm});
            skLineSegment(sketch, "E1354", {"start": v(67.23, 24.04) * mm, "end": v(70.03, 19.3) * mm});
            skLineSegment(sketch, "E1355", {"start": v(82, -2.07) * mm, "end": v(83.74, -6.11) * mm});
            skLineSegment(sketch, "E1356", {"start": v(97.01, -25.51) * mm, "end": v(96.99, -24.32) * mm});
            skLineSegment(sketch, "E1357", {"start": v(63, 46.08) * mm, "end": v(62.77, 45.6) * mm});
            skLineSegment(sketch, "E1358", {"start": v(92.07, 52.84) * mm, "end": v(86.02, 53.38) * mm});
            skLineSegment(sketch, "E1359", {"start": v(86.05, -20) * mm, "end": v(85.91, -20.4) * mm});
            skLineSegment(sketch, "E1360", {"start": v(68.8, 37.86) * mm, "end": v(68.74, 38.37) * mm});
            skLineSegment(sketch, "E1361", {"start": v(70.32, 45.98) * mm, "end": v(70.77, 46.6) * mm});
            skLineSegment(sketch, "E1362", {"start": v(80.44, -23.92) * mm, "end": v(79.54, -23.96) * mm});
            skLineSegment(sketch, "E1363", {"start": v(91.83, -35.8) * mm, "end": v(92.4, -35.53) * mm});
            skLineSegment(sketch, "E1364", {"start": v(68.56, 51.14) * mm, "end": v(67.54, 50.61) * mm});
            skLineSegment(sketch, "E1365", {"start": v(83.74, -6.11) * mm, "end": v(85.02, -9.68) * mm});
            skLineSegment(sketch, "E1366", {"start": v(68.86, 42) * mm, "end": v(69.04, 42.92) * mm});
            skLineSegment(sketch, "E1367", {"start": v(62.07, 43.42) * mm, "end": v(61.95, 42.83) * mm});
            skLineSegment(sketch, "E1368", {"start": v(103.4, 50.92) * mm, "end": v(92.07, 52.84) * mm});
            skLineSegment(sketch, "E1369", {"start": v(86.17, -19.6) * mm, "end": v(86.05, -20) * mm});
            skLineSegment(sketch, "E1370", {"start": v(77.6, -23.85) * mm, "end": v(76.56, -23.7) * mm});
            skLineSegment(sketch, "E1371", {"start": v(94.48, -13.3) * mm, "end": v(92.87, -9.3) * mm});
            skLineSegment(sketch, "E1372", {"start": v(59.5, -17.48) * mm, "end": v(49.7, -12.21) * mm});
            skLineSegment(sketch, "E1373", {"start": v(74.3, 49.34) * mm, "end": v(75, 49.64) * mm});
            skLineSegment(sketch, "E1374", {"start": v(91.23, -36.02) * mm, "end": v(91.83, -35.8) * mm});
            skLineSegment(sketch, "E1375", {"start": v(64.91, 48.66) * mm, "end": v(64.54, 48.28) * mm});
            skLineSegment(sketch, "E1376", {"start": v(96.17, -31.08) * mm, "end": v(96.41, -30.33) * mm});
            skLineSegment(sketch, "E1377", {"start": v(85.16, -21.73) * mm, "end": v(84.93, -22.01) * mm});
            skLineSegment(sketch, "E1378", {"start": v(61.86, 38.83) * mm, "end": v(62.07, 37.32) * mm});
            skLineSegment(sketch, "E1379", {"start": v(83.01, 53.49) * mm, "end": v(80.07, 53.46) * mm});
            skLineSegment(sketch, "E1380", {"start": v(85.75, -20.76) * mm, "end": v(85.58, -21.1) * mm});
            skLineSegment(sketch, "E1381", {"start": v(74.11, 25.38) * mm, "end": v(71.68, 29.85) * mm});
            skLineSegment(sketch, "E1382", {"start": v(49.7, -12.21) * mm, "end": v(41.85, -7.47) * mm});
            skLineSegment(sketch, "E1383", {"start": v(73.63, 49) * mm, "end": v(74.3, 49.34) * mm});
            skLineSegment(sketch, "E1384", {"start": v(83.18, -23.28) * mm, "end": v(82.83, -23.42) * mm});
            skLineSegment(sketch, "E1385", {"start": v(87.24, -36.68) * mm, "end": v(88.64, -36.58) * mm});
            skLineSegment(sketch, "E1386", {"start": v(62.07, 37.32) * mm, "end": v(62.4, 35.71) * mm});
            skLineSegment(sketch, "E1387", {"start": v(85.89, -12.78) * mm, "end": v(86.17, -14.17) * mm});
            skLineSegment(sketch, "E1388", {"start": v(68.7, 39.99) * mm, "end": v(68.74, 41.03) * mm});
            skLineSegment(sketch, "E1389", {"start": v(64.54, 48.28) * mm, "end": v(64.2, 47.87) * mm});
            skLineSegment(sketch, "E1390", {"start": v(96.4, -19.73) * mm, "end": v(95.87, -17.53) * mm});
            skLineSegment(sketch, "E1391", {"start": v(115.13, 47.96) * mm, "end": v(111.83, 48.9) * mm});
            skLineSegment(sketch, "E1392", {"start": v(75.74, 49.91) * mm, "end": v(76.5, 50.15) * mm});
            skLineSegment(sketch, "E1393", {"start": v(83.51, -23.11) * mm, "end": v(83.18, -23.28) * mm});
            skLineSegment(sketch, "E1394", {"start": v(94.4, -34.04) * mm, "end": v(94.81, -33.55) * mm});
            skLineSegment(sketch, "E1395", {"start": v(62.4, 35.71) * mm, "end": v(62.85, 34.02) * mm});
            skLineSegment(sketch, "E1396", {"start": v(68.74, 41.03) * mm, "end": v(68.86, 42) * mm});
            skLineSegment(sketch, "E1397", {"start": v(76.87, -35.28) * mm, "end": v(79.52, -35.87) * mm});
            skLineSegment(sketch, "E1398", {"start": v(64.2, 47.87) * mm, "end": v(63.86, 47.45) * mm});
            skLineSegment(sketch, "E1399", {"start": v(86.4, -18.23) * mm, "end": v(86.34, -18.7) * mm});
            skLineSegment(sketch, "E1400", {"start": v(76.56, -23.7) * mm, "end": v(74.38, -23.28) * mm});
            skLineSegment(sketch, "E1401", {"start": v(95.87, -17.53) * mm, "end": v(94.48, -13.3) * mm});
            skLineSegment(sketch, "E1402", {"start": v(72.37, 48.17) * mm, "end": v(72.98, 48.6) * mm});
            skLineSegment(sketch, "E1403", {"start": v(119.1, 44.78) * mm, "end": v(115.13, 47.96) * mm});
            skLineSegment(sketch, "E1404", {"start": v(93.94, -34.47) * mm, "end": v(94.4, -34.04) * mm});
            skLineSegment(sketch, "E1405", {"start": v(65.3, 49.03) * mm, "end": v(64.91, 48.66) * mm});
            skLineSegment(sketch, "E1406", {"start": v(68.74, 38.37) * mm, "end": v(68.7, 38.88) * mm});
            skLineSegment(sketch, "E1407", {"start": v(59.47, -28.9) * mm, "end": v(42.66, -20.8) * mm});
            skLineSegment(sketch, "E1408", {"start": v(84.93, -22.01) * mm, "end": v(84.68, -22.27) * mm});
            skLineSegment(sketch, "E1409", {"start": v(61.78, 40.25) * mm, "end": v(61.86, 38.83) * mm});
            skLineSegment(sketch, "E1410", {"start": v(86.43, -17.72) * mm, "end": v(86.4, -18.23) * mm});
            skLineSegment(sketch, "E1411", {"start": v(96.99, -24.32) * mm, "end": v(96.79, -22) * mm});
            skLineSegment(sketch, "E1412", {"start": v(71.8, 47.7) * mm, "end": v(72.37, 48.17) * mm});
            skLineSegment(sketch, "E1413", {"start": v(92.87, -9.3) * mm, "end": v(89.13, -1.17) * mm});
            skLineSegment(sketch, "E1414", {"start": v(114.48, 46.06) * mm, "end": v(119.1, 44.78) * mm});
            skLineSegment(sketch, "E1415", {"start": v(93.45, -34.87) * mm, "end": v(93.94, -34.47) * mm});
            skLineSegment(sketch, "E1416", {"start": v(63.44, 32.22) * mm, "end": v(65.04, 28.34) * mm});
            skLineSegment(sketch, "E1417", {"start": v(85.02, -9.68) * mm, "end": v(85.89, -12.78) * mm});
            skLineSegment(sketch, "E1418", {"start": v(74.25, -34.56) * mm, "end": v(76.87, -35.28) * mm});
            skLineSegment(sketch, "E1419", {"start": v(84.13, -22.73) * mm, "end": v(83.83, -22.93) * mm});
            skLineSegment(sketch, "E1420", {"start": v(63.55, 47.02) * mm, "end": v(63.27, 46.56) * mm});
            skLineSegment(sketch, "E1421", {"start": v(72.08, -22.65) * mm, "end": v(69.67, -21.86) * mm});
            skLineSegment(sketch, "E1422", {"start": v(69.04, 42.92) * mm, "end": v(69.28, 43.77) * mm});
            skLineSegment(sketch, "E1423", {"start": v(89.13, -1.17) * mm, "end": v(85.03, 6.53) * mm});
            skLineSegment(sketch, "E1424", {"start": v(71.98, 52.37) * mm, "end": v(70.79, 52.01) * mm});
            skLineSegment(sketch, "E1425", {"start": v(81.35, 50.93) * mm, "end": v(84.7, 51.01) * mm});
            skLineSegment(sketch, "E1426", {"start": v(94.81, -33.55) * mm, "end": v(95.2, -33.01) * mm});
            skLineSegment(sketch, "E1427", {"start": v(66.6, 50.03) * mm, "end": v(65.71, 49.38) * mm});
            skLineSegment(sketch, "E1428", {"start": v(86.35, -15.46) * mm, "end": v(86.44, -16.64) * mm});
            skLineSegment(sketch, "E1429", {"start": v(69.1, -32.82) * mm, "end": v(74.25, -34.56) * mm});
            skLineSegment(sketch, "E1430", {"start": v(84.41, -22.51) * mm, "end": v(84.13, -22.73) * mm});
            skLineSegment(sketch, "E1431", {"start": v(79.52, -35.87) * mm, "end": v(82.7, -36.4) * mm});
            skLineSegment(sketch, "E1432", {"start": v(61.87, 42.21) * mm, "end": v(61.8, 41.58) * mm});
            skLineSegment(sketch, "E1433", {"start": v(86.02, 53.38) * mm, "end": v(83.01, 53.49) * mm});
            skLineSegment(sketch, "E1434", {"start": v(74.38, -23.28) * mm, "end": v(72.08, -22.65) * mm});
            skLineSegment(sketch, "E1435", {"start": v(69.28, 43.77) * mm, "end": v(69.57, 44.56) * mm});
            skLineSegment(sketch, "E1436", {"start": v(85.03, 6.53) * mm, "end": v(76.26, 21.7) * mm});
            skLineSegment(sketch, "E1437", {"start": v(92.4, -35.53) * mm, "end": v(92.94, -35.22) * mm});
            skLineSegment(sketch, "E1438", {"start": v(65.71, 49.38) * mm, "end": v(65.3, 49.03) * mm});
            skLineSegment(sketch, "E1439", {"start": v(84.68, -22.27) * mm, "end": v(84.41, -22.51) * mm});
            skLineSegment(sketch, "E1440", {"start": v(61.8, 41.58) * mm, "end": v(61.78, 40.25) * mm});
            skLineSegment(sketch, "E1441", {"start": v(64.64, -19.87) * mm, "end": v(59.5, -17.48) * mm});
            skLineSegment(sketch, "E1442", {"start": v(69.57, 44.56) * mm, "end": v(69.92, 45.3) * mm});
            skLineSegment(sketch, "E1443", {"start": v(75, 49.64) * mm, "end": v(75.74, 49.91) * mm});
            skLineSegment(sketch, "E1444", {"start": v(87.92, 50.9) * mm, "end": v(94.28, 50.25) * mm});
            skLineSegment(sketch, "E1445", {"start": v(95.56, -32.42) * mm, "end": v(95.88, -31.78) * mm});
            skLineSegment(sketch, "E1446", {"start": v(62.85, 34.02) * mm, "end": v(63.44, 32.22) * mm});
            skLineSegment(sketch, "E1447", {"start": v(101.84, 44.27) * mm, "end": v(111.93, 42.22) * mm});
            skLineSegment(sketch, "E1448", {"start": v(72.12, 44.86) * mm, "end": v(71.86, 44.43) * mm});
            skLineSegment(sketch, "E1449", {"start": v(109.7, -45.26) * mm, "end": v(109.97, -44.58) * mm});
            skLineSegment(sketch, "E1450", {"start": v(93.5, -38.1) * mm, "end": v(93.05, -38.32) * mm});
            skLineSegment(sketch, "E1451", {"start": v(80.95, 28.64) * mm, "end": v(79.47, 31.26) * mm});
            skLineSegment(sketch, "E1452", {"start": v(71.4, 35.15) * mm, "end": v(71.86, 33.9) * mm});
            skLineSegment(sketch, "E1453", {"start": v(78.08, 41.27) * mm, "end": v(78.26, 41.56) * mm});
            skLineSegment(sketch, "E1454", {"start": v(70.68, 38.13) * mm, "end": v(70.76, 37.57) * mm});
            skLineSegment(sketch, "E1455", {"start": v(100.43, 47.77) * mm, "end": v(95.24, 48.64) * mm});
            skLineSegment(sketch, "E1456", {"start": v(13.03, -7.5) * mm, "end": v(-13.72, -7.48) * mm});
            skLineSegment(sketch, "E1457", {"start": v(94.52, -53.45) * mm, "end": v(96.7, -53.32) * mm});
            skLineSegment(sketch, "E1458", {"start": v(99.35, -27.23) * mm, "end": v(99.2, -28.81) * mm});
            skLineSegment(sketch, "E1459", {"start": v(96.78, 44.98) * mm, "end": v(101.84, 44.27) * mm});
            skLineSegment(sketch, "E1460", {"start": v(93.05, -38.32) * mm, "end": v(92.59, -38.52) * mm});
            skLineSegment(sketch, "E1461", {"start": v(79.47, 31.26) * mm, "end": v(78.88, 32.48) * mm});
            skLineSegment(sketch, "E1462", {"start": v(73.04, 46.01) * mm, "end": v(72.72, 45.65) * mm});
            skLineSegment(sketch, "E1463", {"start": v(107.82, -48.3) * mm, "end": v(108.26, -47.75) * mm});
            skLineSegment(sketch, "E1464", {"start": v(98.73, -31.12) * mm, "end": v(98.5, -31.87) * mm});
            skLineSegment(sketch, "E1465", {"start": v(84.57, 45) * mm, "end": v(85.5, 45.15) * mm});
            skLineSegment(sketch, "E1466", {"start": v(63.77, -33.47) * mm, "end": v(54.66, -29.44) * mm});
            skLineSegment(sketch, "E1467", {"start": v(100.54, -52.66) * mm, "end": v(101.4, -52.42) * mm});
            skLineSegment(sketch, "E1468", {"start": v(110.22, -43.88) * mm, "end": v(110.61, -42.42) * mm});
            skLineSegment(sketch, "E1469", {"start": v(93.93, -37.84) * mm, "end": v(93.7, -37.98) * mm});
            skLineSegment(sketch, "E1470", {"start": v(72.9, 31.5) * mm, "end": v(73.96, 29.48) * mm});
            skLineSegment(sketch, "E1471", {"start": v(80.59, 43.68) * mm, "end": v(81.28, 44.02) * mm});
            skLineSegment(sketch, "E1472", {"start": v(77.5, 36.7) * mm, "end": v(77.4, 37.6) * mm});
            skLineSegment(sketch, "E1473", {"start": v(80.7, 49.26) * mm, "end": v(79.8, 49.16) * mm});
            skLineSegment(sketch, "E1474", {"start": v(70.62, 39.37) * mm, "end": v(70.64, 38.67) * mm});
            skLineSegment(sketch, "E1475", {"start": v(89.62, -53.27) * mm, "end": v(92.16, -53.43) * mm});
            skLineSegment(sketch, "E1476", {"start": v(111.08, -35.81) * mm, "end": v(110.94, -34) * mm});
            skLineSegment(sketch, "E1477", {"start": v(99.3, -24.03) * mm, "end": v(99.38, -25.63) * mm});
            skLineSegment(sketch, "E1478", {"start": v(71.86, 44.43) * mm, "end": v(71.61, 43.97) * mm});
            skLineSegment(sketch, "E1479", {"start": v(109.97, -44.58) * mm, "end": v(110.22, -43.88) * mm});
            skLineSegment(sketch, "E1480", {"start": v(71.86, 33.9) * mm, "end": v(72.9, 31.5) * mm});
            skLineSegment(sketch, "E1481", {"start": v(76.18, 48.16) * mm, "end": v(75.32, 47.74) * mm});
            skLineSegment(sketch, "E1482", {"start": v(73.75, 46.67) * mm, "end": v(73.39, 46.35) * mm});
            skLineSegment(sketch, "E1483", {"start": v(57.7, -44.32) * mm, "end": v(66.28, -47.56) * mm});
            skLineSegment(sketch, "E1484", {"start": v(79.78, -38.76) * mm, "end": v(74.42, -37.38) * mm});
            skLineSegment(sketch, "E1485", {"start": v(78.66, 42.12) * mm, "end": v(78.89, 42.37) * mm});
            skLineSegment(sketch, "E1486", {"start": v(77.43, 39.23) * mm, "end": v(77.5, 39.6) * mm});
            skLineSegment(sketch, "E1487", {"start": v(96.47, -35.57) * mm, "end": v(95.48, -36.56) * mm});
            skLineSegment(sketch, "E1488", {"start": v(87.51, 45.35) * mm, "end": v(89.67, 45.42) * mm});
            skLineSegment(sketch, "E1489", {"start": v(102.21, -52.14) * mm, "end": v(102.99, -51.83) * mm});
            skLineSegment(sketch, "E1490", {"start": v(107.55, -20) * mm, "end": v(104.15, -11.43) * mm});
            skLineSegment(sketch, "E1491", {"start": v(73.39, 46.35) * mm, "end": v(73.04, 46.01) * mm});
            skLineSegment(sketch, "E1492", {"start": v(108.26, -47.75) * mm, "end": v(108.67, -47.16) * mm});
            skLineSegment(sketch, "E1493", {"start": v(78, 34.71) * mm, "end": v(77.71, 35.73) * mm});
            skLineSegment(sketch, "E1494", {"start": v(75.32, 47.74) * mm, "end": v(74.91, 47.5) * mm});
            skLineSegment(sketch, "E1495", {"start": v(98.5, -31.87) * mm, "end": v(98.23, -32.6) * mm});
            skLineSegment(sketch, "E1496", {"start": v(78.89, 42.37) * mm, "end": v(79.13, 42.62) * mm});
            skLineSegment(sketch, "E1497", {"start": v(90.6, -39.14) * mm, "end": v(89.54, -39.34) * mm});
            skLineSegment(sketch, "E1498", {"start": v(96.18, -11.5) * mm, "end": v(97.83, -16.4) * mm});
            skLineSegment(sketch, "E1499", {"start": v(85.5, 45.15) * mm, "end": v(87.51, 45.35) * mm});
            skLineSegment(sketch, "E1500", {"start": v(101.4, -52.42) * mm, "end": v(102.21, -52.14) * mm});
            skLineSegment(sketch, "E1501", {"start": v(77.71, 35.73) * mm, "end": v(77.5, 36.7) * mm});
            skLineSegment(sketch, "E1502", {"start": v(74.91, 47.5) * mm, "end": v(74.5, 47.25) * mm});
            skLineSegment(sketch, "E1503", {"start": v(70.64, 38.67) * mm, "end": v(70.68, 38.13) * mm});
            skLineSegment(sketch, "E1504", {"start": v(98.23, -32.6) * mm, "end": v(97.91, -33.33) * mm});
            skLineSegment(sketch, "E1505", {"start": v(105.7, -50.3) * mm, "end": v(106.29, -49.84) * mm});
            skLineSegment(sketch, "E1506", {"start": v(78.26, 41.56) * mm, "end": v(78.45, 41.85) * mm});
            skLineSegment(sketch, "E1507", {"start": v(92.16, -53.43) * mm, "end": v(94.52, -53.45) * mm});
            skLineSegment(sketch, "E1508", {"start": v(99.38, -25.63) * mm, "end": v(99.35, -27.23) * mm});
            skLineSegment(sketch, "E1509", {"start": v(89.54, -39.34) * mm, "end": v(88.44, -39.47) * mm});
            skLineSegment(sketch, "E1510", {"start": v(91.94, 45.38) * mm, "end": v(96.78, 44.98) * mm});
            skLineSegment(sketch, "E1511", {"start": v(93.86, -5.87) * mm, "end": v(96.18, -11.5) * mm});
            skLineSegment(sketch, "E1512", {"start": v(70.89, 41.89) * mm, "end": v(70.78, 41.3) * mm});
            skLineSegment(sketch, "E1513", {"start": v(111.12, -37.57) * mm, "end": v(111.08, -35.81) * mm});
            skLineSegment(sketch, "E1514", {"start": v(78.88, 32.48) * mm, "end": v(78.4, 33.63) * mm});
            skLineSegment(sketch, "E1515", {"start": v(77.06, 48.5) * mm, "end": v(76.18, 48.16) * mm});
            skLineSegment(sketch, "E1516", {"start": v(82.39, -39.22) * mm, "end": v(79.78, -38.76) * mm});
            skLineSegment(sketch, "E1517", {"start": v(96.87, -35.1) * mm, "end": v(96.47, -35.57) * mm});
            skLineSegment(sketch, "E1518", {"start": v(83.67, 44.82) * mm, "end": v(84.57, 45) * mm});
            skLineSegment(sketch, "E1519", {"start": v(66.28, -47.56) * mm, "end": v(73.99, -50.05) * mm});
            skLineSegment(sketch, "E1520", {"start": v(91.32, -0.5) * mm, "end": v(93.86, -5.87) * mm});
            skLineSegment(sketch, "E1521", {"start": v(111.06, -39.26) * mm, "end": v(111.12, -37.57) * mm});
            skLineSegment(sketch, "E1522", {"start": v(74.12, 46.97) * mm, "end": v(73.75, 46.67) * mm});
            skLineSegment(sketch, "E1523", {"start": v(71.03, 42.45) * mm, "end": v(70.89, 41.89) * mm});
            skLineSegment(sketch, "E1524", {"start": v(121.84, 42.44) * mm, "end": v(111.08, 45.37) * mm});
            skLineSegment(sketch, "E1525", {"start": v(87.3, -39.53) * mm, "end": v(86.11, -39.54) * mm});
            skLineSegment(sketch, "E1526", {"start": v(82.82, 44.6) * mm, "end": v(83.67, 44.82) * mm});
            skLineSegment(sketch, "E1527", {"start": v(77.4, 37.6) * mm, "end": v(77.37, 38.03) * mm});
            skLineSegment(sketch, "E1528", {"start": v(97.56, -34.03) * mm, "end": v(97.15, -34.71) * mm});
            skLineSegment(sketch, "E1529", {"start": v(97.83, -16.4) * mm, "end": v(98.58, -19.32) * mm});
            skLineSegment(sketch, "E1530", {"start": v(105.08, -50.72) * mm, "end": v(105.7, -50.3) * mm});
            skLineSegment(sketch, "E1531", {"start": v(110.94, -34) * mm, "end": v(110.7, -32.13) * mm});
            skLineSegment(sketch, "E1532", {"start": v(78.88, 49) * mm, "end": v(77.96, 48.78) * mm});
            skLineSegment(sketch, "E1533", {"start": v(71.2, 42.98) * mm, "end": v(71.03, 42.45) * mm});
            skLineSegment(sketch, "E1534", {"start": v(106.29, -49.84) * mm, "end": v(106.83, -49.35) * mm});
            skLineSegment(sketch, "E1535", {"start": v(86.11, -39.54) * mm, "end": v(84.9, -39.49) * mm});
            skLineSegment(sketch, "E1536", {"start": v(82.02, 44.33) * mm, "end": v(82.82, 44.6) * mm});
            skLineSegment(sketch, "E1537", {"start": v(77.37, 38.03) * mm, "end": v(77.37, 38.44) * mm});
            skLineSegment(sketch, "E1538", {"start": v(97.15, -34.71) * mm, "end": v(97.02, -34.9) * mm});
            skLineSegment(sketch, "E1539", {"start": v(73.96, 29.48) * mm, "end": v(85.74, 9.67) * mm});
            skLineSegment(sketch, "E1540", {"start": v(104.42, -51.12) * mm, "end": v(105.08, -50.72) * mm});
            skLineSegment(sketch, "E1541", {"start": v(110.61, -42.42) * mm, "end": v(110.9, -40.87) * mm});
            skLineSegment(sketch, "E1542", {"start": v(110.7, -32.13) * mm, "end": v(109.96, -28.24) * mm});
            skLineSegment(sketch, "E1543", {"start": v(77.96, 48.78) * mm, "end": v(77.06, 48.5) * mm});
            skLineSegment(sketch, "E1544", {"start": v(70.78, 41.3) * mm, "end": v(70.7, 40.68) * mm});
            skLineSegment(sketch, "E1545", {"start": v(79.67, 43.08) * mm, "end": v(79.96, 43.29) * mm});
            skLineSegment(sketch, "E1546", {"start": v(77.67, 40.3) * mm, "end": v(77.8, 40.64) * mm});
            skLineSegment(sketch, "E1547", {"start": v(84.9, -39.49) * mm, "end": v(82.39, -39.22) * mm});
            skLineSegment(sketch, "E1548", {"start": v(73.99, -50.05) * mm, "end": v(80.84, -51.84) * mm});
            skLineSegment(sketch, "E1549", {"start": v(77.37, 38.44) * mm, "end": v(77.4, 38.84) * mm});
            skLineSegment(sketch, "E1550", {"start": v(97.02, -34.9) * mm, "end": v(96.87, -35.1) * mm});
            skLineSegment(sketch, "E1551", {"start": v(99.13, -22.43) * mm, "end": v(99.3, -24.03) * mm});
            skLineSegment(sketch, "E1552", {"start": v(109.96, -28.24) * mm, "end": v(108.9, -24.18) * mm});
            skLineSegment(sketch, "E1553", {"start": v(91.05, 13.26) * mm, "end": v(82.88, 25.73) * mm});
            skLineSegment(sketch, "E1554", {"start": v(74.5, 47.25) * mm, "end": v(74.12, 46.97) * mm});
            skLineSegment(sketch, "E1555", {"start": v(71.61, 43.97) * mm, "end": v(71.4, 43.49) * mm});
            skLineSegment(sketch, "E1556", {"start": v(107.35, -48.84) * mm, "end": v(107.82, -48.3) * mm});
            skLineSegment(sketch, "E1557", {"start": v(78.45, 41.85) * mm, "end": v(78.66, 42.12) * mm});
            skLineSegment(sketch, "E1558", {"start": v(127.02, 38.3) * mm, "end": v(121.84, 42.44) * mm});
            skLineSegment(sketch, "E1559", {"start": v(88.44, -39.47) * mm, "end": v(87.3, -39.53) * mm});
            skLineSegment(sketch, "E1560", {"start": v(89.67, 45.42) * mm, "end": v(91.94, 45.38) * mm});
            skLineSegment(sketch, "E1561", {"start": v(37.72, -35.45) * mm, "end": v(57.7, -44.32) * mm});
            skLineSegment(sketch, "E1562", {"start": v(97.91, -33.33) * mm, "end": v(97.56, -34.03) * mm});
            skLineSegment(sketch, "E1563", {"start": v(98.58, -19.32) * mm, "end": v(99.13, -22.43) * mm});
            skLineSegment(sketch, "E1564", {"start": v(102.99, -51.83) * mm, "end": v(103.72, -51.49) * mm});
            skLineSegment(sketch, "E1565", {"start": v(91.62, -38.87) * mm, "end": v(90.6, -39.14) * mm});
            skLineSegment(sketch, "E1566", {"start": v(78.4, 33.63) * mm, "end": v(78, 34.71) * mm});
            skLineSegment(sketch, "E1567", {"start": v(70.64, 40.04) * mm, "end": v(70.62, 39.37) * mm});
            skLineSegment(sketch, "E1568", {"start": v(106.83, -49.35) * mm, "end": v(107.35, -48.84) * mm});
            skLineSegment(sketch, "E1569", {"start": v(80.27, 43.49) * mm, "end": v(80.59, 43.68) * mm});
            skLineSegment(sketch, "E1570", {"start": v(90.2, 49.21) * mm, "end": v(85.34, 49.44) * mm});
            skLineSegment(sketch, "E1571", {"start": v(86.89, -52.95) * mm, "end": v(89.62, -53.27) * mm});
            skLineSegment(sketch, "E1572", {"start": v(85.74, 9.67) * mm, "end": v(91.32, -0.5) * mm});
            skLineSegment(sketch, "E1573", {"start": v(110.9, -40.87) * mm, "end": v(111.06, -39.26) * mm});
            skLineSegment(sketch, "E1574", {"start": v(70.7, 40.68) * mm, "end": v(70.64, 40.04) * mm});
            skLineSegment(sketch, "E1575", {"start": v(79.96, 43.29) * mm, "end": v(80.27, 43.49) * mm});
            skLineSegment(sketch, "E1576", {"start": v(85.34, 49.44) * mm, "end": v(82.99, 49.4) * mm});
            skLineSegment(sketch, "E1577", {"start": v(74.42, -37.38) * mm, "end": v(69, -35.54) * mm});
            skLineSegment(sketch, "E1578", {"start": v(80.84, -51.84) * mm, "end": v(86.89, -52.95) * mm});
            skLineSegment(sketch, "E1579", {"start": v(77.5, 39.6) * mm, "end": v(77.57, 39.96) * mm});
            skLineSegment(sketch, "E1580", {"start": v(95.48, -36.56) * mm, "end": v(94.42, -37.48) * mm});
            skLineSegment(sketch, "E1581", {"start": v(127.02, 38.3) * mm, "end": v(111.93, 42.22) * mm});
            skLineSegment(sketch, "E1582", {"start": v(104.15, -11.43) * mm, "end": v(100.07, -2.82) * mm});
            skLineSegment(sketch, "E1583", {"start": v(109.39, -45.92) * mm, "end": v(109.7, -45.26) * mm});
            skLineSegment(sketch, "E1584", {"start": v(71.4, 43.49) * mm, "end": v(71.2, 42.98) * mm});
            skLineSegment(sketch, "E1585", {"start": v(81.28, 44.02) * mm, "end": v(82.02, 44.33) * mm});
            skLineSegment(sketch, "E1586", {"start": v(82.99, 49.4) * mm, "end": v(80.7, 49.26) * mm});
            skLineSegment(sketch, "E1587", {"start": v(69, -35.54) * mm, "end": v(63.77, -33.47) * mm});
            skLineSegment(sketch, "E1588", {"start": v(95.24, 48.64) * mm, "end": v(90.2, 49.21) * mm});
            skLineSegment(sketch, "E1589", {"start": v(-13.72, -7.48) * mm, "end": v(37.72, -35.45) * mm});
            skLineSegment(sketch, "E1590", {"start": v(77.57, 39.96) * mm, "end": v(77.67, 40.3) * mm});
            skLineSegment(sketch, "E1591", {"start": v(94.42, -37.48) * mm, "end": v(93.93, -37.84) * mm});
            skLineSegment(sketch, "E1592", {"start": v(103.72, -51.49) * mm, "end": v(104.42, -51.12) * mm});
            skLineSegment(sketch, "E1593", {"start": v(72.72, 45.65) * mm, "end": v(72.4, 45.27) * mm});
            skLineSegment(sketch, "E1594", {"start": v(100.07, -2.82) * mm, "end": v(91.05, 13.26) * mm});
            skLineSegment(sketch, "E1595", {"start": v(92.59, -38.52) * mm, "end": v(91.62, -38.87) * mm});
            skLineSegment(sketch, "E1596", {"start": v(79.4, 42.86) * mm, "end": v(79.67, 43.08) * mm});
            skLineSegment(sketch, "E1597", {"start": v(109.04, -46.55) * mm, "end": v(109.39, -45.92) * mm});
            skLineSegment(sketch, "E1598", {"start": v(77.8, 40.64) * mm, "end": v(77.93, 40.96) * mm});
            skLineSegment(sketch, "E1599", {"start": v(71.03, 36.39) * mm, "end": v(71.4, 35.15) * mm});
            skLineSegment(sketch, "E1600", {"start": v(54.66, -29.44) * mm, "end": v(33.32, -19) * mm});
            skLineSegment(sketch, "E1601", {"start": v(77.4, 38.84) * mm, "end": v(77.43, 39.23) * mm});
            skLineSegment(sketch, "E1602", {"start": v(98.93, -30.36) * mm, "end": v(98.73, -31.12) * mm});
            skLineSegment(sketch, "E1603", {"start": v(98.7, -53.06) * mm, "end": v(100.54, -52.66) * mm});
            skLineSegment(sketch, "E1604", {"start": v(93.7, -37.98) * mm, "end": v(93.5, -38.1) * mm});
            skLineSegment(sketch, "E1605", {"start": v(72.4, 45.27) * mm, "end": v(72.12, 44.86) * mm});
            skLineSegment(sketch, "E1606", {"start": v(108.9, -24.18) * mm, "end": v(107.55, -20) * mm});
            skLineSegment(sketch, "E1607", {"start": v(79.13, 42.62) * mm, "end": v(79.4, 42.86) * mm});
            skLineSegment(sketch, "E1608", {"start": v(82.88, 25.73) * mm, "end": v(80.95, 28.64) * mm});
            skLineSegment(sketch, "E1609", {"start": v(108.67, -47.16) * mm, "end": v(109.04, -46.55) * mm});
            skLineSegment(sketch, "E1610", {"start": v(77.93, 40.96) * mm, "end": v(78.08, 41.27) * mm});
            skLineSegment(sketch, "E1611", {"start": v(79.8, 49.16) * mm, "end": v(78.88, 49) * mm});
            skLineSegment(sketch, "E1612", {"start": v(70.76, 37.57) * mm, "end": v(71.03, 36.39) * mm});
            skLineSegment(sketch, "E1613", {"start": v(111.08, 45.37) * mm, "end": v(100.43, 47.77) * mm});
            skLineSegment(sketch, "E1614", {"start": v(33.32, -19) * mm, "end": v(13.03, -7.5) * mm});
            skLineSegment(sketch, "E1615", {"start": v(96.7, -53.32) * mm, "end": v(98.7, -53.06) * mm});
            skLineSegment(sketch, "E1616", {"start": v(99.2, -28.81) * mm, "end": v(98.93, -30.36) * mm});
            skSolve(sketch);
        }
        {
            var Q0;
            Q0 = qSketchRegion(id + "F16", true);
            extrude(context, id + "F17", {"entities" : qUnion([Q0]), "depth" : 2 * mm});
        }
        {
            var Q0;
            Q0=makeQuery(id+"F17.opExtrude","SWEPT_BODY",BODY,{"disambiguationData":[OSD([sQuery(id+"F16.wireOp",EDGE,"E1023.0"),sQuery(id+"F16.wireOp",EDGE,"E1024.0"),sQuery(id+"F16.wireOp",EDGE,"E1025.0"),sQuery(id+"F16.wireOp",EDGE,"E1026.0"),sQuery(id+"F16.wireOp",EDGE,"E1027.0"),sQuery(id+"F16.wireOp",EDGE,"E1028.0"),sQuery(id+"F16.wireOp",EDGE,"E1029.0"),sQuery(id+"F16.wireOp",EDGE,"E1030.0"),sQuery(id+"F16.wireOp",EDGE,"E1031.0"),sQuery(id+"F16.wireOp",EDGE,"E1032.0"),sQuery(id+"F16.wireOp",EDGE,"E1033.0"),sQuery(id+"F16.wireOp",EDGE,"E1034.0"),sQuery(id+"F16.wireOp",EDGE,"E1035.0"),sQuery(id+"F16.wireOp",EDGE,"E1036.0"),sQuery(id+"F16.wireOp",EDGE,"E1037.0"),sQuery(id+"F16.wireOp",EDGE,"E1038.0"),sQuery(id+"F16.wireOp",EDGE,"E1039.0"),sQuery(id+"F16.wireOp",EDGE,"E1040.0"),sQuery(id+"F16.wireOp",EDGE,"E1041.0"),sQuery(id+"F16.wireOp",EDGE,"E1042.0"),sQuery(id+"F16.wireOp",EDGE,"E1043.0"),sQuery(id+"F16.wireOp",EDGE,"E1044.0"),sQuery(id+"F16.wireOp",EDGE,"E1045.0"),sQuery(id+"F16.wireOp",EDGE,"E1046.0"),sQuery(id+"F16.wireOp",EDGE,"E1047.0"),sQuery(id+"F16.wireOp",EDGE,"E1048.0"),sQuery(id+"F16.wireOp",EDGE,"E1049.0"),sQuery(id+"F16.wireOp",EDGE,"E1050.0"),sQuery(id+"F16.wireOp",EDGE,"E1051.0"),sQuery(id+"F16.wireOp",EDGE,"E1052.0")])]});
            var Q1;
            Q1=makeQuery(id+"F17.opExtrude","SWEPT_BODY",BODY,{"disambiguationData":[OSD([sQuery(id+"F16.wireOp",EDGE,"E1053"),sQuery(id+"F16.wireOp",EDGE,"E1054"),sQuery(id+"F16.wireOp",EDGE,"E1055"),sQuery(id+"F16.wireOp",EDGE,"E1056"),sQuery(id+"F16.wireOp",EDGE,"E1057"),sQuery(id+"F16.wireOp",EDGE,"E1058"),sQuery(id+"F16.wireOp",EDGE,"E1059"),sQuery(id+"F16.wireOp",EDGE,"E1060"),sQuery(id+"F16.wireOp",EDGE,"E1061"),sQuery(id+"F16.wireOp",EDGE,"E1062"),sQuery(id+"F16.wireOp",EDGE,"E1063"),sQuery(id+"F16.wireOp",EDGE,"E1064"),sQuery(id+"F16.wireOp",EDGE,"E1065"),sQuery(id+"F16.wireOp",EDGE,"E1066"),sQuery(id+"F16.wireOp",EDGE,"E1067"),sQuery(id+"F16.wireOp",EDGE,"E1068"),sQuery(id+"F16.wireOp",EDGE,"E1069"),sQuery(id+"F16.wireOp",EDGE,"E1070"),sQuery(id+"F16.wireOp",EDGE,"E1071"),sQuery(id+"F16.wireOp",EDGE,"E1072"),sQuery(id+"F16.wireOp",EDGE,"E1073"),sQuery(id+"F16.wireOp",EDGE,"E1074"),sQuery(id+"F16.wireOp",EDGE,"E1075"),sQuery(id+"F16.wireOp",EDGE,"E1076"),sQuery(id+"F16.wireOp",EDGE,"E1077"),sQuery(id+"F16.wireOp",EDGE,"E1078")])]});
            var Q2;
            Q2=makeQuery(id+"F17.opExtrude","SWEPT_BODY",BODY,{"disambiguationData":[OSD([sQuery(id+"F16.wireOp",EDGE,"E1079"),sQuery(id+"F16.wireOp",EDGE,"E1080"),sQuery(id+"F16.wireOp",EDGE,"E1081"),sQuery(id+"F16.wireOp",EDGE,"E1082"),sQuery(id+"F16.wireOp",EDGE,"E1083"),sQuery(id+"F16.wireOp",EDGE,"E1084"),sQuery(id+"F16.wireOp",EDGE,"E1085"),sQuery(id+"F16.wireOp",EDGE,"E1086"),sQuery(id+"F16.wireOp",EDGE,"E1087"),sQuery(id+"F16.wireOp",EDGE,"E1088"),sQuery(id+"F16.wireOp",EDGE,"E1089"),sQuery(id+"F16.wireOp",EDGE,"E1090"),sQuery(id+"F16.wireOp",EDGE,"E1091"),sQuery(id+"F16.wireOp",EDGE,"E1092"),sQuery(id+"F16.wireOp",EDGE,"E1093"),sQuery(id+"F16.wireOp",EDGE,"E1094"),sQuery(id+"F16.wireOp",EDGE,"E1095"),sQuery(id+"F16.wireOp",EDGE,"E1096"),sQuery(id+"F16.wireOp",EDGE,"E1097"),sQuery(id+"F16.wireOp",EDGE,"E1098"),sQuery(id+"F16.wireOp",EDGE,"E1099"),sQuery(id+"F16.wireOp",EDGE,"E1100"),sQuery(id+"F16.wireOp",EDGE,"E1101"),sQuery(id+"F16.wireOp",EDGE,"E1102"),sQuery(id+"F16.wireOp",EDGE,"E1103"),sQuery(id+"F16.wireOp",EDGE,"E1104"),sQuery(id+"F16.wireOp",EDGE,"E1105"),sQuery(id+"F16.wireOp",EDGE,"E1106"),sQuery(id+"F16.wireOp",EDGE,"E1107"),sQuery(id+"F16.wireOp",EDGE,"E1108"),sQuery(id+"F16.wireOp",EDGE,"E1109"),sQuery(id+"F16.wireOp",EDGE,"E1110"),sQuery(id+"F16.wireOp",EDGE,"E1111"),sQuery(id+"F16.wireOp",EDGE,"E1112"),sQuery(id+"F16.wireOp",EDGE,"E1113"),sQuery(id+"F16.wireOp",EDGE,"E1114"),sQuery(id+"F16.wireOp",EDGE,"E1115"),sQuery(id+"F16.wireOp",EDGE,"E1116"),sQuery(id+"F16.wireOp",EDGE,"E1117"),sQuery(id+"F16.wireOp",EDGE,"E1118"),sQuery(id+"F16.wireOp",EDGE,"E1119"),sQuery(id+"F16.wireOp",EDGE,"E1120"),sQuery(id+"F16.wireOp",EDGE,"E1121"),sQuery(id+"F16.wireOp",EDGE,"E1122"),sQuery(id+"F16.wireOp",EDGE,"E1123"),sQuery(id+"F16.wireOp",EDGE,"E1124"),sQuery(id+"F16.wireOp",EDGE,"E1125"),sQuery(id+"F16.wireOp",EDGE,"E1126"),sQuery(id+"F16.wireOp",EDGE,"E1127"),sQuery(id+"F16.wireOp",EDGE,"E1128"),sQuery(id+"F16.wireOp",EDGE,"E1129"),sQuery(id+"F16.wireOp",EDGE,"E1130"),sQuery(id+"F16.wireOp",EDGE,"E1131"),sQuery(id+"F16.wireOp",EDGE,"E1132"),sQuery(id+"F16.wireOp",EDGE,"E1133"),sQuery(id+"F16.wireOp",EDGE,"E1134"),sQuery(id+"F16.wireOp",EDGE,"E1135"),sQuery(id+"F16.wireOp",EDGE,"E1136"),sQuery(id+"F16.wireOp",EDGE,"E1137"),sQuery(id+"F16.wireOp",EDGE,"E1138"),sQuery(id+"F16.wireOp",EDGE,"E1139"),sQuery(id+"F16.wireOp",EDGE,"E1140"),sQuery(id+"F16.wireOp",EDGE,"E1141"),sQuery(id+"F16.wireOp",EDGE,"E1142"),sQuery(id+"F16.wireOp",EDGE,"E1143"),sQuery(id+"F16.wireOp",EDGE,"E1144"),sQuery(id+"F16.wireOp",EDGE,"E1145"),sQuery(id+"F16.wireOp",EDGE,"E1146"),sQuery(id+"F16.wireOp",EDGE,"E1147"),sQuery(id+"F16.wireOp",EDGE,"E1148"),sQuery(id+"F16.wireOp",EDGE,"E1149"),sQuery(id+"F16.wireOp",EDGE,"E1150"),sQuery(id+"F16.wireOp",EDGE,"E1151"),sQuery(id+"F16.wireOp",EDGE,"E1152"),sQuery(id+"F16.wireOp",EDGE,"E1153"),sQuery(id+"F16.wireOp",EDGE,"E1154"),sQuery(id+"F16.wireOp",EDGE,"E1155"),sQuery(id+"F16.wireOp",EDGE,"E1156"),sQuery(id+"F16.wireOp",EDGE,"E1157"),sQuery(id+"F16.wireOp",EDGE,"E1158"),sQuery(id+"F16.wireOp",EDGE,"E1159"),sQuery(id+"F16.wireOp",EDGE,"E1160"),sQuery(id+"F16.wireOp",EDGE,"E1161"),sQuery(id+"F16.wireOp",EDGE,"E1162"),sQuery(id+"F16.wireOp",EDGE,"E1163"),sQuery(id+"F16.wireOp",EDGE,"E1164"),sQuery(id+"F16.wireOp",EDGE,"E1165"),sQuery(id+"F16.wireOp",EDGE,"E1166"),sQuery(id+"F16.wireOp",EDGE,"E1167"),sQuery(id+"F16.wireOp",EDGE,"E1168"),sQuery(id+"F16.wireOp",EDGE,"E1169"),sQuery(id+"F16.wireOp",EDGE,"E1170"),sQuery(id+"F16.wireOp",EDGE,"E1171"),sQuery(id+"F16.wireOp",EDGE,"E1172"),sQuery(id+"F16.wireOp",EDGE,"E1173"),sQuery(id+"F16.wireOp",EDGE,"E1174"),sQuery(id+"F16.wireOp",EDGE,"E1175"),sQuery(id+"F16.wireOp",EDGE,"E1176"),sQuery(id+"F16.wireOp",EDGE,"E1177"),sQuery(id+"F16.wireOp",EDGE,"E1178"),sQuery(id+"F16.wireOp",EDGE,"E1179"),sQuery(id+"F16.wireOp",EDGE,"E1180"),sQuery(id+"F16.wireOp",EDGE,"E1181"),sQuery(id+"F16.wireOp",EDGE,"E1182"),sQuery(id+"F16.wireOp",EDGE,"E1183"),sQuery(id+"F16.wireOp",EDGE,"E1184"),sQuery(id+"F16.wireOp",EDGE,"E1185"),sQuery(id+"F16.wireOp",EDGE,"E1186"),sQuery(id+"F16.wireOp",EDGE,"E1187"),sQuery(id+"F16.wireOp",EDGE,"E1188"),sQuery(id+"F16.wireOp",EDGE,"E1189"),sQuery(id+"F16.wireOp",EDGE,"E1190"),sQuery(id+"F16.wireOp",EDGE,"E1191"),sQuery(id+"F16.wireOp",EDGE,"E1192"),sQuery(id+"F16.wireOp",EDGE,"E1193"),sQuery(id+"F16.wireOp",EDGE,"E1194"),sQuery(id+"F16.wireOp",EDGE,"E1195"),sQuery(id+"F16.wireOp",EDGE,"E1196"),sQuery(id+"F16.wireOp",EDGE,"E1197"),sQuery(id+"F16.wireOp",EDGE,"E1198"),sQuery(id+"F16.wireOp",EDGE,"E1199"),sQuery(id+"F16.wireOp",EDGE,"E1200"),sQuery(id+"F16.wireOp",EDGE,"E1201"),sQuery(id+"F16.wireOp",EDGE,"E1202"),sQuery(id+"F16.wireOp",EDGE,"E1203"),sQuery(id+"F16.wireOp",EDGE,"E1204"),sQuery(id+"F16.wireOp",EDGE,"E1205"),sQuery(id+"F16.wireOp",EDGE,"E1206"),sQuery(id+"F16.wireOp",EDGE,"E1207"),sQuery(id+"F16.wireOp",EDGE,"E1208"),sQuery(id+"F16.wireOp",EDGE,"E1209"),sQuery(id+"F16.wireOp",EDGE,"E1210"),sQuery(id+"F16.wireOp",EDGE,"E1211"),sQuery(id+"F16.wireOp",EDGE,"E1212"),sQuery(id+"F16.wireOp",EDGE,"E1213"),sQuery(id+"F16.wireOp",EDGE,"E1214"),sQuery(id+"F16.wireOp",EDGE,"E1215"),sQuery(id+"F16.wireOp",EDGE,"E1216"),sQuery(id+"F16.wireOp",EDGE,"E1217"),sQuery(id+"F16.wireOp",EDGE,"E1218"),sQuery(id+"F16.wireOp",EDGE,"E1219"),sQuery(id+"F16.wireOp",EDGE,"E1220"),sQuery(id+"F16.wireOp",EDGE,"E1221"),sQuery(id+"F16.wireOp",EDGE,"E1222"),sQuery(id+"F16.wireOp",EDGE,"E1223"),sQuery(id+"F16.wireOp",EDGE,"E1224"),sQuery(id+"F16.wireOp",EDGE,"E1225"),sQuery(id+"F16.wireOp",EDGE,"E1226"),sQuery(id+"F16.wireOp",EDGE,"E1227"),sQuery(id+"F16.wireOp",EDGE,"E1228"),sQuery(id+"F16.wireOp",EDGE,"E1229"),sQuery(id+"F16.wireOp",EDGE,"E1230"),sQuery(id+"F16.wireOp",EDGE,"E1231"),sQuery(id+"F16.wireOp",EDGE,"E1232"),sQuery(id+"F16.wireOp",EDGE,"E1233"),sQuery(id+"F16.wireOp",EDGE,"E1234"),sQuery(id+"F16.wireOp",EDGE,"E1235"),sQuery(id+"F16.wireOp",EDGE,"E1236"),sQuery(id+"F16.wireOp",EDGE,"E1237"),sQuery(id+"F16.wireOp",EDGE,"E1238"),sQuery(id+"F16.wireOp",EDGE,"E1239"),sQuery(id+"F16.wireOp",EDGE,"E1240"),sQuery(id+"F16.wireOp",EDGE,"E1241"),sQuery(id+"F16.wireOp",EDGE,"E1242"),sQuery(id+"F16.wireOp",EDGE,"E1243"),sQuery(id+"F16.wireOp",EDGE,"E1244"),sQuery(id+"F16.wireOp",EDGE,"E1245"),sQuery(id+"F16.wireOp",EDGE,"E1246"),sQuery(id+"F16.wireOp",EDGE,"E1247"),sQuery(id+"F16.wireOp",EDGE,"E1248"),sQuery(id+"F16.wireOp",EDGE,"E1249"),sQuery(id+"F16.wireOp",EDGE,"E1250"),sQuery(id+"F16.wireOp",EDGE,"E1251"),sQuery(id+"F16.wireOp",EDGE,"E1252"),sQuery(id+"F16.wireOp",EDGE,"E1253"),sQuery(id+"F16.wireOp",EDGE,"E1254"),sQuery(id+"F16.wireOp",EDGE,"E1255"),sQuery(id+"F16.wireOp",EDGE,"E1256"),sQuery(id+"F16.wireOp",EDGE,"E1257"),sQuery(id+"F16.wireOp",EDGE,"E1258"),sQuery(id+"F16.wireOp",EDGE,"E1259"),sQuery(id+"F16.wireOp",EDGE,"E1260"),sQuery(id+"F16.wireOp",EDGE,"E1261"),sQuery(id+"F16.wireOp",EDGE,"E1262"),sQuery(id+"F16.wireOp",EDGE,"E1263"),sQuery(id+"F16.wireOp",EDGE,"E1264"),sQuery(id+"F16.wireOp",EDGE,"E1265"),sQuery(id+"F16.wireOp",EDGE,"E1266"),sQuery(id+"F16.wireOp",EDGE,"E1267"),sQuery(id+"F16.wireOp",EDGE,"E1268"),sQuery(id+"F16.wireOp",EDGE,"E1269"),sQuery(id+"F16.wireOp",EDGE,"E1270"),sQuery(id+"F16.wireOp",EDGE,"E1271"),sQuery(id+"F16.wireOp",EDGE,"E1272"),sQuery(id+"F16.wireOp",EDGE,"E1273"),sQuery(id+"F16.wireOp",EDGE,"E1274"),sQuery(id+"F16.wireOp",EDGE,"E1275"),sQuery(id+"F16.wireOp",EDGE,"E1276"),sQuery(id+"F16.wireOp",EDGE,"E1277"),sQuery(id+"F16.wireOp",EDGE,"E1278"),sQuery(id+"F16.wireOp",EDGE,"E1279"),sQuery(id+"F16.wireOp",EDGE,"E1280"),sQuery(id+"F16.wireOp",EDGE,"E1281"),sQuery(id+"F16.wireOp",EDGE,"E1282"),sQuery(id+"F16.wireOp",EDGE,"E1283")])]});
            var Q3;
            Q3=makeQuery(id+"F17.opExtrude","SWEPT_BODY",BODY,{"disambiguationData":[OSD([sQuery(id+"F16.wireOp",EDGE,"E1284"),sQuery(id+"F16.wireOp",EDGE,"E1285"),sQuery(id+"F16.wireOp",EDGE,"E1286"),sQuery(id+"F16.wireOp",EDGE,"E1287"),sQuery(id+"F16.wireOp",EDGE,"E1288"),sQuery(id+"F16.wireOp",EDGE,"E1289"),sQuery(id+"F16.wireOp",EDGE,"E1290"),sQuery(id+"F16.wireOp",EDGE,"E1291"),sQuery(id+"F16.wireOp",EDGE,"E1292"),sQuery(id+"F16.wireOp",EDGE,"E1293"),sQuery(id+"F16.wireOp",EDGE,"E1294"),sQuery(id+"F16.wireOp",EDGE,"E1295"),sQuery(id+"F16.wireOp",EDGE,"E1296"),sQuery(id+"F16.wireOp",EDGE,"E1297"),sQuery(id+"F16.wireOp",EDGE,"E1298"),sQuery(id+"F16.wireOp",EDGE,"E1299"),sQuery(id+"F16.wireOp",EDGE,"E1300"),sQuery(id+"F16.wireOp",EDGE,"E1301"),sQuery(id+"F16.wireOp",EDGE,"E1302"),sQuery(id+"F16.wireOp",EDGE,"E1303"),sQuery(id+"F16.wireOp",EDGE,"E1304"),sQuery(id+"F16.wireOp",EDGE,"E1305"),sQuery(id+"F16.wireOp",EDGE,"E1306"),sQuery(id+"F16.wireOp",EDGE,"E1307"),sQuery(id+"F16.wireOp",EDGE,"E1308"),sQuery(id+"F16.wireOp",EDGE,"E1309"),sQuery(id+"F16.wireOp",EDGE,"E1310"),sQuery(id+"F16.wireOp",EDGE,"E1311"),sQuery(id+"F16.wireOp",EDGE,"E1312"),sQuery(id+"F16.wireOp",EDGE,"E1313"),sQuery(id+"F16.wireOp",EDGE,"E1314"),sQuery(id+"F16.wireOp",EDGE,"E1315"),sQuery(id+"F16.wireOp",EDGE,"E1316"),sQuery(id+"F16.wireOp",EDGE,"E1317"),sQuery(id+"F16.wireOp",EDGE,"E1318"),sQuery(id+"F16.wireOp",EDGE,"E1319"),sQuery(id+"F16.wireOp",EDGE,"E1320"),sQuery(id+"F16.wireOp",EDGE,"E1321"),sQuery(id+"F16.wireOp",EDGE,"E1322"),sQuery(id+"F16.wireOp",EDGE,"E1323"),sQuery(id+"F16.wireOp",EDGE,"E1324"),sQuery(id+"F16.wireOp",EDGE,"E1325"),sQuery(id+"F16.wireOp",EDGE,"E1326"),sQuery(id+"F16.wireOp",EDGE,"E1327"),sQuery(id+"F16.wireOp",EDGE,"E1328"),sQuery(id+"F16.wireOp",EDGE,"E1329"),sQuery(id+"F16.wireOp",EDGE,"E1330"),sQuery(id+"F16.wireOp",EDGE,"E1331"),sQuery(id+"F16.wireOp",EDGE,"E1332"),sQuery(id+"F16.wireOp",EDGE,"E1333"),sQuery(id+"F16.wireOp",EDGE,"E1334"),sQuery(id+"F16.wireOp",EDGE,"E1335"),sQuery(id+"F16.wireOp",EDGE,"E1336"),sQuery(id+"F16.wireOp",EDGE,"E1337"),sQuery(id+"F16.wireOp",EDGE,"E1338"),sQuery(id+"F16.wireOp",EDGE,"E1339"),sQuery(id+"F16.wireOp",EDGE,"E1340"),sQuery(id+"F16.wireOp",EDGE,"E1341"),sQuery(id+"F16.wireOp",EDGE,"E1342"),sQuery(id+"F16.wireOp",EDGE,"E1343"),sQuery(id+"F16.wireOp",EDGE,"E1344"),sQuery(id+"F16.wireOp",EDGE,"E1345"),sQuery(id+"F16.wireOp",EDGE,"E1346"),sQuery(id+"F16.wireOp",EDGE,"E1347"),sQuery(id+"F16.wireOp",EDGE,"E1348"),sQuery(id+"F16.wireOp",EDGE,"E1349"),sQuery(id+"F16.wireOp",EDGE,"E1350"),sQuery(id+"F16.wireOp",EDGE,"E1351"),sQuery(id+"F16.wireOp",EDGE,"E1352"),sQuery(id+"F16.wireOp",EDGE,"E1353"),sQuery(id+"F16.wireOp",EDGE,"E1354"),sQuery(id+"F16.wireOp",EDGE,"E1355"),sQuery(id+"F16.wireOp",EDGE,"E1356"),sQuery(id+"F16.wireOp",EDGE,"E1357"),sQuery(id+"F16.wireOp",EDGE,"E1358"),sQuery(id+"F16.wireOp",EDGE,"E1359"),sQuery(id+"F16.wireOp",EDGE,"E1360"),sQuery(id+"F16.wireOp",EDGE,"E1361"),sQuery(id+"F16.wireOp",EDGE,"E1362"),sQuery(id+"F16.wireOp",EDGE,"E1363"),sQuery(id+"F16.wireOp",EDGE,"E1364"),sQuery(id+"F16.wireOp",EDGE,"E1365"),sQuery(id+"F16.wireOp",EDGE,"E1366"),sQuery(id+"F16.wireOp",EDGE,"E1367"),sQuery(id+"F16.wireOp",EDGE,"E1368"),sQuery(id+"F16.wireOp",EDGE,"E1369"),sQuery(id+"F16.wireOp",EDGE,"E1370"),sQuery(id+"F16.wireOp",EDGE,"E1371"),sQuery(id+"F16.wireOp",EDGE,"E1372"),sQuery(id+"F16.wireOp",EDGE,"E1373"),sQuery(id+"F16.wireOp",EDGE,"E1374"),sQuery(id+"F16.wireOp",EDGE,"E1375"),sQuery(id+"F16.wireOp",EDGE,"E1376"),sQuery(id+"F16.wireOp",EDGE,"E1377"),sQuery(id+"F16.wireOp",EDGE,"E1378"),sQuery(id+"F16.wireOp",EDGE,"E1379"),sQuery(id+"F16.wireOp",EDGE,"E1380"),sQuery(id+"F16.wireOp",EDGE,"E1381"),sQuery(id+"F16.wireOp",EDGE,"E1382"),sQuery(id+"F16.wireOp",EDGE,"E1383"),sQuery(id+"F16.wireOp",EDGE,"E1384"),sQuery(id+"F16.wireOp",EDGE,"E1385"),sQuery(id+"F16.wireOp",EDGE,"E1386"),sQuery(id+"F16.wireOp",EDGE,"E1387"),sQuery(id+"F16.wireOp",EDGE,"E1388"),sQuery(id+"F16.wireOp",EDGE,"E1389"),sQuery(id+"F16.wireOp",EDGE,"E1390"),sQuery(id+"F16.wireOp",EDGE,"E1391"),sQuery(id+"F16.wireOp",EDGE,"E1392"),sQuery(id+"F16.wireOp",EDGE,"E1393"),sQuery(id+"F16.wireOp",EDGE,"E1394"),sQuery(id+"F16.wireOp",EDGE,"E1395"),sQuery(id+"F16.wireOp",EDGE,"E1396"),sQuery(id+"F16.wireOp",EDGE,"E1397"),sQuery(id+"F16.wireOp",EDGE,"E1398"),sQuery(id+"F16.wireOp",EDGE,"E1399"),sQuery(id+"F16.wireOp",EDGE,"E1400"),sQuery(id+"F16.wireOp",EDGE,"E1401"),sQuery(id+"F16.wireOp",EDGE,"E1402"),sQuery(id+"F16.wireOp",EDGE,"E1403"),sQuery(id+"F16.wireOp",EDGE,"E1404"),sQuery(id+"F16.wireOp",EDGE,"E1405"),sQuery(id+"F16.wireOp",EDGE,"E1406"),sQuery(id+"F16.wireOp",EDGE,"E1407"),sQuery(id+"F16.wireOp",EDGE,"E1408"),sQuery(id+"F16.wireOp",EDGE,"E1409"),sQuery(id+"F16.wireOp",EDGE,"E1410"),sQuery(id+"F16.wireOp",EDGE,"E1411"),sQuery(id+"F16.wireOp",EDGE,"E1412"),sQuery(id+"F16.wireOp",EDGE,"E1413"),sQuery(id+"F16.wireOp",EDGE,"E1414"),sQuery(id+"F16.wireOp",EDGE,"E1415"),sQuery(id+"F16.wireOp",EDGE,"E1416"),sQuery(id+"F16.wireOp",EDGE,"E1417"),sQuery(id+"F16.wireOp",EDGE,"E1418"),sQuery(id+"F16.wireOp",EDGE,"E1419"),sQuery(id+"F16.wireOp",EDGE,"E1420"),sQuery(id+"F16.wireOp",EDGE,"E1421"),sQuery(id+"F16.wireOp",EDGE,"E1422"),sQuery(id+"F16.wireOp",EDGE,"E1423"),sQuery(id+"F16.wireOp",EDGE,"E1424"),sQuery(id+"F16.wireOp",EDGE,"E1425"),sQuery(id+"F16.wireOp",EDGE,"E1426"),sQuery(id+"F16.wireOp",EDGE,"E1427"),sQuery(id+"F16.wireOp",EDGE,"E1428"),sQuery(id+"F16.wireOp",EDGE,"E1429"),sQuery(id+"F16.wireOp",EDGE,"E1430"),sQuery(id+"F16.wireOp",EDGE,"E1431"),sQuery(id+"F16.wireOp",EDGE,"E1432"),sQuery(id+"F16.wireOp",EDGE,"E1433"),sQuery(id+"F16.wireOp",EDGE,"E1434"),sQuery(id+"F16.wireOp",EDGE,"E1435"),sQuery(id+"F16.wireOp",EDGE,"E1436"),sQuery(id+"F16.wireOp",EDGE,"E1437"),sQuery(id+"F16.wireOp",EDGE,"E1438"),sQuery(id+"F16.wireOp",EDGE,"E1439"),sQuery(id+"F16.wireOp",EDGE,"E1440"),sQuery(id+"F16.wireOp",EDGE,"E1441"),sQuery(id+"F16.wireOp",EDGE,"E1442"),sQuery(id+"F16.wireOp",EDGE,"E1443"),sQuery(id+"F16.wireOp",EDGE,"E1444"),sQuery(id+"F16.wireOp",EDGE,"E1445"),sQuery(id+"F16.wireOp",EDGE,"E1446")])]});
            var Q4;
            Q4=makeQuery(id+"F17.opExtrude","SWEPT_BODY",BODY,{"disambiguationData":[OSD([sQuery(id+"F16.wireOp",EDGE,"E1447"),sQuery(id+"F16.wireOp",EDGE,"E1448"),sQuery(id+"F16.wireOp",EDGE,"E1449"),sQuery(id+"F16.wireOp",EDGE,"E1450"),sQuery(id+"F16.wireOp",EDGE,"E1451"),sQuery(id+"F16.wireOp",EDGE,"E1452"),sQuery(id+"F16.wireOp",EDGE,"E1453"),sQuery(id+"F16.wireOp",EDGE,"E1454"),sQuery(id+"F16.wireOp",EDGE,"E1455"),sQuery(id+"F16.wireOp",EDGE,"E1456"),sQuery(id+"F16.wireOp",EDGE,"E1457"),sQuery(id+"F16.wireOp",EDGE,"E1458"),sQuery(id+"F16.wireOp",EDGE,"E1459"),sQuery(id+"F16.wireOp",EDGE,"E1460"),sQuery(id+"F16.wireOp",EDGE,"E1461"),sQuery(id+"F16.wireOp",EDGE,"E1462"),sQuery(id+"F16.wireOp",EDGE,"E1463"),sQuery(id+"F16.wireOp",EDGE,"E1464"),sQuery(id+"F16.wireOp",EDGE,"E1465"),sQuery(id+"F16.wireOp",EDGE,"E1466"),sQuery(id+"F16.wireOp",EDGE,"E1467"),sQuery(id+"F16.wireOp",EDGE,"E1468"),sQuery(id+"F16.wireOp",EDGE,"E1469"),sQuery(id+"F16.wireOp",EDGE,"E1470"),sQuery(id+"F16.wireOp",EDGE,"E1471"),sQuery(id+"F16.wireOp",EDGE,"E1472"),sQuery(id+"F16.wireOp",EDGE,"E1473"),sQuery(id+"F16.wireOp",EDGE,"E1474"),sQuery(id+"F16.wireOp",EDGE,"E1475"),sQuery(id+"F16.wireOp",EDGE,"E1476"),sQuery(id+"F16.wireOp",EDGE,"E1477"),sQuery(id+"F16.wireOp",EDGE,"E1478"),sQuery(id+"F16.wireOp",EDGE,"E1479"),sQuery(id+"F16.wireOp",EDGE,"E1480"),sQuery(id+"F16.wireOp",EDGE,"E1481"),sQuery(id+"F16.wireOp",EDGE,"E1482"),sQuery(id+"F16.wireOp",EDGE,"E1483"),sQuery(id+"F16.wireOp",EDGE,"E1484"),sQuery(id+"F16.wireOp",EDGE,"E1485"),sQuery(id+"F16.wireOp",EDGE,"E1486"),sQuery(id+"F16.wireOp",EDGE,"E1487"),sQuery(id+"F16.wireOp",EDGE,"E1488"),sQuery(id+"F16.wireOp",EDGE,"E1489"),sQuery(id+"F16.wireOp",EDGE,"E1490"),sQuery(id+"F16.wireOp",EDGE,"E1491"),sQuery(id+"F16.wireOp",EDGE,"E1492"),sQuery(id+"F16.wireOp",EDGE,"E1493"),sQuery(id+"F16.wireOp",EDGE,"E1494"),sQuery(id+"F16.wireOp",EDGE,"E1495"),sQuery(id+"F16.wireOp",EDGE,"E1496"),sQuery(id+"F16.wireOp",EDGE,"E1497"),sQuery(id+"F16.wireOp",EDGE,"E1498"),sQuery(id+"F16.wireOp",EDGE,"E1499"),sQuery(id+"F16.wireOp",EDGE,"E1500"),sQuery(id+"F16.wireOp",EDGE,"E1501"),sQuery(id+"F16.wireOp",EDGE,"E1502"),sQuery(id+"F16.wireOp",EDGE,"E1503"),sQuery(id+"F16.wireOp",EDGE,"E1504"),sQuery(id+"F16.wireOp",EDGE,"E1505"),sQuery(id+"F16.wireOp",EDGE,"E1506"),sQuery(id+"F16.wireOp",EDGE,"E1507"),sQuery(id+"F16.wireOp",EDGE,"E1508"),sQuery(id+"F16.wireOp",EDGE,"E1509"),sQuery(id+"F16.wireOp",EDGE,"E1510"),sQuery(id+"F16.wireOp",EDGE,"E1511"),sQuery(id+"F16.wireOp",EDGE,"E1512"),sQuery(id+"F16.wireOp",EDGE,"E1513"),sQuery(id+"F16.wireOp",EDGE,"E1514"),sQuery(id+"F16.wireOp",EDGE,"E1515"),sQuery(id+"F16.wireOp",EDGE,"E1516"),sQuery(id+"F16.wireOp",EDGE,"E1517"),sQuery(id+"F16.wireOp",EDGE,"E1518"),sQuery(id+"F16.wireOp",EDGE,"E1519"),sQuery(id+"F16.wireOp",EDGE,"E1520"),sQuery(id+"F16.wireOp",EDGE,"E1521"),sQuery(id+"F16.wireOp",EDGE,"E1522"),sQuery(id+"F16.wireOp",EDGE,"E1523"),sQuery(id+"F16.wireOp",EDGE,"E1524"),sQuery(id+"F16.wireOp",EDGE,"E1525"),sQuery(id+"F16.wireOp",EDGE,"E1526"),sQuery(id+"F16.wireOp",EDGE,"E1527"),sQuery(id+"F16.wireOp",EDGE,"E1528"),sQuery(id+"F16.wireOp",EDGE,"E1529"),sQuery(id+"F16.wireOp",EDGE,"E1530"),sQuery(id+"F16.wireOp",EDGE,"E1531"),sQuery(id+"F16.wireOp",EDGE,"E1532"),sQuery(id+"F16.wireOp",EDGE,"E1533"),sQuery(id+"F16.wireOp",EDGE,"E1534"),sQuery(id+"F16.wireOp",EDGE,"E1535"),sQuery(id+"F16.wireOp",EDGE,"E1536"),sQuery(id+"F16.wireOp",EDGE,"E1537"),sQuery(id+"F16.wireOp",EDGE,"E1538"),sQuery(id+"F16.wireOp",EDGE,"E1539"),sQuery(id+"F16.wireOp",EDGE,"E1540"),sQuery(id+"F16.wireOp",EDGE,"E1541"),sQuery(id+"F16.wireOp",EDGE,"E1542"),sQuery(id+"F16.wireOp",EDGE,"E1543"),sQuery(id+"F16.wireOp",EDGE,"E1544"),sQuery(id+"F16.wireOp",EDGE,"E1545"),sQuery(id+"F16.wireOp",EDGE,"E1546"),sQuery(id+"F16.wireOp",EDGE,"E1547"),sQuery(id+"F16.wireOp",EDGE,"E1548"),sQuery(id+"F16.wireOp",EDGE,"E1549"),sQuery(id+"F16.wireOp",EDGE,"E1550"),sQuery(id+"F16.wireOp",EDGE,"E1551"),sQuery(id+"F16.wireOp",EDGE,"E1552"),sQuery(id+"F16.wireOp",EDGE,"E1553"),sQuery(id+"F16.wireOp",EDGE,"E1554"),sQuery(id+"F16.wireOp",EDGE,"E1555"),sQuery(id+"F16.wireOp",EDGE,"E1556"),sQuery(id+"F16.wireOp",EDGE,"E1557"),sQuery(id+"F16.wireOp",EDGE,"E1558"),sQuery(id+"F16.wireOp",EDGE,"E1559"),sQuery(id+"F16.wireOp",EDGE,"E1560"),sQuery(id+"F16.wireOp",EDGE,"E1561"),sQuery(id+"F16.wireOp",EDGE,"E1562"),sQuery(id+"F16.wireOp",EDGE,"E1563"),sQuery(id+"F16.wireOp",EDGE,"E1564"),sQuery(id+"F16.wireOp",EDGE,"E1565"),sQuery(id+"F16.wireOp",EDGE,"E1566"),sQuery(id+"F16.wireOp",EDGE,"E1567"),sQuery(id+"F16.wireOp",EDGE,"E1568"),sQuery(id+"F16.wireOp",EDGE,"E1569"),sQuery(id+"F16.wireOp",EDGE,"E1570"),sQuery(id+"F16.wireOp",EDGE,"E1571"),sQuery(id+"F16.wireOp",EDGE,"E1572"),sQuery(id+"F16.wireOp",EDGE,"E1573"),sQuery(id+"F16.wireOp",EDGE,"E1574"),sQuery(id+"F16.wireOp",EDGE,"E1575"),sQuery(id+"F16.wireOp",EDGE,"E1576"),sQuery(id+"F16.wireOp",EDGE,"E1577"),sQuery(id+"F16.wireOp",EDGE,"E1578"),sQuery(id+"F16.wireOp",EDGE,"E1579"),sQuery(id+"F16.wireOp",EDGE,"E1580"),sQuery(id+"F16.wireOp",EDGE,"E1581"),sQuery(id+"F16.wireOp",EDGE,"E1582"),sQuery(id+"F16.wireOp",EDGE,"E1583"),sQuery(id+"F16.wireOp",EDGE,"E1584"),sQuery(id+"F16.wireOp",EDGE,"E1585"),sQuery(id+"F16.wireOp",EDGE,"E1586"),sQuery(id+"F16.wireOp",EDGE,"E1587"),sQuery(id+"F16.wireOp",EDGE,"E1588"),sQuery(id+"F16.wireOp",EDGE,"E1589"),sQuery(id+"F16.wireOp",EDGE,"E1590"),sQuery(id+"F16.wireOp",EDGE,"E1591"),sQuery(id+"F16.wireOp",EDGE,"E1592"),sQuery(id+"F16.wireOp",EDGE,"E1593"),sQuery(id+"F16.wireOp",EDGE,"E1594"),sQuery(id+"F16.wireOp",EDGE,"E1595"),sQuery(id+"F16.wireOp",EDGE,"E1596"),sQuery(id+"F16.wireOp",EDGE,"E1597"),sQuery(id+"F16.wireOp",EDGE,"E1598"),sQuery(id+"F16.wireOp",EDGE,"E1599"),sQuery(id+"F16.wireOp",EDGE,"E1600"),sQuery(id+"F16.wireOp",EDGE,"E1601"),sQuery(id+"F16.wireOp",EDGE,"E1602"),sQuery(id+"F16.wireOp",EDGE,"E1603"),sQuery(id+"F16.wireOp",EDGE,"E1604"),sQuery(id+"F16.wireOp",EDGE,"E1605"),sQuery(id+"F16.wireOp",EDGE,"E1606"),sQuery(id+"F16.wireOp",EDGE,"E1607"),sQuery(id+"F16.wireOp",EDGE,"E1608"),sQuery(id+"F16.wireOp",EDGE,"E1609"),sQuery(id+"F16.wireOp",EDGE,"E1610"),sQuery(id+"F16.wireOp",EDGE,"E1611"),sQuery(id+"F16.wireOp",EDGE,"E1612"),sQuery(id+"F16.wireOp",EDGE,"E1613"),sQuery(id+"F16.wireOp",EDGE,"E1614"),sQuery(id+"F16.wireOp",EDGE,"E1615"),sQuery(id+"F16.wireOp",EDGE,"E1616")])]});
            var Q5;
            Q5=makeQuery(id+"F17.opExtrude","CAP_VERTEX",VERTEX,{"disambiguationData":[OSD([sQuery(id+"F16.wireOp",EDGE,"E1046.0"),sQuery(id+"F16.wireOp",EDGE,"E1047.0")])],"isStart":false});
            transform(context, id + "F18", {"entities" : qUnion([Q0, Q1, Q2, Q3, Q4]), "transformType" : TransformType.SCALE_UNIFORMLY, "scale" : 0.2, "scalePoint" : qUnion([Q5]), "makeCopy" : false});
        }
        {
            var Q0;
            Q0=makeQuery(id+"F17.opExtrude","SWEPT_BODY",BODY,{"disambiguationData":[OSD([sQuery(id+"F16.wireOp",EDGE,"E1023.0"),sQuery(id+"F16.wireOp",EDGE,"E1024.0"),sQuery(id+"F16.wireOp",EDGE,"E1025.0"),sQuery(id+"F16.wireOp",EDGE,"E1026.0"),sQuery(id+"F16.wireOp",EDGE,"E1027.0"),sQuery(id+"F16.wireOp",EDGE,"E1028.0"),sQuery(id+"F16.wireOp",EDGE,"E1029.0"),sQuery(id+"F16.wireOp",EDGE,"E1030.0"),sQuery(id+"F16.wireOp",EDGE,"E1031.0"),sQuery(id+"F16.wireOp",EDGE,"E1032.0"),sQuery(id+"F16.wireOp",EDGE,"E1033.0"),sQuery(id+"F16.wireOp",EDGE,"E1034.0"),sQuery(id+"F16.wireOp",EDGE,"E1035.0"),sQuery(id+"F16.wireOp",EDGE,"E1036.0"),sQuery(id+"F16.wireOp",EDGE,"E1037.0"),sQuery(id+"F16.wireOp",EDGE,"E1038.0"),sQuery(id+"F16.wireOp",EDGE,"E1039.0"),sQuery(id+"F16.wireOp",EDGE,"E1040.0"),sQuery(id+"F16.wireOp",EDGE,"E1041.0"),sQuery(id+"F16.wireOp",EDGE,"E1042.0"),sQuery(id+"F16.wireOp",EDGE,"E1043.0"),sQuery(id+"F16.wireOp",EDGE,"E1044.0"),sQuery(id+"F16.wireOp",EDGE,"E1045.0"),sQuery(id+"F16.wireOp",EDGE,"E1046.0"),sQuery(id+"F16.wireOp",EDGE,"E1047.0"),sQuery(id+"F16.wireOp",EDGE,"E1048.0"),sQuery(id+"F16.wireOp",EDGE,"E1049.0"),sQuery(id+"F16.wireOp",EDGE,"E1050.0"),sQuery(id+"F16.wireOp",EDGE,"E1051.0"),sQuery(id+"F16.wireOp",EDGE,"E1052.0")])]});
            var Q1;
            Q1=makeQuery(id+"F17.opExtrude","SWEPT_BODY",BODY,{"disambiguationData":[OSD([sQuery(id+"F16.wireOp",EDGE,"E1053"),sQuery(id+"F16.wireOp",EDGE,"E1054"),sQuery(id+"F16.wireOp",EDGE,"E1055"),sQuery(id+"F16.wireOp",EDGE,"E1056"),sQuery(id+"F16.wireOp",EDGE,"E1057"),sQuery(id+"F16.wireOp",EDGE,"E1058"),sQuery(id+"F16.wireOp",EDGE,"E1059"),sQuery(id+"F16.wireOp",EDGE,"E1060"),sQuery(id+"F16.wireOp",EDGE,"E1061"),sQuery(id+"F16.wireOp",EDGE,"E1062"),sQuery(id+"F16.wireOp",EDGE,"E1063"),sQuery(id+"F16.wireOp",EDGE,"E1064"),sQuery(id+"F16.wireOp",EDGE,"E1065"),sQuery(id+"F16.wireOp",EDGE,"E1066"),sQuery(id+"F16.wireOp",EDGE,"E1067"),sQuery(id+"F16.wireOp",EDGE,"E1068"),sQuery(id+"F16.wireOp",EDGE,"E1069"),sQuery(id+"F16.wireOp",EDGE,"E1070"),sQuery(id+"F16.wireOp",EDGE,"E1071"),sQuery(id+"F16.wireOp",EDGE,"E1072"),sQuery(id+"F16.wireOp",EDGE,"E1073"),sQuery(id+"F16.wireOp",EDGE,"E1074"),sQuery(id+"F16.wireOp",EDGE,"E1075"),sQuery(id+"F16.wireOp",EDGE,"E1076"),sQuery(id+"F16.wireOp",EDGE,"E1077"),sQuery(id+"F16.wireOp",EDGE,"E1078")])]});
            var Q2;
            Q2=makeQuery(id+"F17.opExtrude","SWEPT_BODY",BODY,{"disambiguationData":[OSD([sQuery(id+"F16.wireOp",EDGE,"E1079"),sQuery(id+"F16.wireOp",EDGE,"E1080"),sQuery(id+"F16.wireOp",EDGE,"E1081"),sQuery(id+"F16.wireOp",EDGE,"E1082"),sQuery(id+"F16.wireOp",EDGE,"E1083"),sQuery(id+"F16.wireOp",EDGE,"E1084"),sQuery(id+"F16.wireOp",EDGE,"E1085"),sQuery(id+"F16.wireOp",EDGE,"E1086"),sQuery(id+"F16.wireOp",EDGE,"E1087"),sQuery(id+"F16.wireOp",EDGE,"E1088"),sQuery(id+"F16.wireOp",EDGE,"E1089"),sQuery(id+"F16.wireOp",EDGE,"E1090"),sQuery(id+"F16.wireOp",EDGE,"E1091"),sQuery(id+"F16.wireOp",EDGE,"E1092"),sQuery(id+"F16.wireOp",EDGE,"E1093"),sQuery(id+"F16.wireOp",EDGE,"E1094"),sQuery(id+"F16.wireOp",EDGE,"E1095"),sQuery(id+"F16.wireOp",EDGE,"E1096"),sQuery(id+"F16.wireOp",EDGE,"E1097"),sQuery(id+"F16.wireOp",EDGE,"E1098"),sQuery(id+"F16.wireOp",EDGE,"E1099"),sQuery(id+"F16.wireOp",EDGE,"E1100"),sQuery(id+"F16.wireOp",EDGE,"E1101"),sQuery(id+"F16.wireOp",EDGE,"E1102"),sQuery(id+"F16.wireOp",EDGE,"E1103"),sQuery(id+"F16.wireOp",EDGE,"E1104"),sQuery(id+"F16.wireOp",EDGE,"E1105"),sQuery(id+"F16.wireOp",EDGE,"E1106"),sQuery(id+"F16.wireOp",EDGE,"E1107"),sQuery(id+"F16.wireOp",EDGE,"E1108"),sQuery(id+"F16.wireOp",EDGE,"E1109"),sQuery(id+"F16.wireOp",EDGE,"E1110"),sQuery(id+"F16.wireOp",EDGE,"E1111"),sQuery(id+"F16.wireOp",EDGE,"E1112"),sQuery(id+"F16.wireOp",EDGE,"E1113"),sQuery(id+"F16.wireOp",EDGE,"E1114"),sQuery(id+"F16.wireOp",EDGE,"E1115"),sQuery(id+"F16.wireOp",EDGE,"E1116"),sQuery(id+"F16.wireOp",EDGE,"E1117"),sQuery(id+"F16.wireOp",EDGE,"E1118"),sQuery(id+"F16.wireOp",EDGE,"E1119"),sQuery(id+"F16.wireOp",EDGE,"E1120"),sQuery(id+"F16.wireOp",EDGE,"E1121"),sQuery(id+"F16.wireOp",EDGE,"E1122"),sQuery(id+"F16.wireOp",EDGE,"E1123"),sQuery(id+"F16.wireOp",EDGE,"E1124"),sQuery(id+"F16.wireOp",EDGE,"E1125"),sQuery(id+"F16.wireOp",EDGE,"E1126"),sQuery(id+"F16.wireOp",EDGE,"E1127"),sQuery(id+"F16.wireOp",EDGE,"E1128"),sQuery(id+"F16.wireOp",EDGE,"E1129"),sQuery(id+"F16.wireOp",EDGE,"E1130"),sQuery(id+"F16.wireOp",EDGE,"E1131"),sQuery(id+"F16.wireOp",EDGE,"E1132"),sQuery(id+"F16.wireOp",EDGE,"E1133"),sQuery(id+"F16.wireOp",EDGE,"E1134"),sQuery(id+"F16.wireOp",EDGE,"E1135"),sQuery(id+"F16.wireOp",EDGE,"E1136"),sQuery(id+"F16.wireOp",EDGE,"E1137"),sQuery(id+"F16.wireOp",EDGE,"E1138"),sQuery(id+"F16.wireOp",EDGE,"E1139"),sQuery(id+"F16.wireOp",EDGE,"E1140"),sQuery(id+"F16.wireOp",EDGE,"E1141"),sQuery(id+"F16.wireOp",EDGE,"E1142"),sQuery(id+"F16.wireOp",EDGE,"E1143"),sQuery(id+"F16.wireOp",EDGE,"E1144"),sQuery(id+"F16.wireOp",EDGE,"E1145"),sQuery(id+"F16.wireOp",EDGE,"E1146"),sQuery(id+"F16.wireOp",EDGE,"E1147"),sQuery(id+"F16.wireOp",EDGE,"E1148"),sQuery(id+"F16.wireOp",EDGE,"E1149"),sQuery(id+"F16.wireOp",EDGE,"E1150"),sQuery(id+"F16.wireOp",EDGE,"E1151"),sQuery(id+"F16.wireOp",EDGE,"E1152"),sQuery(id+"F16.wireOp",EDGE,"E1153"),sQuery(id+"F16.wireOp",EDGE,"E1154"),sQuery(id+"F16.wireOp",EDGE,"E1155"),sQuery(id+"F16.wireOp",EDGE,"E1156"),sQuery(id+"F16.wireOp",EDGE,"E1157"),sQuery(id+"F16.wireOp",EDGE,"E1158"),sQuery(id+"F16.wireOp",EDGE,"E1159"),sQuery(id+"F16.wireOp",EDGE,"E1160"),sQuery(id+"F16.wireOp",EDGE,"E1161"),sQuery(id+"F16.wireOp",EDGE,"E1162"),sQuery(id+"F16.wireOp",EDGE,"E1163"),sQuery(id+"F16.wireOp",EDGE,"E1164"),sQuery(id+"F16.wireOp",EDGE,"E1165"),sQuery(id+"F16.wireOp",EDGE,"E1166"),sQuery(id+"F16.wireOp",EDGE,"E1167"),sQuery(id+"F16.wireOp",EDGE,"E1168"),sQuery(id+"F16.wireOp",EDGE,"E1169"),sQuery(id+"F16.wireOp",EDGE,"E1170"),sQuery(id+"F16.wireOp",EDGE,"E1171"),sQuery(id+"F16.wireOp",EDGE,"E1172"),sQuery(id+"F16.wireOp",EDGE,"E1173"),sQuery(id+"F16.wireOp",EDGE,"E1174"),sQuery(id+"F16.wireOp",EDGE,"E1175"),sQuery(id+"F16.wireOp",EDGE,"E1176"),sQuery(id+"F16.wireOp",EDGE,"E1177"),sQuery(id+"F16.wireOp",EDGE,"E1178"),sQuery(id+"F16.wireOp",EDGE,"E1179"),sQuery(id+"F16.wireOp",EDGE,"E1180"),sQuery(id+"F16.wireOp",EDGE,"E1181"),sQuery(id+"F16.wireOp",EDGE,"E1182"),sQuery(id+"F16.wireOp",EDGE,"E1183"),sQuery(id+"F16.wireOp",EDGE,"E1184"),sQuery(id+"F16.wireOp",EDGE,"E1185"),sQuery(id+"F16.wireOp",EDGE,"E1186"),sQuery(id+"F16.wireOp",EDGE,"E1187"),sQuery(id+"F16.wireOp",EDGE,"E1188"),sQuery(id+"F16.wireOp",EDGE,"E1189"),sQuery(id+"F16.wireOp",EDGE,"E1190"),sQuery(id+"F16.wireOp",EDGE,"E1191"),sQuery(id+"F16.wireOp",EDGE,"E1192"),sQuery(id+"F16.wireOp",EDGE,"E1193"),sQuery(id+"F16.wireOp",EDGE,"E1194"),sQuery(id+"F16.wireOp",EDGE,"E1195"),sQuery(id+"F16.wireOp",EDGE,"E1196"),sQuery(id+"F16.wireOp",EDGE,"E1197"),sQuery(id+"F16.wireOp",EDGE,"E1198"),sQuery(id+"F16.wireOp",EDGE,"E1199"),sQuery(id+"F16.wireOp",EDGE,"E1200"),sQuery(id+"F16.wireOp",EDGE,"E1201"),sQuery(id+"F16.wireOp",EDGE,"E1202"),sQuery(id+"F16.wireOp",EDGE,"E1203"),sQuery(id+"F16.wireOp",EDGE,"E1204"),sQuery(id+"F16.wireOp",EDGE,"E1205"),sQuery(id+"F16.wireOp",EDGE,"E1206"),sQuery(id+"F16.wireOp",EDGE,"E1207"),sQuery(id+"F16.wireOp",EDGE,"E1208"),sQuery(id+"F16.wireOp",EDGE,"E1209"),sQuery(id+"F16.wireOp",EDGE,"E1210"),sQuery(id+"F16.wireOp",EDGE,"E1211"),sQuery(id+"F16.wireOp",EDGE,"E1212"),sQuery(id+"F16.wireOp",EDGE,"E1213"),sQuery(id+"F16.wireOp",EDGE,"E1214"),sQuery(id+"F16.wireOp",EDGE,"E1215"),sQuery(id+"F16.wireOp",EDGE,"E1216"),sQuery(id+"F16.wireOp",EDGE,"E1217"),sQuery(id+"F16.wireOp",EDGE,"E1218"),sQuery(id+"F16.wireOp",EDGE,"E1219"),sQuery(id+"F16.wireOp",EDGE,"E1220"),sQuery(id+"F16.wireOp",EDGE,"E1221"),sQuery(id+"F16.wireOp",EDGE,"E1222"),sQuery(id+"F16.wireOp",EDGE,"E1223"),sQuery(id+"F16.wireOp",EDGE,"E1224"),sQuery(id+"F16.wireOp",EDGE,"E1225"),sQuery(id+"F16.wireOp",EDGE,"E1226"),sQuery(id+"F16.wireOp",EDGE,"E1227"),sQuery(id+"F16.wireOp",EDGE,"E1228"),sQuery(id+"F16.wireOp",EDGE,"E1229"),sQuery(id+"F16.wireOp",EDGE,"E1230"),sQuery(id+"F16.wireOp",EDGE,"E1231"),sQuery(id+"F16.wireOp",EDGE,"E1232"),sQuery(id+"F16.wireOp",EDGE,"E1233"),sQuery(id+"F16.wireOp",EDGE,"E1234"),sQuery(id+"F16.wireOp",EDGE,"E1235"),sQuery(id+"F16.wireOp",EDGE,"E1236"),sQuery(id+"F16.wireOp",EDGE,"E1237"),sQuery(id+"F16.wireOp",EDGE,"E1238"),sQuery(id+"F16.wireOp",EDGE,"E1239"),sQuery(id+"F16.wireOp",EDGE,"E1240"),sQuery(id+"F16.wireOp",EDGE,"E1241"),sQuery(id+"F16.wireOp",EDGE,"E1242"),sQuery(id+"F16.wireOp",EDGE,"E1243"),sQuery(id+"F16.wireOp",EDGE,"E1244"),sQuery(id+"F16.wireOp",EDGE,"E1245"),sQuery(id+"F16.wireOp",EDGE,"E1246"),sQuery(id+"F16.wireOp",EDGE,"E1247"),sQuery(id+"F16.wireOp",EDGE,"E1248"),sQuery(id+"F16.wireOp",EDGE,"E1249"),sQuery(id+"F16.wireOp",EDGE,"E1250"),sQuery(id+"F16.wireOp",EDGE,"E1251"),sQuery(id+"F16.wireOp",EDGE,"E1252"),sQuery(id+"F16.wireOp",EDGE,"E1253"),sQuery(id+"F16.wireOp",EDGE,"E1254"),sQuery(id+"F16.wireOp",EDGE,"E1255"),sQuery(id+"F16.wireOp",EDGE,"E1256"),sQuery(id+"F16.wireOp",EDGE,"E1257"),sQuery(id+"F16.wireOp",EDGE,"E1258"),sQuery(id+"F16.wireOp",EDGE,"E1259"),sQuery(id+"F16.wireOp",EDGE,"E1260"),sQuery(id+"F16.wireOp",EDGE,"E1261"),sQuery(id+"F16.wireOp",EDGE,"E1262"),sQuery(id+"F16.wireOp",EDGE,"E1263"),sQuery(id+"F16.wireOp",EDGE,"E1264"),sQuery(id+"F16.wireOp",EDGE,"E1265"),sQuery(id+"F16.wireOp",EDGE,"E1266"),sQuery(id+"F16.wireOp",EDGE,"E1267"),sQuery(id+"F16.wireOp",EDGE,"E1268"),sQuery(id+"F16.wireOp",EDGE,"E1269"),sQuery(id+"F16.wireOp",EDGE,"E1270"),sQuery(id+"F16.wireOp",EDGE,"E1271"),sQuery(id+"F16.wireOp",EDGE,"E1272"),sQuery(id+"F16.wireOp",EDGE,"E1273"),sQuery(id+"F16.wireOp",EDGE,"E1274"),sQuery(id+"F16.wireOp",EDGE,"E1275"),sQuery(id+"F16.wireOp",EDGE,"E1276"),sQuery(id+"F16.wireOp",EDGE,"E1277"),sQuery(id+"F16.wireOp",EDGE,"E1278"),sQuery(id+"F16.wireOp",EDGE,"E1279"),sQuery(id+"F16.wireOp",EDGE,"E1280"),sQuery(id+"F16.wireOp",EDGE,"E1281"),sQuery(id+"F16.wireOp",EDGE,"E1282"),sQuery(id+"F16.wireOp",EDGE,"E1283")])]});
            var Q3;
            Q3=makeQuery(id+"F17.opExtrude","SWEPT_BODY",BODY,{"disambiguationData":[OSD([sQuery(id+"F16.wireOp",EDGE,"E1284"),sQuery(id+"F16.wireOp",EDGE,"E1285"),sQuery(id+"F16.wireOp",EDGE,"E1286"),sQuery(id+"F16.wireOp",EDGE,"E1287"),sQuery(id+"F16.wireOp",EDGE,"E1288"),sQuery(id+"F16.wireOp",EDGE,"E1289"),sQuery(id+"F16.wireOp",EDGE,"E1290"),sQuery(id+"F16.wireOp",EDGE,"E1291"),sQuery(id+"F16.wireOp",EDGE,"E1292"),sQuery(id+"F16.wireOp",EDGE,"E1293"),sQuery(id+"F16.wireOp",EDGE,"E1294"),sQuery(id+"F16.wireOp",EDGE,"E1295"),sQuery(id+"F16.wireOp",EDGE,"E1296"),sQuery(id+"F16.wireOp",EDGE,"E1297"),sQuery(id+"F16.wireOp",EDGE,"E1298"),sQuery(id+"F16.wireOp",EDGE,"E1299"),sQuery(id+"F16.wireOp",EDGE,"E1300"),sQuery(id+"F16.wireOp",EDGE,"E1301"),sQuery(id+"F16.wireOp",EDGE,"E1302"),sQuery(id+"F16.wireOp",EDGE,"E1303"),sQuery(id+"F16.wireOp",EDGE,"E1304"),sQuery(id+"F16.wireOp",EDGE,"E1305"),sQuery(id+"F16.wireOp",EDGE,"E1306"),sQuery(id+"F16.wireOp",EDGE,"E1307"),sQuery(id+"F16.wireOp",EDGE,"E1308"),sQuery(id+"F16.wireOp",EDGE,"E1309"),sQuery(id+"F16.wireOp",EDGE,"E1310"),sQuery(id+"F16.wireOp",EDGE,"E1311"),sQuery(id+"F16.wireOp",EDGE,"E1312"),sQuery(id+"F16.wireOp",EDGE,"E1313"),sQuery(id+"F16.wireOp",EDGE,"E1314"),sQuery(id+"F16.wireOp",EDGE,"E1315"),sQuery(id+"F16.wireOp",EDGE,"E1316"),sQuery(id+"F16.wireOp",EDGE,"E1317"),sQuery(id+"F16.wireOp",EDGE,"E1318"),sQuery(id+"F16.wireOp",EDGE,"E1319"),sQuery(id+"F16.wireOp",EDGE,"E1320"),sQuery(id+"F16.wireOp",EDGE,"E1321"),sQuery(id+"F16.wireOp",EDGE,"E1322"),sQuery(id+"F16.wireOp",EDGE,"E1323"),sQuery(id+"F16.wireOp",EDGE,"E1324"),sQuery(id+"F16.wireOp",EDGE,"E1325"),sQuery(id+"F16.wireOp",EDGE,"E1326"),sQuery(id+"F16.wireOp",EDGE,"E1327"),sQuery(id+"F16.wireOp",EDGE,"E1328"),sQuery(id+"F16.wireOp",EDGE,"E1329"),sQuery(id+"F16.wireOp",EDGE,"E1330"),sQuery(id+"F16.wireOp",EDGE,"E1331"),sQuery(id+"F16.wireOp",EDGE,"E1332"),sQuery(id+"F16.wireOp",EDGE,"E1333"),sQuery(id+"F16.wireOp",EDGE,"E1334"),sQuery(id+"F16.wireOp",EDGE,"E1335"),sQuery(id+"F16.wireOp",EDGE,"E1336"),sQuery(id+"F16.wireOp",EDGE,"E1337"),sQuery(id+"F16.wireOp",EDGE,"E1338"),sQuery(id+"F16.wireOp",EDGE,"E1339"),sQuery(id+"F16.wireOp",EDGE,"E1340"),sQuery(id+"F16.wireOp",EDGE,"E1341"),sQuery(id+"F16.wireOp",EDGE,"E1342"),sQuery(id+"F16.wireOp",EDGE,"E1343"),sQuery(id+"F16.wireOp",EDGE,"E1344"),sQuery(id+"F16.wireOp",EDGE,"E1345"),sQuery(id+"F16.wireOp",EDGE,"E1346"),sQuery(id+"F16.wireOp",EDGE,"E1347"),sQuery(id+"F16.wireOp",EDGE,"E1348"),sQuery(id+"F16.wireOp",EDGE,"E1349"),sQuery(id+"F16.wireOp",EDGE,"E1350"),sQuery(id+"F16.wireOp",EDGE,"E1351"),sQuery(id+"F16.wireOp",EDGE,"E1352"),sQuery(id+"F16.wireOp",EDGE,"E1353"),sQuery(id+"F16.wireOp",EDGE,"E1354"),sQuery(id+"F16.wireOp",EDGE,"E1355"),sQuery(id+"F16.wireOp",EDGE,"E1356"),sQuery(id+"F16.wireOp",EDGE,"E1357"),sQuery(id+"F16.wireOp",EDGE,"E1358"),sQuery(id+"F16.wireOp",EDGE,"E1359"),sQuery(id+"F16.wireOp",EDGE,"E1360"),sQuery(id+"F16.wireOp",EDGE,"E1361"),sQuery(id+"F16.wireOp",EDGE,"E1362"),sQuery(id+"F16.wireOp",EDGE,"E1363"),sQuery(id+"F16.wireOp",EDGE,"E1364"),sQuery(id+"F16.wireOp",EDGE,"E1365"),sQuery(id+"F16.wireOp",EDGE,"E1366"),sQuery(id+"F16.wireOp",EDGE,"E1367"),sQuery(id+"F16.wireOp",EDGE,"E1368"),sQuery(id+"F16.wireOp",EDGE,"E1369"),sQuery(id+"F16.wireOp",EDGE,"E1370"),sQuery(id+"F16.wireOp",EDGE,"E1371"),sQuery(id+"F16.wireOp",EDGE,"E1372"),sQuery(id+"F16.wireOp",EDGE,"E1373"),sQuery(id+"F16.wireOp",EDGE,"E1374"),sQuery(id+"F16.wireOp",EDGE,"E1375"),sQuery(id+"F16.wireOp",EDGE,"E1376"),sQuery(id+"F16.wireOp",EDGE,"E1377"),sQuery(id+"F16.wireOp",EDGE,"E1378"),sQuery(id+"F16.wireOp",EDGE,"E1379"),sQuery(id+"F16.wireOp",EDGE,"E1380"),sQuery(id+"F16.wireOp",EDGE,"E1381"),sQuery(id+"F16.wireOp",EDGE,"E1382"),sQuery(id+"F16.wireOp",EDGE,"E1383"),sQuery(id+"F16.wireOp",EDGE,"E1384"),sQuery(id+"F16.wireOp",EDGE,"E1385"),sQuery(id+"F16.wireOp",EDGE,"E1386"),sQuery(id+"F16.wireOp",EDGE,"E1387"),sQuery(id+"F16.wireOp",EDGE,"E1388"),sQuery(id+"F16.wireOp",EDGE,"E1389"),sQuery(id+"F16.wireOp",EDGE,"E1390"),sQuery(id+"F16.wireOp",EDGE,"E1391"),sQuery(id+"F16.wireOp",EDGE,"E1392"),sQuery(id+"F16.wireOp",EDGE,"E1393"),sQuery(id+"F16.wireOp",EDGE,"E1394"),sQuery(id+"F16.wireOp",EDGE,"E1395"),sQuery(id+"F16.wireOp",EDGE,"E1396"),sQuery(id+"F16.wireOp",EDGE,"E1397"),sQuery(id+"F16.wireOp",EDGE,"E1398"),sQuery(id+"F16.wireOp",EDGE,"E1399"),sQuery(id+"F16.wireOp",EDGE,"E1400"),sQuery(id+"F16.wireOp",EDGE,"E1401"),sQuery(id+"F16.wireOp",EDGE,"E1402"),sQuery(id+"F16.wireOp",EDGE,"E1403"),sQuery(id+"F16.wireOp",EDGE,"E1404"),sQuery(id+"F16.wireOp",EDGE,"E1405"),sQuery(id+"F16.wireOp",EDGE,"E1406"),sQuery(id+"F16.wireOp",EDGE,"E1407"),sQuery(id+"F16.wireOp",EDGE,"E1408"),sQuery(id+"F16.wireOp",EDGE,"E1409"),sQuery(id+"F16.wireOp",EDGE,"E1410"),sQuery(id+"F16.wireOp",EDGE,"E1411"),sQuery(id+"F16.wireOp",EDGE,"E1412"),sQuery(id+"F16.wireOp",EDGE,"E1413"),sQuery(id+"F16.wireOp",EDGE,"E1414"),sQuery(id+"F16.wireOp",EDGE,"E1415"),sQuery(id+"F16.wireOp",EDGE,"E1416"),sQuery(id+"F16.wireOp",EDGE,"E1417"),sQuery(id+"F16.wireOp",EDGE,"E1418"),sQuery(id+"F16.wireOp",EDGE,"E1419"),sQuery(id+"F16.wireOp",EDGE,"E1420"),sQuery(id+"F16.wireOp",EDGE,"E1421"),sQuery(id+"F16.wireOp",EDGE,"E1422"),sQuery(id+"F16.wireOp",EDGE,"E1423"),sQuery(id+"F16.wireOp",EDGE,"E1424"),sQuery(id+"F16.wireOp",EDGE,"E1425"),sQuery(id+"F16.wireOp",EDGE,"E1426"),sQuery(id+"F16.wireOp",EDGE,"E1427"),sQuery(id+"F16.wireOp",EDGE,"E1428"),sQuery(id+"F16.wireOp",EDGE,"E1429"),sQuery(id+"F16.wireOp",EDGE,"E1430"),sQuery(id+"F16.wireOp",EDGE,"E1431"),sQuery(id+"F16.wireOp",EDGE,"E1432"),sQuery(id+"F16.wireOp",EDGE,"E1433"),sQuery(id+"F16.wireOp",EDGE,"E1434"),sQuery(id+"F16.wireOp",EDGE,"E1435"),sQuery(id+"F16.wireOp",EDGE,"E1436"),sQuery(id+"F16.wireOp",EDGE,"E1437"),sQuery(id+"F16.wireOp",EDGE,"E1438"),sQuery(id+"F16.wireOp",EDGE,"E1439"),sQuery(id+"F16.wireOp",EDGE,"E1440"),sQuery(id+"F16.wireOp",EDGE,"E1441"),sQuery(id+"F16.wireOp",EDGE,"E1442"),sQuery(id+"F16.wireOp",EDGE,"E1443"),sQuery(id+"F16.wireOp",EDGE,"E1444"),sQuery(id+"F16.wireOp",EDGE,"E1445"),sQuery(id+"F16.wireOp",EDGE,"E1446")])]});
            var Q4;
            Q4=makeQuery(id+"F17.opExtrude","SWEPT_BODY",BODY,{"disambiguationData":[OSD([sQuery(id+"F16.wireOp",EDGE,"E1447"),sQuery(id+"F16.wireOp",EDGE,"E1448"),sQuery(id+"F16.wireOp",EDGE,"E1449"),sQuery(id+"F16.wireOp",EDGE,"E1450"),sQuery(id+"F16.wireOp",EDGE,"E1451"),sQuery(id+"F16.wireOp",EDGE,"E1452"),sQuery(id+"F16.wireOp",EDGE,"E1453"),sQuery(id+"F16.wireOp",EDGE,"E1454"),sQuery(id+"F16.wireOp",EDGE,"E1455"),sQuery(id+"F16.wireOp",EDGE,"E1456"),sQuery(id+"F16.wireOp",EDGE,"E1457"),sQuery(id+"F16.wireOp",EDGE,"E1458"),sQuery(id+"F16.wireOp",EDGE,"E1459"),sQuery(id+"F16.wireOp",EDGE,"E1460"),sQuery(id+"F16.wireOp",EDGE,"E1461"),sQuery(id+"F16.wireOp",EDGE,"E1462"),sQuery(id+"F16.wireOp",EDGE,"E1463"),sQuery(id+"F16.wireOp",EDGE,"E1464"),sQuery(id+"F16.wireOp",EDGE,"E1465"),sQuery(id+"F16.wireOp",EDGE,"E1466"),sQuery(id+"F16.wireOp",EDGE,"E1467"),sQuery(id+"F16.wireOp",EDGE,"E1468"),sQuery(id+"F16.wireOp",EDGE,"E1469"),sQuery(id+"F16.wireOp",EDGE,"E1470"),sQuery(id+"F16.wireOp",EDGE,"E1471"),sQuery(id+"F16.wireOp",EDGE,"E1472"),sQuery(id+"F16.wireOp",EDGE,"E1473"),sQuery(id+"F16.wireOp",EDGE,"E1474"),sQuery(id+"F16.wireOp",EDGE,"E1475"),sQuery(id+"F16.wireOp",EDGE,"E1476"),sQuery(id+"F16.wireOp",EDGE,"E1477"),sQuery(id+"F16.wireOp",EDGE,"E1478"),sQuery(id+"F16.wireOp",EDGE,"E1479"),sQuery(id+"F16.wireOp",EDGE,"E1480"),sQuery(id+"F16.wireOp",EDGE,"E1481"),sQuery(id+"F16.wireOp",EDGE,"E1482"),sQuery(id+"F16.wireOp",EDGE,"E1483"),sQuery(id+"F16.wireOp",EDGE,"E1484"),sQuery(id+"F16.wireOp",EDGE,"E1485"),sQuery(id+"F16.wireOp",EDGE,"E1486"),sQuery(id+"F16.wireOp",EDGE,"E1487"),sQuery(id+"F16.wireOp",EDGE,"E1488"),sQuery(id+"F16.wireOp",EDGE,"E1489"),sQuery(id+"F16.wireOp",EDGE,"E1490"),sQuery(id+"F16.wireOp",EDGE,"E1491"),sQuery(id+"F16.wireOp",EDGE,"E1492"),sQuery(id+"F16.wireOp",EDGE,"E1493"),sQuery(id+"F16.wireOp",EDGE,"E1494"),sQuery(id+"F16.wireOp",EDGE,"E1495"),sQuery(id+"F16.wireOp",EDGE,"E1496"),sQuery(id+"F16.wireOp",EDGE,"E1497"),sQuery(id+"F16.wireOp",EDGE,"E1498"),sQuery(id+"F16.wireOp",EDGE,"E1499"),sQuery(id+"F16.wireOp",EDGE,"E1500"),sQuery(id+"F16.wireOp",EDGE,"E1501"),sQuery(id+"F16.wireOp",EDGE,"E1502"),sQuery(id+"F16.wireOp",EDGE,"E1503"),sQuery(id+"F16.wireOp",EDGE,"E1504"),sQuery(id+"F16.wireOp",EDGE,"E1505"),sQuery(id+"F16.wireOp",EDGE,"E1506"),sQuery(id+"F16.wireOp",EDGE,"E1507"),sQuery(id+"F16.wireOp",EDGE,"E1508"),sQuery(id+"F16.wireOp",EDGE,"E1509"),sQuery(id+"F16.wireOp",EDGE,"E1510"),sQuery(id+"F16.wireOp",EDGE,"E1511"),sQuery(id+"F16.wireOp",EDGE,"E1512"),sQuery(id+"F16.wireOp",EDGE,"E1513"),sQuery(id+"F16.wireOp",EDGE,"E1514"),sQuery(id+"F16.wireOp",EDGE,"E1515"),sQuery(id+"F16.wireOp",EDGE,"E1516"),sQuery(id+"F16.wireOp",EDGE,"E1517"),sQuery(id+"F16.wireOp",EDGE,"E1518"),sQuery(id+"F16.wireOp",EDGE,"E1519"),sQuery(id+"F16.wireOp",EDGE,"E1520"),sQuery(id+"F16.wireOp",EDGE,"E1521"),sQuery(id+"F16.wireOp",EDGE,"E1522"),sQuery(id+"F16.wireOp",EDGE,"E1523"),sQuery(id+"F16.wireOp",EDGE,"E1524"),sQuery(id+"F16.wireOp",EDGE,"E1525"),sQuery(id+"F16.wireOp",EDGE,"E1526"),sQuery(id+"F16.wireOp",EDGE,"E1527"),sQuery(id+"F16.wireOp",EDGE,"E1528"),sQuery(id+"F16.wireOp",EDGE,"E1529"),sQuery(id+"F16.wireOp",EDGE,"E1530"),sQuery(id+"F16.wireOp",EDGE,"E1531"),sQuery(id+"F16.wireOp",EDGE,"E1532"),sQuery(id+"F16.wireOp",EDGE,"E1533"),sQuery(id+"F16.wireOp",EDGE,"E1534"),sQuery(id+"F16.wireOp",EDGE,"E1535"),sQuery(id+"F16.wireOp",EDGE,"E1536"),sQuery(id+"F16.wireOp",EDGE,"E1537"),sQuery(id+"F16.wireOp",EDGE,"E1538"),sQuery(id+"F16.wireOp",EDGE,"E1539"),sQuery(id+"F16.wireOp",EDGE,"E1540"),sQuery(id+"F16.wireOp",EDGE,"E1541"),sQuery(id+"F16.wireOp",EDGE,"E1542"),sQuery(id+"F16.wireOp",EDGE,"E1543"),sQuery(id+"F16.wireOp",EDGE,"E1544"),sQuery(id+"F16.wireOp",EDGE,"E1545"),sQuery(id+"F16.wireOp",EDGE,"E1546"),sQuery(id+"F16.wireOp",EDGE,"E1547"),sQuery(id+"F16.wireOp",EDGE,"E1548"),sQuery(id+"F16.wireOp",EDGE,"E1549"),sQuery(id+"F16.wireOp",EDGE,"E1550"),sQuery(id+"F16.wireOp",EDGE,"E1551"),sQuery(id+"F16.wireOp",EDGE,"E1552"),sQuery(id+"F16.wireOp",EDGE,"E1553"),sQuery(id+"F16.wireOp",EDGE,"E1554"),sQuery(id+"F16.wireOp",EDGE,"E1555"),sQuery(id+"F16.wireOp",EDGE,"E1556"),sQuery(id+"F16.wireOp",EDGE,"E1557"),sQuery(id+"F16.wireOp",EDGE,"E1558"),sQuery(id+"F16.wireOp",EDGE,"E1559"),sQuery(id+"F16.wireOp",EDGE,"E1560"),sQuery(id+"F16.wireOp",EDGE,"E1561"),sQuery(id+"F16.wireOp",EDGE,"E1562"),sQuery(id+"F16.wireOp",EDGE,"E1563"),sQuery(id+"F16.wireOp",EDGE,"E1564"),sQuery(id+"F16.wireOp",EDGE,"E1565"),sQuery(id+"F16.wireOp",EDGE,"E1566"),sQuery(id+"F16.wireOp",EDGE,"E1567"),sQuery(id+"F16.wireOp",EDGE,"E1568"),sQuery(id+"F16.wireOp",EDGE,"E1569"),sQuery(id+"F16.wireOp",EDGE,"E1570"),sQuery(id+"F16.wireOp",EDGE,"E1571"),sQuery(id+"F16.wireOp",EDGE,"E1572"),sQuery(id+"F16.wireOp",EDGE,"E1573"),sQuery(id+"F16.wireOp",EDGE,"E1574"),sQuery(id+"F16.wireOp",EDGE,"E1575"),sQuery(id+"F16.wireOp",EDGE,"E1576"),sQuery(id+"F16.wireOp",EDGE,"E1577"),sQuery(id+"F16.wireOp",EDGE,"E1578"),sQuery(id+"F16.wireOp",EDGE,"E1579"),sQuery(id+"F16.wireOp",EDGE,"E1580"),sQuery(id+"F16.wireOp",EDGE,"E1581"),sQuery(id+"F16.wireOp",EDGE,"E1582"),sQuery(id+"F16.wireOp",EDGE,"E1583"),sQuery(id+"F16.wireOp",EDGE,"E1584"),sQuery(id+"F16.wireOp",EDGE,"E1585"),sQuery(id+"F16.wireOp",EDGE,"E1586"),sQuery(id+"F16.wireOp",EDGE,"E1587"),sQuery(id+"F16.wireOp",EDGE,"E1588"),sQuery(id+"F16.wireOp",EDGE,"E1589"),sQuery(id+"F16.wireOp",EDGE,"E1590"),sQuery(id+"F16.wireOp",EDGE,"E1591"),sQuery(id+"F16.wireOp",EDGE,"E1592"),sQuery(id+"F16.wireOp",EDGE,"E1593"),sQuery(id+"F16.wireOp",EDGE,"E1594"),sQuery(id+"F16.wireOp",EDGE,"E1595"),sQuery(id+"F16.wireOp",EDGE,"E1596"),sQuery(id+"F16.wireOp",EDGE,"E1597"),sQuery(id+"F16.wireOp",EDGE,"E1598"),sQuery(id+"F16.wireOp",EDGE,"E1599"),sQuery(id+"F16.wireOp",EDGE,"E1600"),sQuery(id+"F16.wireOp",EDGE,"E1601"),sQuery(id+"F16.wireOp",EDGE,"E1602"),sQuery(id+"F16.wireOp",EDGE,"E1603"),sQuery(id+"F16.wireOp",EDGE,"E1604"),sQuery(id+"F16.wireOp",EDGE,"E1605"),sQuery(id+"F16.wireOp",EDGE,"E1606"),sQuery(id+"F16.wireOp",EDGE,"E1607"),sQuery(id+"F16.wireOp",EDGE,"E1608"),sQuery(id+"F16.wireOp",EDGE,"E1609"),sQuery(id+"F16.wireOp",EDGE,"E1610"),sQuery(id+"F16.wireOp",EDGE,"E1611"),sQuery(id+"F16.wireOp",EDGE,"E1612"),sQuery(id+"F16.wireOp",EDGE,"E1613"),sQuery(id+"F16.wireOp",EDGE,"E1614"),sQuery(id+"F16.wireOp",EDGE,"E1615"),sQuery(id+"F16.wireOp",EDGE,"E1616")])]});
            transform(context, id + "F19", {"entities" : qUnion([Q0, Q1, Q2, Q3, Q4]), "transformType" : TransformType.TRANSLATION_3D, "dx" : -1.95 * mm, "dy" : 110 * mm, "dz" : -28.7 * mm, "makeCopy" : false});
        }
        {
            var Q0;
            Q0=makeQuery(id+"F17.opExtrude","SWEPT_BODY",BODY,{"disambiguationData":[OSD([sQuery(id+"F16.wireOp",EDGE,"E1023.0"),sQuery(id+"F16.wireOp",EDGE,"E1024.0"),sQuery(id+"F16.wireOp",EDGE,"E1025.0"),sQuery(id+"F16.wireOp",EDGE,"E1026.0"),sQuery(id+"F16.wireOp",EDGE,"E1027.0"),sQuery(id+"F16.wireOp",EDGE,"E1028.0"),sQuery(id+"F16.wireOp",EDGE,"E1029.0"),sQuery(id+"F16.wireOp",EDGE,"E1030.0"),sQuery(id+"F16.wireOp",EDGE,"E1031.0"),sQuery(id+"F16.wireOp",EDGE,"E1032.0"),sQuery(id+"F16.wireOp",EDGE,"E1033.0"),sQuery(id+"F16.wireOp",EDGE,"E1034.0"),sQuery(id+"F16.wireOp",EDGE,"E1035.0"),sQuery(id+"F16.wireOp",EDGE,"E1036.0"),sQuery(id+"F16.wireOp",EDGE,"E1037.0"),sQuery(id+"F16.wireOp",EDGE,"E1038.0"),sQuery(id+"F16.wireOp",EDGE,"E1039.0"),sQuery(id+"F16.wireOp",EDGE,"E1040.0"),sQuery(id+"F16.wireOp",EDGE,"E1041.0"),sQuery(id+"F16.wireOp",EDGE,"E1042.0"),sQuery(id+"F16.wireOp",EDGE,"E1043.0"),sQuery(id+"F16.wireOp",EDGE,"E1044.0"),sQuery(id+"F16.wireOp",EDGE,"E1045.0"),sQuery(id+"F16.wireOp",EDGE,"E1046.0"),sQuery(id+"F16.wireOp",EDGE,"E1047.0"),sQuery(id+"F16.wireOp",EDGE,"E1048.0"),sQuery(id+"F16.wireOp",EDGE,"E1049.0"),sQuery(id+"F16.wireOp",EDGE,"E1050.0"),sQuery(id+"F16.wireOp",EDGE,"E1051.0"),sQuery(id+"F16.wireOp",EDGE,"E1052.0")])]});
            var Q1;
            Q1=makeQuery(id+"F17.opExtrude","SWEPT_BODY",BODY,{"disambiguationData":[OSD([sQuery(id+"F16.wireOp",EDGE,"E1079"),sQuery(id+"F16.wireOp",EDGE,"E1080"),sQuery(id+"F16.wireOp",EDGE,"E1081"),sQuery(id+"F16.wireOp",EDGE,"E1082"),sQuery(id+"F16.wireOp",EDGE,"E1083"),sQuery(id+"F16.wireOp",EDGE,"E1084"),sQuery(id+"F16.wireOp",EDGE,"E1085"),sQuery(id+"F16.wireOp",EDGE,"E1086"),sQuery(id+"F16.wireOp",EDGE,"E1087"),sQuery(id+"F16.wireOp",EDGE,"E1088"),sQuery(id+"F16.wireOp",EDGE,"E1089"),sQuery(id+"F16.wireOp",EDGE,"E1090"),sQuery(id+"F16.wireOp",EDGE,"E1091"),sQuery(id+"F16.wireOp",EDGE,"E1092"),sQuery(id+"F16.wireOp",EDGE,"E1093"),sQuery(id+"F16.wireOp",EDGE,"E1094"),sQuery(id+"F16.wireOp",EDGE,"E1095"),sQuery(id+"F16.wireOp",EDGE,"E1096"),sQuery(id+"F16.wireOp",EDGE,"E1097"),sQuery(id+"F16.wireOp",EDGE,"E1098"),sQuery(id+"F16.wireOp",EDGE,"E1099"),sQuery(id+"F16.wireOp",EDGE,"E1100"),sQuery(id+"F16.wireOp",EDGE,"E1101"),sQuery(id+"F16.wireOp",EDGE,"E1102"),sQuery(id+"F16.wireOp",EDGE,"E1103"),sQuery(id+"F16.wireOp",EDGE,"E1104"),sQuery(id+"F16.wireOp",EDGE,"E1105"),sQuery(id+"F16.wireOp",EDGE,"E1106"),sQuery(id+"F16.wireOp",EDGE,"E1107"),sQuery(id+"F16.wireOp",EDGE,"E1108"),sQuery(id+"F16.wireOp",EDGE,"E1109"),sQuery(id+"F16.wireOp",EDGE,"E1110"),sQuery(id+"F16.wireOp",EDGE,"E1111"),sQuery(id+"F16.wireOp",EDGE,"E1112"),sQuery(id+"F16.wireOp",EDGE,"E1113"),sQuery(id+"F16.wireOp",EDGE,"E1114"),sQuery(id+"F16.wireOp",EDGE,"E1115"),sQuery(id+"F16.wireOp",EDGE,"E1116"),sQuery(id+"F16.wireOp",EDGE,"E1117"),sQuery(id+"F16.wireOp",EDGE,"E1118"),sQuery(id+"F16.wireOp",EDGE,"E1119"),sQuery(id+"F16.wireOp",EDGE,"E1120"),sQuery(id+"F16.wireOp",EDGE,"E1121"),sQuery(id+"F16.wireOp",EDGE,"E1122"),sQuery(id+"F16.wireOp",EDGE,"E1123"),sQuery(id+"F16.wireOp",EDGE,"E1124"),sQuery(id+"F16.wireOp",EDGE,"E1125"),sQuery(id+"F16.wireOp",EDGE,"E1126"),sQuery(id+"F16.wireOp",EDGE,"E1127"),sQuery(id+"F16.wireOp",EDGE,"E1128"),sQuery(id+"F16.wireOp",EDGE,"E1129"),sQuery(id+"F16.wireOp",EDGE,"E1130"),sQuery(id+"F16.wireOp",EDGE,"E1131"),sQuery(id+"F16.wireOp",EDGE,"E1132"),sQuery(id+"F16.wireOp",EDGE,"E1133"),sQuery(id+"F16.wireOp",EDGE,"E1134"),sQuery(id+"F16.wireOp",EDGE,"E1135"),sQuery(id+"F16.wireOp",EDGE,"E1136"),sQuery(id+"F16.wireOp",EDGE,"E1137"),sQuery(id+"F16.wireOp",EDGE,"E1138"),sQuery(id+"F16.wireOp",EDGE,"E1139"),sQuery(id+"F16.wireOp",EDGE,"E1140"),sQuery(id+"F16.wireOp",EDGE,"E1141"),sQuery(id+"F16.wireOp",EDGE,"E1142"),sQuery(id+"F16.wireOp",EDGE,"E1143"),sQuery(id+"F16.wireOp",EDGE,"E1144"),sQuery(id+"F16.wireOp",EDGE,"E1145"),sQuery(id+"F16.wireOp",EDGE,"E1146"),sQuery(id+"F16.wireOp",EDGE,"E1147"),sQuery(id+"F16.wireOp",EDGE,"E1148"),sQuery(id+"F16.wireOp",EDGE,"E1149"),sQuery(id+"F16.wireOp",EDGE,"E1150"),sQuery(id+"F16.wireOp",EDGE,"E1151"),sQuery(id+"F16.wireOp",EDGE,"E1152"),sQuery(id+"F16.wireOp",EDGE,"E1153"),sQuery(id+"F16.wireOp",EDGE,"E1154"),sQuery(id+"F16.wireOp",EDGE,"E1155"),sQuery(id+"F16.wireOp",EDGE,"E1156"),sQuery(id+"F16.wireOp",EDGE,"E1157"),sQuery(id+"F16.wireOp",EDGE,"E1158"),sQuery(id+"F16.wireOp",EDGE,"E1159"),sQuery(id+"F16.wireOp",EDGE,"E1160"),sQuery(id+"F16.wireOp",EDGE,"E1161"),sQuery(id+"F16.wireOp",EDGE,"E1162"),sQuery(id+"F16.wireOp",EDGE,"E1163"),sQuery(id+"F16.wireOp",EDGE,"E1164"),sQuery(id+"F16.wireOp",EDGE,"E1165"),sQuery(id+"F16.wireOp",EDGE,"E1166"),sQuery(id+"F16.wireOp",EDGE,"E1167"),sQuery(id+"F16.wireOp",EDGE,"E1168"),sQuery(id+"F16.wireOp",EDGE,"E1169"),sQuery(id+"F16.wireOp",EDGE,"E1170"),sQuery(id+"F16.wireOp",EDGE,"E1171"),sQuery(id+"F16.wireOp",EDGE,"E1172"),sQuery(id+"F16.wireOp",EDGE,"E1173"),sQuery(id+"F16.wireOp",EDGE,"E1174"),sQuery(id+"F16.wireOp",EDGE,"E1175"),sQuery(id+"F16.wireOp",EDGE,"E1176"),sQuery(id+"F16.wireOp",EDGE,"E1177"),sQuery(id+"F16.wireOp",EDGE,"E1178"),sQuery(id+"F16.wireOp",EDGE,"E1179"),sQuery(id+"F16.wireOp",EDGE,"E1180"),sQuery(id+"F16.wireOp",EDGE,"E1181"),sQuery(id+"F16.wireOp",EDGE,"E1182"),sQuery(id+"F16.wireOp",EDGE,"E1183"),sQuery(id+"F16.wireOp",EDGE,"E1184"),sQuery(id+"F16.wireOp",EDGE,"E1185"),sQuery(id+"F16.wireOp",EDGE,"E1186"),sQuery(id+"F16.wireOp",EDGE,"E1187"),sQuery(id+"F16.wireOp",EDGE,"E1188"),sQuery(id+"F16.wireOp",EDGE,"E1189"),sQuery(id+"F16.wireOp",EDGE,"E1190"),sQuery(id+"F16.wireOp",EDGE,"E1191"),sQuery(id+"F16.wireOp",EDGE,"E1192"),sQuery(id+"F16.wireOp",EDGE,"E1193"),sQuery(id+"F16.wireOp",EDGE,"E1194"),sQuery(id+"F16.wireOp",EDGE,"E1195"),sQuery(id+"F16.wireOp",EDGE,"E1196"),sQuery(id+"F16.wireOp",EDGE,"E1197"),sQuery(id+"F16.wireOp",EDGE,"E1198"),sQuery(id+"F16.wireOp",EDGE,"E1199"),sQuery(id+"F16.wireOp",EDGE,"E1200"),sQuery(id+"F16.wireOp",EDGE,"E1201"),sQuery(id+"F16.wireOp",EDGE,"E1202"),sQuery(id+"F16.wireOp",EDGE,"E1203"),sQuery(id+"F16.wireOp",EDGE,"E1204"),sQuery(id+"F16.wireOp",EDGE,"E1205"),sQuery(id+"F16.wireOp",EDGE,"E1206"),sQuery(id+"F16.wireOp",EDGE,"E1207"),sQuery(id+"F16.wireOp",EDGE,"E1208"),sQuery(id+"F16.wireOp",EDGE,"E1209"),sQuery(id+"F16.wireOp",EDGE,"E1210"),sQuery(id+"F16.wireOp",EDGE,"E1211"),sQuery(id+"F16.wireOp",EDGE,"E1212"),sQuery(id+"F16.wireOp",EDGE,"E1213"),sQuery(id+"F16.wireOp",EDGE,"E1214"),sQuery(id+"F16.wireOp",EDGE,"E1215"),sQuery(id+"F16.wireOp",EDGE,"E1216"),sQuery(id+"F16.wireOp",EDGE,"E1217"),sQuery(id+"F16.wireOp",EDGE,"E1218"),sQuery(id+"F16.wireOp",EDGE,"E1219"),sQuery(id+"F16.wireOp",EDGE,"E1220"),sQuery(id+"F16.wireOp",EDGE,"E1221"),sQuery(id+"F16.wireOp",EDGE,"E1222"),sQuery(id+"F16.wireOp",EDGE,"E1223"),sQuery(id+"F16.wireOp",EDGE,"E1224"),sQuery(id+"F16.wireOp",EDGE,"E1225"),sQuery(id+"F16.wireOp",EDGE,"E1226"),sQuery(id+"F16.wireOp",EDGE,"E1227"),sQuery(id+"F16.wireOp",EDGE,"E1228"),sQuery(id+"F16.wireOp",EDGE,"E1229"),sQuery(id+"F16.wireOp",EDGE,"E1230"),sQuery(id+"F16.wireOp",EDGE,"E1231"),sQuery(id+"F16.wireOp",EDGE,"E1232"),sQuery(id+"F16.wireOp",EDGE,"E1233"),sQuery(id+"F16.wireOp",EDGE,"E1234"),sQuery(id+"F16.wireOp",EDGE,"E1235"),sQuery(id+"F16.wireOp",EDGE,"E1236"),sQuery(id+"F16.wireOp",EDGE,"E1237"),sQuery(id+"F16.wireOp",EDGE,"E1238"),sQuery(id+"F16.wireOp",EDGE,"E1239"),sQuery(id+"F16.wireOp",EDGE,"E1240"),sQuery(id+"F16.wireOp",EDGE,"E1241"),sQuery(id+"F16.wireOp",EDGE,"E1242"),sQuery(id+"F16.wireOp",EDGE,"E1243"),sQuery(id+"F16.wireOp",EDGE,"E1244"),sQuery(id+"F16.wireOp",EDGE,"E1245"),sQuery(id+"F16.wireOp",EDGE,"E1246"),sQuery(id+"F16.wireOp",EDGE,"E1247"),sQuery(id+"F16.wireOp",EDGE,"E1248"),sQuery(id+"F16.wireOp",EDGE,"E1249"),sQuery(id+"F16.wireOp",EDGE,"E1250"),sQuery(id+"F16.wireOp",EDGE,"E1251"),sQuery(id+"F16.wireOp",EDGE,"E1252"),sQuery(id+"F16.wireOp",EDGE,"E1253"),sQuery(id+"F16.wireOp",EDGE,"E1254"),sQuery(id+"F16.wireOp",EDGE,"E1255"),sQuery(id+"F16.wireOp",EDGE,"E1256"),sQuery(id+"F16.wireOp",EDGE,"E1257"),sQuery(id+"F16.wireOp",EDGE,"E1258"),sQuery(id+"F16.wireOp",EDGE,"E1259"),sQuery(id+"F16.wireOp",EDGE,"E1260"),sQuery(id+"F16.wireOp",EDGE,"E1261"),sQuery(id+"F16.wireOp",EDGE,"E1262"),sQuery(id+"F16.wireOp",EDGE,"E1263"),sQuery(id+"F16.wireOp",EDGE,"E1264"),sQuery(id+"F16.wireOp",EDGE,"E1265"),sQuery(id+"F16.wireOp",EDGE,"E1266"),sQuery(id+"F16.wireOp",EDGE,"E1267"),sQuery(id+"F16.wireOp",EDGE,"E1268"),sQuery(id+"F16.wireOp",EDGE,"E1269"),sQuery(id+"F16.wireOp",EDGE,"E1270"),sQuery(id+"F16.wireOp",EDGE,"E1271"),sQuery(id+"F16.wireOp",EDGE,"E1272"),sQuery(id+"F16.wireOp",EDGE,"E1273"),sQuery(id+"F16.wireOp",EDGE,"E1274"),sQuery(id+"F16.wireOp",EDGE,"E1275"),sQuery(id+"F16.wireOp",EDGE,"E1276"),sQuery(id+"F16.wireOp",EDGE,"E1277"),sQuery(id+"F16.wireOp",EDGE,"E1278"),sQuery(id+"F16.wireOp",EDGE,"E1279"),sQuery(id+"F16.wireOp",EDGE,"E1280"),sQuery(id+"F16.wireOp",EDGE,"E1281"),sQuery(id+"F16.wireOp",EDGE,"E1282"),sQuery(id+"F16.wireOp",EDGE,"E1283")])]});
            var Q2;
            Q2=makeQuery(id+"F17.opExtrude","SWEPT_BODY",BODY,{"disambiguationData":[OSD([sQuery(id+"F16.wireOp",EDGE,"E1284"),sQuery(id+"F16.wireOp",EDGE,"E1285"),sQuery(id+"F16.wireOp",EDGE,"E1286"),sQuery(id+"F16.wireOp",EDGE,"E1287"),sQuery(id+"F16.wireOp",EDGE,"E1288"),sQuery(id+"F16.wireOp",EDGE,"E1289"),sQuery(id+"F16.wireOp",EDGE,"E1290"),sQuery(id+"F16.wireOp",EDGE,"E1291"),sQuery(id+"F16.wireOp",EDGE,"E1292"),sQuery(id+"F16.wireOp",EDGE,"E1293"),sQuery(id+"F16.wireOp",EDGE,"E1294"),sQuery(id+"F16.wireOp",EDGE,"E1295"),sQuery(id+"F16.wireOp",EDGE,"E1296"),sQuery(id+"F16.wireOp",EDGE,"E1297"),sQuery(id+"F16.wireOp",EDGE,"E1298"),sQuery(id+"F16.wireOp",EDGE,"E1299"),sQuery(id+"F16.wireOp",EDGE,"E1300"),sQuery(id+"F16.wireOp",EDGE,"E1301"),sQuery(id+"F16.wireOp",EDGE,"E1302"),sQuery(id+"F16.wireOp",EDGE,"E1303"),sQuery(id+"F16.wireOp",EDGE,"E1304"),sQuery(id+"F16.wireOp",EDGE,"E1305"),sQuery(id+"F16.wireOp",EDGE,"E1306"),sQuery(id+"F16.wireOp",EDGE,"E1307"),sQuery(id+"F16.wireOp",EDGE,"E1308"),sQuery(id+"F16.wireOp",EDGE,"E1309"),sQuery(id+"F16.wireOp",EDGE,"E1310"),sQuery(id+"F16.wireOp",EDGE,"E1311"),sQuery(id+"F16.wireOp",EDGE,"E1312"),sQuery(id+"F16.wireOp",EDGE,"E1313"),sQuery(id+"F16.wireOp",EDGE,"E1314"),sQuery(id+"F16.wireOp",EDGE,"E1315"),sQuery(id+"F16.wireOp",EDGE,"E1316"),sQuery(id+"F16.wireOp",EDGE,"E1317"),sQuery(id+"F16.wireOp",EDGE,"E1318"),sQuery(id+"F16.wireOp",EDGE,"E1319"),sQuery(id+"F16.wireOp",EDGE,"E1320"),sQuery(id+"F16.wireOp",EDGE,"E1321"),sQuery(id+"F16.wireOp",EDGE,"E1322"),sQuery(id+"F16.wireOp",EDGE,"E1323"),sQuery(id+"F16.wireOp",EDGE,"E1324"),sQuery(id+"F16.wireOp",EDGE,"E1325"),sQuery(id+"F16.wireOp",EDGE,"E1326"),sQuery(id+"F16.wireOp",EDGE,"E1327"),sQuery(id+"F16.wireOp",EDGE,"E1328"),sQuery(id+"F16.wireOp",EDGE,"E1329"),sQuery(id+"F16.wireOp",EDGE,"E1330"),sQuery(id+"F16.wireOp",EDGE,"E1331"),sQuery(id+"F16.wireOp",EDGE,"E1332"),sQuery(id+"F16.wireOp",EDGE,"E1333"),sQuery(id+"F16.wireOp",EDGE,"E1334"),sQuery(id+"F16.wireOp",EDGE,"E1335"),sQuery(id+"F16.wireOp",EDGE,"E1336"),sQuery(id+"F16.wireOp",EDGE,"E1337"),sQuery(id+"F16.wireOp",EDGE,"E1338"),sQuery(id+"F16.wireOp",EDGE,"E1339"),sQuery(id+"F16.wireOp",EDGE,"E1340"),sQuery(id+"F16.wireOp",EDGE,"E1341"),sQuery(id+"F16.wireOp",EDGE,"E1342"),sQuery(id+"F16.wireOp",EDGE,"E1343"),sQuery(id+"F16.wireOp",EDGE,"E1344"),sQuery(id+"F16.wireOp",EDGE,"E1345"),sQuery(id+"F16.wireOp",EDGE,"E1346"),sQuery(id+"F16.wireOp",EDGE,"E1347"),sQuery(id+"F16.wireOp",EDGE,"E1348"),sQuery(id+"F16.wireOp",EDGE,"E1349"),sQuery(id+"F16.wireOp",EDGE,"E1350"),sQuery(id+"F16.wireOp",EDGE,"E1351"),sQuery(id+"F16.wireOp",EDGE,"E1352"),sQuery(id+"F16.wireOp",EDGE,"E1353"),sQuery(id+"F16.wireOp",EDGE,"E1354"),sQuery(id+"F16.wireOp",EDGE,"E1355"),sQuery(id+"F16.wireOp",EDGE,"E1356"),sQuery(id+"F16.wireOp",EDGE,"E1357"),sQuery(id+"F16.wireOp",EDGE,"E1358"),sQuery(id+"F16.wireOp",EDGE,"E1359"),sQuery(id+"F16.wireOp",EDGE,"E1360"),sQuery(id+"F16.wireOp",EDGE,"E1361"),sQuery(id+"F16.wireOp",EDGE,"E1362"),sQuery(id+"F16.wireOp",EDGE,"E1363"),sQuery(id+"F16.wireOp",EDGE,"E1364"),sQuery(id+"F16.wireOp",EDGE,"E1365"),sQuery(id+"F16.wireOp",EDGE,"E1366"),sQuery(id+"F16.wireOp",EDGE,"E1367"),sQuery(id+"F16.wireOp",EDGE,"E1368"),sQuery(id+"F16.wireOp",EDGE,"E1369"),sQuery(id+"F16.wireOp",EDGE,"E1370"),sQuery(id+"F16.wireOp",EDGE,"E1371"),sQuery(id+"F16.wireOp",EDGE,"E1372"),sQuery(id+"F16.wireOp",EDGE,"E1373"),sQuery(id+"F16.wireOp",EDGE,"E1374"),sQuery(id+"F16.wireOp",EDGE,"E1375"),sQuery(id+"F16.wireOp",EDGE,"E1376"),sQuery(id+"F16.wireOp",EDGE,"E1377"),sQuery(id+"F16.wireOp",EDGE,"E1378"),sQuery(id+"F16.wireOp",EDGE,"E1379"),sQuery(id+"F16.wireOp",EDGE,"E1380"),sQuery(id+"F16.wireOp",EDGE,"E1381"),sQuery(id+"F16.wireOp",EDGE,"E1382"),sQuery(id+"F16.wireOp",EDGE,"E1383"),sQuery(id+"F16.wireOp",EDGE,"E1384"),sQuery(id+"F16.wireOp",EDGE,"E1385"),sQuery(id+"F16.wireOp",EDGE,"E1386"),sQuery(id+"F16.wireOp",EDGE,"E1387"),sQuery(id+"F16.wireOp",EDGE,"E1388"),sQuery(id+"F16.wireOp",EDGE,"E1389"),sQuery(id+"F16.wireOp",EDGE,"E1390"),sQuery(id+"F16.wireOp",EDGE,"E1391"),sQuery(id+"F16.wireOp",EDGE,"E1392"),sQuery(id+"F16.wireOp",EDGE,"E1393"),sQuery(id+"F16.wireOp",EDGE,"E1394"),sQuery(id+"F16.wireOp",EDGE,"E1395"),sQuery(id+"F16.wireOp",EDGE,"E1396"),sQuery(id+"F16.wireOp",EDGE,"E1397"),sQuery(id+"F16.wireOp",EDGE,"E1398"),sQuery(id+"F16.wireOp",EDGE,"E1399"),sQuery(id+"F16.wireOp",EDGE,"E1400"),sQuery(id+"F16.wireOp",EDGE,"E1401"),sQuery(id+"F16.wireOp",EDGE,"E1402"),sQuery(id+"F16.wireOp",EDGE,"E1403"),sQuery(id+"F16.wireOp",EDGE,"E1404"),sQuery(id+"F16.wireOp",EDGE,"E1405"),sQuery(id+"F16.wireOp",EDGE,"E1406"),sQuery(id+"F16.wireOp",EDGE,"E1407"),sQuery(id+"F16.wireOp",EDGE,"E1408"),sQuery(id+"F16.wireOp",EDGE,"E1409"),sQuery(id+"F16.wireOp",EDGE,"E1410"),sQuery(id+"F16.wireOp",EDGE,"E1411"),sQuery(id+"F16.wireOp",EDGE,"E1412"),sQuery(id+"F16.wireOp",EDGE,"E1413"),sQuery(id+"F16.wireOp",EDGE,"E1414"),sQuery(id+"F16.wireOp",EDGE,"E1415"),sQuery(id+"F16.wireOp",EDGE,"E1416"),sQuery(id+"F16.wireOp",EDGE,"E1417"),sQuery(id+"F16.wireOp",EDGE,"E1418"),sQuery(id+"F16.wireOp",EDGE,"E1419"),sQuery(id+"F16.wireOp",EDGE,"E1420"),sQuery(id+"F16.wireOp",EDGE,"E1421"),sQuery(id+"F16.wireOp",EDGE,"E1422"),sQuery(id+"F16.wireOp",EDGE,"E1423"),sQuery(id+"F16.wireOp",EDGE,"E1424"),sQuery(id+"F16.wireOp",EDGE,"E1425"),sQuery(id+"F16.wireOp",EDGE,"E1426"),sQuery(id+"F16.wireOp",EDGE,"E1427"),sQuery(id+"F16.wireOp",EDGE,"E1428"),sQuery(id+"F16.wireOp",EDGE,"E1429"),sQuery(id+"F16.wireOp",EDGE,"E1430"),sQuery(id+"F16.wireOp",EDGE,"E1431"),sQuery(id+"F16.wireOp",EDGE,"E1432"),sQuery(id+"F16.wireOp",EDGE,"E1433"),sQuery(id+"F16.wireOp",EDGE,"E1434"),sQuery(id+"F16.wireOp",EDGE,"E1435"),sQuery(id+"F16.wireOp",EDGE,"E1436"),sQuery(id+"F16.wireOp",EDGE,"E1437"),sQuery(id+"F16.wireOp",EDGE,"E1438"),sQuery(id+"F16.wireOp",EDGE,"E1439"),sQuery(id+"F16.wireOp",EDGE,"E1440"),sQuery(id+"F16.wireOp",EDGE,"E1441"),sQuery(id+"F16.wireOp",EDGE,"E1442"),sQuery(id+"F16.wireOp",EDGE,"E1443"),sQuery(id+"F16.wireOp",EDGE,"E1444"),sQuery(id+"F16.wireOp",EDGE,"E1445"),sQuery(id+"F16.wireOp",EDGE,"E1446")])]});
            var Q3;
            Q3=makeQuery(id+"F17.opExtrude","SWEPT_BODY",BODY,{"disambiguationData":[OSD([sQuery(id+"F16.wireOp",EDGE,"E1447"),sQuery(id+"F16.wireOp",EDGE,"E1448"),sQuery(id+"F16.wireOp",EDGE,"E1449"),sQuery(id+"F16.wireOp",EDGE,"E1450"),sQuery(id+"F16.wireOp",EDGE,"E1451"),sQuery(id+"F16.wireOp",EDGE,"E1452"),sQuery(id+"F16.wireOp",EDGE,"E1453"),sQuery(id+"F16.wireOp",EDGE,"E1454"),sQuery(id+"F16.wireOp",EDGE,"E1455"),sQuery(id+"F16.wireOp",EDGE,"E1456"),sQuery(id+"F16.wireOp",EDGE,"E1457"),sQuery(id+"F16.wireOp",EDGE,"E1458"),sQuery(id+"F16.wireOp",EDGE,"E1459"),sQuery(id+"F16.wireOp",EDGE,"E1460"),sQuery(id+"F16.wireOp",EDGE,"E1461"),sQuery(id+"F16.wireOp",EDGE,"E1462"),sQuery(id+"F16.wireOp",EDGE,"E1463"),sQuery(id+"F16.wireOp",EDGE,"E1464"),sQuery(id+"F16.wireOp",EDGE,"E1465"),sQuery(id+"F16.wireOp",EDGE,"E1466"),sQuery(id+"F16.wireOp",EDGE,"E1467"),sQuery(id+"F16.wireOp",EDGE,"E1468"),sQuery(id+"F16.wireOp",EDGE,"E1469"),sQuery(id+"F16.wireOp",EDGE,"E1470"),sQuery(id+"F16.wireOp",EDGE,"E1471"),sQuery(id+"F16.wireOp",EDGE,"E1472"),sQuery(id+"F16.wireOp",EDGE,"E1473"),sQuery(id+"F16.wireOp",EDGE,"E1474"),sQuery(id+"F16.wireOp",EDGE,"E1475"),sQuery(id+"F16.wireOp",EDGE,"E1476"),sQuery(id+"F16.wireOp",EDGE,"E1477"),sQuery(id+"F16.wireOp",EDGE,"E1478"),sQuery(id+"F16.wireOp",EDGE,"E1479"),sQuery(id+"F16.wireOp",EDGE,"E1480"),sQuery(id+"F16.wireOp",EDGE,"E1481"),sQuery(id+"F16.wireOp",EDGE,"E1482"),sQuery(id+"F16.wireOp",EDGE,"E1483"),sQuery(id+"F16.wireOp",EDGE,"E1484"),sQuery(id+"F16.wireOp",EDGE,"E1485"),sQuery(id+"F16.wireOp",EDGE,"E1486"),sQuery(id+"F16.wireOp",EDGE,"E1487"),sQuery(id+"F16.wireOp",EDGE,"E1488"),sQuery(id+"F16.wireOp",EDGE,"E1489"),sQuery(id+"F16.wireOp",EDGE,"E1490"),sQuery(id+"F16.wireOp",EDGE,"E1491"),sQuery(id+"F16.wireOp",EDGE,"E1492"),sQuery(id+"F16.wireOp",EDGE,"E1493"),sQuery(id+"F16.wireOp",EDGE,"E1494"),sQuery(id+"F16.wireOp",EDGE,"E1495"),sQuery(id+"F16.wireOp",EDGE,"E1496"),sQuery(id+"F16.wireOp",EDGE,"E1497"),sQuery(id+"F16.wireOp",EDGE,"E1498"),sQuery(id+"F16.wireOp",EDGE,"E1499"),sQuery(id+"F16.wireOp",EDGE,"E1500"),sQuery(id+"F16.wireOp",EDGE,"E1501"),sQuery(id+"F16.wireOp",EDGE,"E1502"),sQuery(id+"F16.wireOp",EDGE,"E1503"),sQuery(id+"F16.wireOp",EDGE,"E1504"),sQuery(id+"F16.wireOp",EDGE,"E1505"),sQuery(id+"F16.wireOp",EDGE,"E1506"),sQuery(id+"F16.wireOp",EDGE,"E1507"),sQuery(id+"F16.wireOp",EDGE,"E1508"),sQuery(id+"F16.wireOp",EDGE,"E1509"),sQuery(id+"F16.wireOp",EDGE,"E1510"),sQuery(id+"F16.wireOp",EDGE,"E1511"),sQuery(id+"F16.wireOp",EDGE,"E1512"),sQuery(id+"F16.wireOp",EDGE,"E1513"),sQuery(id+"F16.wireOp",EDGE,"E1514"),sQuery(id+"F16.wireOp",EDGE,"E1515"),sQuery(id+"F16.wireOp",EDGE,"E1516"),sQuery(id+"F16.wireOp",EDGE,"E1517"),sQuery(id+"F16.wireOp",EDGE,"E1518"),sQuery(id+"F16.wireOp",EDGE,"E1519"),sQuery(id+"F16.wireOp",EDGE,"E1520"),sQuery(id+"F16.wireOp",EDGE,"E1521"),sQuery(id+"F16.wireOp",EDGE,"E1522"),sQuery(id+"F16.wireOp",EDGE,"E1523"),sQuery(id+"F16.wireOp",EDGE,"E1524"),sQuery(id+"F16.wireOp",EDGE,"E1525"),sQuery(id+"F16.wireOp",EDGE,"E1526"),sQuery(id+"F16.wireOp",EDGE,"E1527"),sQuery(id+"F16.wireOp",EDGE,"E1528"),sQuery(id+"F16.wireOp",EDGE,"E1529"),sQuery(id+"F16.wireOp",EDGE,"E1530"),sQuery(id+"F16.wireOp",EDGE,"E1531"),sQuery(id+"F16.wireOp",EDGE,"E1532"),sQuery(id+"F16.wireOp",EDGE,"E1533"),sQuery(id+"F16.wireOp",EDGE,"E1534"),sQuery(id+"F16.wireOp",EDGE,"E1535"),sQuery(id+"F16.wireOp",EDGE,"E1536"),sQuery(id+"F16.wireOp",EDGE,"E1537"),sQuery(id+"F16.wireOp",EDGE,"E1538"),sQuery(id+"F16.wireOp",EDGE,"E1539"),sQuery(id+"F16.wireOp",EDGE,"E1540"),sQuery(id+"F16.wireOp",EDGE,"E1541"),sQuery(id+"F16.wireOp",EDGE,"E1542"),sQuery(id+"F16.wireOp",EDGE,"E1543"),sQuery(id+"F16.wireOp",EDGE,"E1544"),sQuery(id+"F16.wireOp",EDGE,"E1545"),sQuery(id+"F16.wireOp",EDGE,"E1546"),sQuery(id+"F16.wireOp",EDGE,"E1547"),sQuery(id+"F16.wireOp",EDGE,"E1548"),sQuery(id+"F16.wireOp",EDGE,"E1549"),sQuery(id+"F16.wireOp",EDGE,"E1550"),sQuery(id+"F16.wireOp",EDGE,"E1551"),sQuery(id+"F16.wireOp",EDGE,"E1552"),sQuery(id+"F16.wireOp",EDGE,"E1553"),sQuery(id+"F16.wireOp",EDGE,"E1554"),sQuery(id+"F16.wireOp",EDGE,"E1555"),sQuery(id+"F16.wireOp",EDGE,"E1556"),sQuery(id+"F16.wireOp",EDGE,"E1557"),sQuery(id+"F16.wireOp",EDGE,"E1558"),sQuery(id+"F16.wireOp",EDGE,"E1559"),sQuery(id+"F16.wireOp",EDGE,"E1560"),sQuery(id+"F16.wireOp",EDGE,"E1561"),sQuery(id+"F16.wireOp",EDGE,"E1562"),sQuery(id+"F16.wireOp",EDGE,"E1563"),sQuery(id+"F16.wireOp",EDGE,"E1564"),sQuery(id+"F16.wireOp",EDGE,"E1565"),sQuery(id+"F16.wireOp",EDGE,"E1566"),sQuery(id+"F16.wireOp",EDGE,"E1567"),sQuery(id+"F16.wireOp",EDGE,"E1568"),sQuery(id+"F16.wireOp",EDGE,"E1569"),sQuery(id+"F16.wireOp",EDGE,"E1570"),sQuery(id+"F16.wireOp",EDGE,"E1571"),sQuery(id+"F16.wireOp",EDGE,"E1572"),sQuery(id+"F16.wireOp",EDGE,"E1573"),sQuery(id+"F16.wireOp",EDGE,"E1574"),sQuery(id+"F16.wireOp",EDGE,"E1575"),sQuery(id+"F16.wireOp",EDGE,"E1576"),sQuery(id+"F16.wireOp",EDGE,"E1577"),sQuery(id+"F16.wireOp",EDGE,"E1578"),sQuery(id+"F16.wireOp",EDGE,"E1579"),sQuery(id+"F16.wireOp",EDGE,"E1580"),sQuery(id+"F16.wireOp",EDGE,"E1581"),sQuery(id+"F16.wireOp",EDGE,"E1582"),sQuery(id+"F16.wireOp",EDGE,"E1583"),sQuery(id+"F16.wireOp",EDGE,"E1584"),sQuery(id+"F16.wireOp",EDGE,"E1585"),sQuery(id+"F16.wireOp",EDGE,"E1586"),sQuery(id+"F16.wireOp",EDGE,"E1587"),sQuery(id+"F16.wireOp",EDGE,"E1588"),sQuery(id+"F16.wireOp",EDGE,"E1589"),sQuery(id+"F16.wireOp",EDGE,"E1590"),sQuery(id+"F16.wireOp",EDGE,"E1591"),sQuery(id+"F16.wireOp",EDGE,"E1592"),sQuery(id+"F16.wireOp",EDGE,"E1593"),sQuery(id+"F16.wireOp",EDGE,"E1594"),sQuery(id+"F16.wireOp",EDGE,"E1595"),sQuery(id+"F16.wireOp",EDGE,"E1596"),sQuery(id+"F16.wireOp",EDGE,"E1597"),sQuery(id+"F16.wireOp",EDGE,"E1598"),sQuery(id+"F16.wireOp",EDGE,"E1599"),sQuery(id+"F16.wireOp",EDGE,"E1600"),sQuery(id+"F16.wireOp",EDGE,"E1601"),sQuery(id+"F16.wireOp",EDGE,"E1602"),sQuery(id+"F16.wireOp",EDGE,"E1603"),sQuery(id+"F16.wireOp",EDGE,"E1604"),sQuery(id+"F16.wireOp",EDGE,"E1605"),sQuery(id+"F16.wireOp",EDGE,"E1606"),sQuery(id+"F16.wireOp",EDGE,"E1607"),sQuery(id+"F16.wireOp",EDGE,"E1608"),sQuery(id+"F16.wireOp",EDGE,"E1609"),sQuery(id+"F16.wireOp",EDGE,"E1610"),sQuery(id+"F16.wireOp",EDGE,"E1611"),sQuery(id+"F16.wireOp",EDGE,"E1612"),sQuery(id+"F16.wireOp",EDGE,"E1613"),sQuery(id+"F16.wireOp",EDGE,"E1614"),sQuery(id+"F16.wireOp",EDGE,"E1615"),sQuery(id+"F16.wireOp",EDGE,"E1616")])]});
            var Q4;
            Q4=makeQuery(id+"F17.opExtrude","SWEPT_BODY",BODY,{"disambiguationData":[OSD([sQuery(id+"F16.wireOp",EDGE,"E1053"),sQuery(id+"F16.wireOp",EDGE,"E1054"),sQuery(id+"F16.wireOp",EDGE,"E1055"),sQuery(id+"F16.wireOp",EDGE,"E1056"),sQuery(id+"F16.wireOp",EDGE,"E1057"),sQuery(id+"F16.wireOp",EDGE,"E1058"),sQuery(id+"F16.wireOp",EDGE,"E1059"),sQuery(id+"F16.wireOp",EDGE,"E1060"),sQuery(id+"F16.wireOp",EDGE,"E1061"),sQuery(id+"F16.wireOp",EDGE,"E1062"),sQuery(id+"F16.wireOp",EDGE,"E1063"),sQuery(id+"F16.wireOp",EDGE,"E1064"),sQuery(id+"F16.wireOp",EDGE,"E1065"),sQuery(id+"F16.wireOp",EDGE,"E1066"),sQuery(id+"F16.wireOp",EDGE,"E1067"),sQuery(id+"F16.wireOp",EDGE,"E1068"),sQuery(id+"F16.wireOp",EDGE,"E1069"),sQuery(id+"F16.wireOp",EDGE,"E1070"),sQuery(id+"F16.wireOp",EDGE,"E1071"),sQuery(id+"F16.wireOp",EDGE,"E1072"),sQuery(id+"F16.wireOp",EDGE,"E1073"),sQuery(id+"F16.wireOp",EDGE,"E1074"),sQuery(id+"F16.wireOp",EDGE,"E1075"),sQuery(id+"F16.wireOp",EDGE,"E1076"),sQuery(id+"F16.wireOp",EDGE,"E1077"),sQuery(id+"F16.wireOp",EDGE,"E1078")])]});
            var Q5;
            Q5=makeQuery(id+"F1.opExtrude","SWEPT_BODY",BODY,{"disambiguationData":[OSD([sQuery(id+"F0.wireOp",EDGE,"E0.bottom"),sQuery(id+"F0.wireOp",EDGE,"E0.top"),sQuery(id+"F0.wireOp",EDGE,"E0.left"),sQuery(id+"F0.wireOp",EDGE,"E0.right"),sQuery(id+"F0.wireOp",EDGE,"E1.0"),sQuery(id+"F0.wireOp",EDGE,"E1.1"),sQuery(id+"F0.wireOp",EDGE,"E1.2"),sQuery(id+"F0.wireOp",EDGE,"E1.3")])]});
            booleanBodies(context, id + "F20", {"operationType" : BooleanOperationType.SUBTRACTION, "tools" : qUnion([Q0, Q1, Q2, Q3, Q4]), "targets" : qUnion([Q5])});
        }
    });
